FCSTD DOCUMENT  (FreeCAD 0.20R29603 (Git))
Label: assembly
Comment: LumenPnP
License: GPL-3.0 license
LicenseURL: https://github.com/opulo-inc/lumenpnp/blob/main/LICENSE
objects: Part::FeaturePython×437, App::DocumentObjectGroup×34
note: 437 computed .brp shape members not serialized (recipe doc carries the construction recipe); baked Part::Feature solids carry a one-line shape summary decoded from their .brp

FEATURE [Part::FeaturePython] b_OTS_0009_20x20_v_slot_600mm1_001_003  label="vslot-extrusion-20mmx20mmx600mm005"  # a2plus imported part (geometry in sourceFile) (typed FeaturePython)
  Placement = pos=(-0.0573608,219.183,133.936) rot=(0.57735,-0.57735,-0.57735;2.0944rad)
  Visibility1 = true
  a2p_Version = V0.1
  fixedPosition = false
  objectType = a2pPart
  sourceFile = ./MISC/vslot-extrusion-20mmx20mmx600mm.step
  sourcePart = vslot-extrusion-20mmx20mmx600mm
  subassemblyImport = false
  timeLastImport = 1.66119e+09
  updateColors = true
FEATURE [Part::FeaturePython] b_FDM_0008_y_gantry_support_001_  label="y-gantry-support"  # a2plus imported part (geometry in sourceFile) (typed FeaturePython)
  Placement = pos=(32.0603,209.134,74.2154) rot=(0.57735,-0.57735,-0.57735;2.0944rad)
  Visibility1 = true
  a2p_Version = V0.1
  fixedPosition = false
  objectType = a2pPart
  sourceFile = ./FDM/y-gantry-support.FCStd
  sourcePart = Body
  subassemblyImport = false
  timeLastImport = 1.6657e+09
  updateColors = true
FEATURE [Part::FeaturePython] b_FDM_0008_y_gantry_support_001_001  label="y-gantry-support001"  # a2plus imported part (geometry in sourceFile) (typed FeaturePython)
  Placement = pos=(568.145,209.119,74.2225) rot=(0.57735,0.57735,0.57735;2.0944rad)
  Visibility1 = true
  a2p_Version = V0.1
  fixedPosition = false
  objectType = a2pPart
  sourceFile = ./FDM/y-gantry-support.FCStd
  sourcePart = Body
  subassemblyImport = false
  timeLastImport = 1.6657e+09
  updateColors = true
FEATURE [Part::FeaturePython] b_FDM_0009_roller_spacer_001_  label="roller-spacer"  # a2plus imported part (geometry in sourceFile) (typed FeaturePython)
  Placement = pos=(22.0728,209.128,80.348) rot=(0.707107,-0.707107,0;3.14159rad)
  Visibility1 = true
  a2p_Version = V0.1
  fixedPosition = false
  objectType = a2pPart
  sourceFile = ./FDM/roller-spacer.FCStd
  sourcePart = Body
  subassemblyImport = false
  timeLastImport = 1.65531e+09
  updateColors = true
FEATURE [Part::FeaturePython] b_v_slot_roller1_001_  label="vslot-roller"  # a2plus imported part (geometry in sourceFile) (typed FeaturePython)
  Placement = pos=(10.7746,213.864,116.699) rot=(0,0,-1;1.5708rad)
  Visibility1 = true
  a2p_Version = V0.1
  fixedPosition = false
  objectType = a2pPart
  sourceFile = ./MISC/vslot-roller.step
  sourcePart = vslot-roller
  subassemblyImport = false
  timeLastImport = 1.66119e+09
  updateColors = true
FEATURE [Part::FeaturePython] b_v_slot_roller1_001_001  label="vslot-roller001"  # a2plus imported part (geometry in sourceFile) (typed FeaturePython)
  Placement = pos=(10.7212,173.877,116.658) rot=(0,0,-1;1.5708rad)
  Visibility1 = true
  a2p_Version = V0.1
  fixedPosition = false
  objectType = a2pPart
  sourceFile = ./MISC/vslot-roller.step
  sourcePart = vslot-roller
  subassemblyImport = false
  timeLastImport = 1.66119e+09
  updateColors = true
FEATURE [Part::FeaturePython] b_FDM_0009_roller_spacer_001_001  label="roller-spacer001"  # a2plus imported part (geometry in sourceFile) (typed FeaturePython)
  Placement = pos=(-1.94462,209.167,80.3524) rot=(0,0,-1;1.5708rad)
  Visibility1 = true
  a2p_Version = V0.1
  fixedPosition = false
  objectType = a2pPart
  sourceFile = ./FDM/roller-spacer.FCStd
  sourcePart = Body
  subassemblyImport = false
  timeLastImport = 1.65531e+09
  updateColors = true
FEATURE [Part::FeaturePython] b_v_slot_roller1_001_002  label="vslot-roller002"  # a2plus imported part (geometry in sourceFile) (typed FeaturePython)
  Placement = pos=(10.791,193.862,77.3523) rot=(0,0,-1;1.5708rad)
  Visibility1 = true
  a2p_Version = V0.1
  fixedPosition = false
  objectType = a2pPart
  sourceFile = ./MISC/vslot-roller.step
  sourcePart = vslot-roller
  subassemblyImport = false
  timeLastImport = 1.66119e+09
  updateColors = true
FEATURE [Part::FeaturePython] Screw003  label="M5x40-Screw"  # Fasteners workbench fastener (typed FeaturePython)
  Placement = pos=(-6.95,189.16,119.74) rot=(0.57735,-0.57735,-0.57735;2.0944rad)
  Visibility1 = true
  diameter = 6
  invert = false
  leftHanded = false
  length = 12
  lengthCustom = 40
  matchOuter = false
  offset = 0
  thread = false
  type = 33
FEATURE [Part::FeaturePython] Screw004  label="M5x40-Screw334"  # Fasteners workbench fastener (typed FeaturePython)
  Placement = pos=(-6.95,229.11,119.74) rot=(0.57735,-0.57735,-0.57735;2.0944rad)
  Visibility1 = true
  diameter = 6
  invert = false
  leftHanded = false
  length = 12
  lengthCustom = 40
  matchOuter = false
  offset = 0
  thread = false
  type = 33
FEATURE [Part::FeaturePython] Screw005  label="M5x40-Screw335"  # Fasteners workbench fastener (typed FeaturePython)
  Placement = pos=(-6.95,209.15,80.34) rot=(0.57735,-0.57735,-0.57735;2.0944rad)
  Visibility1 = true
  diameter = 6
  invert = false
  leftHanded = false
  length = 12
  lengthCustom = 40
  matchOuter = false
  offset = 0
  thread = false
  type = 33
FEATURE [Part::FeaturePython] Nut003  label="M5-Nut"  # Fasteners workbench fastener (typed FeaturePython)
  Placement = pos=(28.1459,229.05,119.689) rot=(0.447214,0.774597,0.447214;1.82348rad)
  Visibility1 = true
  diameter = 7
  invert = false
  leftHanded = false
  matchOuter = false
  offset = 0
  thread = false
  type = 7
FEATURE [Part::FeaturePython] Nut004  label="M5-Nut599"  # Fasteners workbench fastener (typed FeaturePython)
  Placement = pos=(28.1459,189.008,119.713) rot=(0.447214,0.774597,0.447214;1.82348rad)
  Visibility1 = true
  diameter = 7
  invert = false
  leftHanded = false
  matchOuter = false
  offset = 0
  thread = false
  type = 7
FEATURE [Part::FeaturePython] Nut005  label="M5-Nut600"  # Fasteners workbench fastener (typed FeaturePython)
  Placement = pos=(28.1459,209.108,80.3492) rot=(0.447214,0.774597,0.447214;1.82348rad)
  Visibility1 = true
  diameter = 7
  invert = false
  leftHanded = false
  matchOuter = false
  offset = 0
  thread = false
  type = 7
FEATURE [Part::FeaturePython] Screw006  label="M3x16-Screw"  # Fasteners workbench fastener (typed FeaturePython)
  Placement = pos=(25.03,209.15,61.89) rot=(0.707107,-0.707107,0;3.14159rad)
  Visibility1 = true
  diameter = 4
  invert = false
  leftHanded = false
  length = 6
  lengthCustom = 16
  matchOuter = false
  offset = 0
  thread = false
  type = 33
FEATURE [Part::FeaturePython] Screw007  label="M3x16-Screw097"  # Fasteners workbench fastener (typed FeaturePython)
  Placement = pos=(-4.46,209.15,61.89) rot=(0.707107,-0.707107,0;3.14159rad)
  Visibility1 = true
  diameter = 4
  invert = false
  leftHanded = false
  length = 6
  lengthCustom = 16
  matchOuter = false
  offset = 0
  thread = false
  type = 33
FEATURE [Part::FeaturePython] Nut006  label="M3-Nut"  # Fasteners workbench fastener (typed FeaturePython)
  Placement = pos=(-4.50438,209.156,68.38) rot=(0.707107,-0.707107,0;3.14159rad)
  Visibility1 = true
  diameter = 4
  invert = false
  leftHanded = false
  matchOuter = false
  offset = 0
  thread = false
  type = 4
FEATURE [Part::FeaturePython] Nut007  label="M3-Nut589"  # Fasteners workbench fastener (typed FeaturePython)
  Placement = pos=(24.9349,209.069,68.45) rot=(0,1,0;3.14159rad)
  Visibility1 = true
  diameter = 4
  invert = false
  leftHanded = false
  matchOuter = false
  offset = 0
  thread = false
  type = 4
FEATURE [Part::FeaturePython] Screw016  label="M5x40-Screw336"  # Fasteners workbench fastener (typed FeaturePython)
  Placement = pos=(607.25,189.09,119.82) rot=(0.57735,0.57735,0.57735;2.0944rad)
  Visibility1 = true
  diameter = 6
  invert = false
  leftHanded = false
  length = 12
  lengthCustom = 40
  matchOuter = false
  offset = 0
  thread = false
  type = 33
FEATURE [Part::FeaturePython] b_v_slot_roller1_001_006  label="vslot-roller003"  # a2plus imported part (geometry in sourceFile) (typed FeaturePython)
  Placement = pos=(590.83,186.117,135.005) rot=(0.57735,0.57735,0.57735;4.18879rad)
  Visibility1 = true
  a2p_Version = V0.1
  fixedPosition = false
  objectType = a2pPart
  sourceFile = ./MISC/vslot-roller.step
  sourcePart = vslot-roller
  subassemblyImport = false
  timeLastImport = 1.66119e+09
  updateColors = true
FEATURE [Part::FeaturePython] b_v_slot_roller1_001_007  label="vslot-roller004"  # a2plus imported part (geometry in sourceFile) (typed FeaturePython)
  Placement = pos=(590.853,213.81,116.722) rot=(0,0,-1;1.5708rad)
  Visibility1 = true
  a2p_Version = V0.1
  fixedPosition = false
  objectType = a2pPart
  sourceFile = ./MISC/vslot-roller.step
  sourcePart = vslot-roller
  subassemblyImport = false
  timeLastImport = 1.66119e+09
  updateColors = true
FEATURE [Part::FeaturePython] Screw017  label="M5x40-Screw337"  # Fasteners workbench fastener (typed FeaturePython)
  Placement = pos=(607.25,229.1,119.82) rot=(0.57735,0.57735,0.57735;2.0944rad)
  Visibility1 = true
  diameter = 6
  invert = false
  leftHanded = false
  length = 12
  lengthCustom = 40
  matchOuter = false
  offset = 0
  thread = false
  type = 33
FEATURE [Part::FeaturePython] Screw018  label="M5x40-Screw338"  # Fasteners workbench fastener (typed FeaturePython)
  Placement = pos=(607.25,209.12,80.38) rot=(0.57735,0.57735,0.57735;2.0944rad)
  Visibility1 = true
  diameter = 6
  invert = false
  leftHanded = false
  length = 12
  lengthCustom = 40
  matchOuter = false
  offset = 0
  thread = false
  type = 33
FEATURE [Part::FeaturePython] b_v_slot_roller1_001_008  label="vslot-roller005"  # a2plus imported part (geometry in sourceFile) (typed FeaturePython)
  Placement = pos=(590.853,193.81,77.3723) rot=(0,0,-1;1.5708rad)
  Visibility1 = true
  a2p_Version = V0.1
  fixedPosition = false
  objectType = a2pPart
  sourceFile = ./MISC/vslot-roller.step
  sourcePart = vslot-roller
  subassemblyImport = false
  timeLastImport = 1.66119e+09
  updateColors = true
FEATURE [Part::FeaturePython] Nut016  label="M5-Nut601"  # Fasteners workbench fastener (typed FeaturePython)
  Placement = pos=(568.626,209.08,80.4002) rot=(0.447214,0.774597,0.447214;1.82348rad)
  Visibility1 = true
  diameter = 7
  invert = false
  leftHanded = false
  matchOuter = false
  offset = 0
  thread = false
  type = 7
FEATURE [Part::FeaturePython] Nut017  label="M5-Nut602"  # Fasteners workbench fastener (typed FeaturePython)
  Placement = pos=(568.626,189.034,119.779) rot=(0.447214,0.774597,0.447214;1.82348rad)
  Visibility1 = true
  diameter = 7
  invert = false
  leftHanded = false
  matchOuter = false
  offset = 0
  thread = false
  type = 7
FEATURE [Part::FeaturePython] Nut018  label="M5-Nut603"  # Fasteners workbench fastener (typed FeaturePython)
  Placement = pos=(568.626,229.099,119.753) rot=(0.447214,0.774597,0.447214;1.82348rad)
  Visibility1 = true
  diameter = 7
  invert = false
  leftHanded = false
  matchOuter = false
  offset = 0
  thread = false
  type = 7
FEATURE [Part::FeaturePython] Screw019  label="M3x16-Screw095"  # Fasteners workbench fastener (typed FeaturePython)
  Placement = pos=(575.13,209.15,61.89) rot=(0.707107,-0.707107,0;3.14159rad)
  Visibility1 = true
  diameter = 4
  invert = false
  leftHanded = false
  length = 6
  lengthCustom = 16
  matchOuter = false
  offset = 0
  thread = false
  type = 33
FEATURE [Part::FeaturePython] Screw020  label="M3x16-Screw096"  # Fasteners workbench fastener (typed FeaturePython)
  Placement = pos=(604.72,209.12,61.89) rot=(0.707107,-0.707107,0;3.14159rad)
  Visibility1 = true
  diameter = 4
  invert = false
  leftHanded = false
  length = 6
  lengthCustom = 16
  matchOuter = false
  offset = 0
  thread = false
  type = 33
FEATURE [Part::FeaturePython] Nut019  label="M3-Nut588"  # Fasteners workbench fastener (typed FeaturePython)
  Placement = pos=(575.367,209.236,68.44) rot=(0.707107,-0.707107,0;3.14159rad)
  Visibility1 = true
  diameter = 4
  invert = false
  leftHanded = false
  matchOuter = false
  offset = 0
  thread = false
  type = 4
FEATURE [Part::FeaturePython] Nut020  label="M3-Nut587"  # Fasteners workbench fastener (typed FeaturePython)
  Placement = pos=(604.736,209.133,68.46) rot=(0,1,0;3.14159rad)
  Visibility1 = true
  diameter = 4
  invert = false
  leftHanded = false
  matchOuter = false
  offset = 0
  thread = false
  type = 4
FEATURE [Part::FeaturePython] b_FDM_0009_roller_spacer_001_002  label="roller-spacer002"  # a2plus imported part (geometry in sourceFile) (typed FeaturePython)
  Placement = pos=(578.105,209.167,80.3524) rot=(0,0,-1;1.5708rad)
  Visibility1 = true
  a2p_Version = V0.1
  fixedPosition = false
  objectType = a2pPart
  sourceFile = ./FDM/roller-spacer.FCStd
  sourcePart = Body
  subassemblyImport = false
  timeLastImport = 1.65531e+09
  updateColors = true
FEATURE [Part::FeaturePython] b_FDM_0009_roller_spacer_001_003  label="roller-spacer003"  # a2plus imported part (geometry in sourceFile) (typed FeaturePython)
  Placement = pos=(602.155,209.167,80.3524) rot=(0,0,1;1.5708rad)
  Visibility1 = true
  a2p_Version = V0.1
  fixedPosition = false
  objectType = a2pPart
  sourceFile = ./FDM/roller-spacer.FCStd
  sourcePart = Body
  subassemblyImport = false
  timeLastImport = 1.65531e+09
  updateColors = true
FEATURE [Part::FeaturePython] Screw021  label="M5x40-Screw339"  # Fasteners workbench fastener (typed FeaturePython)
  Placement = pos=(634.23,194.1,163.97) rot=(0,0,1;1.5708rad)
  Visibility1 = true
  diameter = 6
  invert = false
  leftHanded = false
  length = 12
  lengthCustom = 40
  matchOuter = false
  offset = 0
  thread = false
  type = 33
FEATURE [Part::FeaturePython] Screw022  label="M5x10-Screw"  # Fasteners workbench fastener (typed FeaturePython)
  Placement = pos=(25.1,209.12,158.94) rot=(0,0,-1;1.5708rad)
  Visibility1 = true
  diameter = 6
  invert = false
  leftHanded = false
  length = 1
  lengthCustom = 10
  matchOuter = false
  offset = 0
  thread = false
  type = 33
FEATURE [Part::FeaturePython] b_M5_tslot_nut1_001_  label="M5-tslot-nut"  # a2plus imported part (geometry in sourceFile) (typed FeaturePython)
  Placement = pos=(25.0282,209.312,148.905) rot=(0,0,1;0rad)
  Visibility1 = true
  a2p_Version = V0.1
  fixedPosition = false
  objectType = a2pPart
  sourceFile = ./FST/M5-tslot-nut.step
  sourcePart = M5-tslot-nut
  subassemblyImport = false
  timeLastImport = 1.66119e+09
  updateColors = true
FEATURE [Part::FeaturePython] b_M5_tslot_nut1_001_001  label="M5-tslot-nut001"  # a2plus imported part (geometry in sourceFile) (typed FeaturePython)
  Placement = pos=(572.328,209.112,148.905) rot=(0,0,1;0rad)
  Visibility1 = true
  a2p_Version = V0.1
  fixedPosition = false
  objectType = a2pPart
  sourceFile = ./FST/M5-tslot-nut.step
  sourcePart = M5-tslot-nut
  subassemblyImport = false
  timeLastImport = 1.66119e+09
  updateColors = true
FEATURE [Part::FeaturePython] Screw023  label="M5x10-Screw321"  # Fasteners workbench fastener (typed FeaturePython)
  Placement = pos=(572.27,209.12,158.94) rot=(0,0,-1;1.5708rad)
  Visibility1 = true
  diameter = 6
  invert = false
  leftHanded = false
  length = 1
  lengthCustom = 10
  matchOuter = false
  offset = 0
  thread = false
  type = 33
FEATURE [Part::FeaturePython] Screw025  label="M5x10-Screw369"  # Fasteners workbench fastener (typed FeaturePython)
  Placement = pos=(-15.24,236.1,92.45) rot=(0.57735,-0.57735,-0.57735;2.0944rad)
  Visibility1 = true
  diameter = 6
  invert = false
  leftHanded = false
  length = 1
  lengthCustom = 10
  matchOuter = false
  offset = 0
  thread = false
  type = 33
FEATURE [Part::FeaturePython] b_FDM_0027_belt_clamp_001_  label="belt-clamp001"  # a2plus imported part (geometry in sourceFile) (typed FeaturePython)
  Placement = pos=(-12.0481,236.126,99.9408) rot=(0.57735,-0.57735,-0.57735;2.0944rad)
  Visibility1 = true
  a2p_Version = V0.1
  fixedPosition = false
  objectType = a2pPart
  sourceFile = ./FDM/belt-clamp.FCStd
  sourcePart = Body
  subassemblyImport = false
  timeLastImport = 1.66215e+09
  updateColors = true
FEATURE [Part::FeaturePython] Screw026  label="M5x10-Screw370"  # Fasteners workbench fastener (typed FeaturePython)
  Placement = pos=(-15.24,236.1,107.47) rot=(0.57735,-0.57735,-0.57735;2.0944rad)
  Visibility1 = true
  diameter = 6
  invert = false
  leftHanded = false
  length = 1
  lengthCustom = 10
  matchOuter = false
  offset = 0
  thread = false
  type = 33
FEATURE [Part::FeaturePython] Screw027  label="M5x10-Screw371"  # Fasteners workbench fastener (typed FeaturePython)
  Placement = pos=(-15.24,182.19,107.47) rot=(0.57735,-0.57735,-0.57735;2.0944rad)
  Visibility1 = true
  diameter = 6
  invert = false
  leftHanded = false
  length = 1
  lengthCustom = 10
  matchOuter = false
  offset = 0
  thread = false
  type = 33
FEATURE [Part::FeaturePython] Screw028  label="M5x10-Screw372"  # Fasteners workbench fastener (typed FeaturePython)
  Placement = pos=(-15.24,182.19,92.5) rot=(0.57735,-0.57735,-0.57735;2.0944rad)
  Visibility1 = true
  diameter = 6
  invert = false
  leftHanded = false
  length = 1
  lengthCustom = 10
  matchOuter = false
  offset = 0
  thread = false
  type = 33
FEATURE [Part::FeaturePython] b_FDM_0027_belt_clamp_001_001  label="belt-clamp002"  # a2plus imported part (geometry in sourceFile) (typed FeaturePython)
  Placement = pos=(-12.0481,182.176,99.9408) rot=(0.57735,-0.57735,-0.57735;2.0944rad)
  Visibility1 = true
  a2p_Version = V0.1
  fixedPosition = false
  objectType = a2pPart
  sourceFile = ./FDM/belt-clamp.FCStd
  sourcePart = Body
  subassemblyImport = false
  timeLastImport = 1.66215e+09
  updateColors = true
FEATURE [Part::FeaturePython] Screw099  label="M3x8-Screw442"  # Fasteners workbench fastener (typed FeaturePython)
  Placement = pos=(-58.97,224.63,158.88) rot=(1,0,0;3.14159rad)
  Visibility1 = true
  diameter = 1
  invert = false
  leftHanded = false
  length = 1
  lengthCustom = 8
  matchOuter = false
  offset = 0
  thread = false
  type = 39
FEATURE [Part::FeaturePython] Screw097  label="M3x8-Screw443"  # Fasteners workbench fastener (typed FeaturePython)
  Placement = pos=(-27.96,224.63,158.88) rot=(1,0,0;3.14159rad)
  Visibility1 = true
  diameter = 1
  invert = false
  leftHanded = false
  length = 1
  lengthCustom = 8
  matchOuter = false
  offset = 0
  thread = false
  type = 39
FEATURE [Part::FeaturePython] Screw100  label="M3x8-Screw444"  # Fasteners workbench fastener (typed FeaturePython)
  Placement = pos=(-58.97,193.61,158.88) rot=(1,0,0;3.14159rad)
  Visibility1 = true
  diameter = 1
  invert = false
  leftHanded = false
  length = 1
  lengthCustom = 8
  matchOuter = false
  offset = 0
  thread = false
  type = 39
FEATURE [Part::FeaturePython] Screw098  label="M3x8-Screw445"  # Fasteners workbench fastener (typed FeaturePython)
  Placement = pos=(-27.96,193.61,158.88) rot=(1,0,0;3.14159rad)
  Visibility1 = true
  diameter = 1
  invert = false
  leftHanded = false
  length = 1
  lengthCustom = 8
  matchOuter = false
  offset = 0
  thread = false
  type = 39
FEATURE [Part::FeaturePython] Screw059  label="M5x25-Screw122"  # Fasteners workbench fastener (typed FeaturePython)
  Placement = pos=(634.17,209.27,154.08) rot=(0,0,1;1.5708rad)
  Visibility1 = true
  diameter = 6
  invert = false
  leftHanded = false
  length = 6
  lengthCustom = 25
  matchOuter = false
  offset = 0
  thread = false
  type = 33
FEATURE [Part::FeaturePython] Screw060  label="M3x16-Screw084"  # Fasteners workbench fastener (typed FeaturePython)
  Placement = pos=(638.25,224.21,144.08) rot=(0.57735,-0.57735,0.57735;4.18879rad)
  Visibility1 = true
  diameter = 4
  invert = false
  leftHanded = false
  length = 6
  lengthCustom = 16
  matchOuter = false
  offset = 0
  thread = false
  type = 33
FEATURE [Part::FeaturePython] Screw058  label="M5x10-Screw373"  # Fasteners workbench fastener (typed FeaturePython)
  Placement = pos=(615.37,236.11,107.53) rot=(0.57735,0.57735,0.57735;2.0944rad)
  Visibility1 = true
  diameter = 6
  invert = false
  leftHanded = false
  length = 1
  lengthCustom = 10
  matchOuter = false
  offset = 0
  thread = false
  type = 33
FEATURE [Part::FeaturePython] Screw057  label="M5x10-Screw374"  # Fasteners workbench fastener (typed FeaturePython)
  Placement = pos=(615.37,236.11,92.54) rot=(0.57735,0.57735,0.57735;2.0944rad)
  Visibility1 = true
  diameter = 6
  invert = false
  leftHanded = false
  length = 1
  lengthCustom = 10
  matchOuter = false
  offset = 0
  thread = false
  type = 33
FEATURE [Part::FeaturePython] Screw056  label="M5x10-Screw367"  # Fasteners workbench fastener (typed FeaturePython)
  Placement = pos=(615.37,182.19,92.54) rot=(0.57735,0.57735,0.57735;2.0944rad)
  Visibility1 = true
  diameter = 6
  invert = false
  leftHanded = false
  length = 1
  lengthCustom = 10
  matchOuter = false
  offset = 0
  thread = false
  type = 33
FEATURE [Part::FeaturePython] b_FDM_0027_belt_clamp_001_005  label="belt-clamp003"  # a2plus imported part (geometry in sourceFile) (typed FeaturePython)
  Placement = pos=(612.402,182.156,99.9408) rot=(0.57735,0.57735,0.57735;2.0944rad)
  Visibility1 = true
  a2p_Version = V0.1
  fixedPosition = false
  objectType = a2pPart
  sourceFile = ./FDM/belt-clamp.FCStd
  sourcePart = Body
  subassemblyImport = false
  timeLastImport = 1.66215e+09
  updateColors = true
FEATURE [Part::FeaturePython] b_FDM_0027_belt_clamp_001_004  label="belt-clamp004"  # a2plus imported part (geometry in sourceFile) (typed FeaturePython)
  Placement = pos=(612.402,236.126,100.011) rot=(0.57735,0.57735,0.57735;2.0944rad)
  Visibility1 = true
  a2p_Version = V0.1
  fixedPosition = false
  objectType = a2pPart
  sourceFile = ./FDM/belt-clamp.FCStd
  sourcePart = Body
  subassemblyImport = false
  timeLastImport = 1.66215e+09
  updateColors = true
FEATURE [Part::FeaturePython] b_Nema_17_42A02C_v21_001_001  label="NEMA17-stepper"  # a2plus imported part (geometry in sourceFile) (typed FeaturePython)
  Placement = pos=(-43.4338,209.138,153.958) rot=(1,0,0;3.14159rad)
  Visibility1 = true
  a2p_Version = V0.1
  fixedPosition = false
  objectType = a2pPart
  sourceFile = ./MISC/NEMA17-stepper.step 
  sourcePart = NEMA17-stepper
  subassemblyImport = false
  timeLastImport = 1.64563e+09
  updateColors = true
FEATURE [Part::FeaturePython] Nut043  label="M5-Nut604"  # Fasteners workbench fastener (typed FeaturePython)
  Placement = pos=(634.166,209.269,134.219) rot=(0.707107,-0.707107,0;3.14159rad)
  Visibility1 = true
  diameter = 3
  invert = false
  leftHanded = false
  matchOuter = false
  offset = 0
  thread = false
  type = 5
FEATURE [Part::FeaturePython] Nut042  label="M5-Nut605"  # Fasteners workbench fastener (typed FeaturePython)
  Placement = pos=(634.224,194.15,128.957) rot=(0.866025,0.5,0;3.14159rad)
  Visibility1 = true
  diameter = 3
  invert = false
  leftHanded = false
  matchOuter = false
  offset = 0
  thread = false
  type = 5
FEATURE [Part::FeaturePython] b_Gates_2GT_20T_Toothed_Pulley1_001_001  label="GT2-pulley"  # a2plus imported part (geometry in sourceFile) (typed FeaturePython)
  Placement = pos=(-43.4196,209.139,155.221) rot=(0.57735,0.57735,-0.57735;4.18879rad)
  Visibility1 = true
  a2p_Version = V0.1
  fixedPosition = false
  objectType = a2pPart
  sourceFile = ./cad/MISC/GT2-pulley.STEP
  sourcePart = GT2-pulley
  subassemblyImport = false
  timeLastImport = 1.64563e+09
  updateColors = true
FEATURE [Part::FeaturePython] b_Gates_2GT_20T_Toothed_Idler1_001_002  label="GT2-idler"  # a2plus imported part (geometry in sourceFile) (typed FeaturePython)
  Placement = pos=(634.179,209.286,138.99) rot=(0.57735,-0.57735,-0.57735;2.0944rad)
  Visibility1 = true
  a2p_Version = V0.1
  fixedPosition = false
  objectType = a2pPart
  sourceFile = ./cad/MISC/GT2-idler.STEP
  sourcePart = GT2-idler
  subassemblyImport = false
  timeLastImport = 1.64563e+09
  updateColors = true
FEATURE [Part::FeaturePython] Screw055  label="M5x10-Screw368"  # Fasteners workbench fastener (typed FeaturePython)
  Placement = pos=(615.37,182.19,107.47) rot=(0.57735,0.57735,0.57735;2.0944rad)
  Visibility1 = true
  diameter = 6
  invert = false
  leftHanded = false
  length = 1
  lengthCustom = 10
  matchOuter = false
  offset = 0
  thread = false
  type = 33
FEATURE [Part::FeaturePython] Nut037  label="M5-Nut688"  # Fasteners workbench fastener (typed FeaturePython)
  Placement = pos=(-8.89406,182.185,92.4364) rot=(0.447214,0.774597,0.447214;1.82348rad)
  Visibility1 = true
  diameter = 7
  invert = false
  leftHanded = false
  matchOuter = false
  offset = 0
  thread = false
  type = 7
FEATURE [Part::FeaturePython] Nut035  label="M5-Nut689"  # Fasteners workbench fastener (typed FeaturePython)
  Placement = pos=(-8.89406,236.086,107.516) rot=(0.447214,0.774597,0.447214;1.82348rad)
  Visibility1 = true
  diameter = 7
  invert = false
  leftHanded = false
  matchOuter = false
  offset = 0
  thread = false
  type = 7
FEATURE [Part::FeaturePython] Nut041  label="M5-Nut690"  # Fasteners workbench fastener (typed FeaturePython)
  Placement = pos=(605.676,236.093,107.547) rot=(0.447214,0.774597,0.447214;1.82348rad)
  Visibility1 = true
  diameter = 7
  invert = false
  leftHanded = false
  matchOuter = false
  offset = 0
  thread = false
  type = 7
FEATURE [Part::FeaturePython] Nut040  label="M5-Nut691"  # Fasteners workbench fastener (typed FeaturePython)
  Placement = pos=(605.676,236.072,92.571) rot=(0.447214,0.774597,0.447214;1.82348rad)
  Visibility1 = true
  diameter = 7
  invert = false
  leftHanded = false
  matchOuter = false
  offset = 0
  thread = false
  type = 7
FEATURE [Part::FeaturePython] Nut036  label="M5-Nut692"  # Fasteners workbench fastener (typed FeaturePython)
  Placement = pos=(-8.89406,182.149,107.434) rot=(0.447214,0.774597,0.447214;1.82348rad)
  Visibility1 = true
  diameter = 7
  invert = false
  leftHanded = false
  matchOuter = false
  offset = 0
  thread = false
  type = 7
FEATURE [Part::FeaturePython] Nut034  label="M5-Nut693"  # Fasteners workbench fastener (typed FeaturePython)
  Placement = pos=(-8.89406,236.073,92.5127) rot=(0.447214,0.774597,0.447214;1.82348rad)
  Visibility1 = true
  diameter = 7
  invert = false
  leftHanded = false
  matchOuter = false
  offset = 0
  thread = false
  type = 7
FEATURE [Part::FeaturePython] Nut039  label="M5-Nut694"  # Fasteners workbench fastener (typed FeaturePython)
  Placement = pos=(605.676,182.149,107.514) rot=(0.447214,0.774597,0.447214;1.82348rad)
  Visibility1 = true
  diameter = 7
  invert = false
  leftHanded = false
  matchOuter = false
  offset = 0
  thread = false
  type = 7
FEATURE [Part::FeaturePython] Nut038  label="M5-Nut695"  # Fasteners workbench fastener (typed FeaturePython)
  Placement = pos=(605.676,182.168,92.527) rot=(0.447214,0.774597,0.447214;1.82348rad)
  Visibility1 = true
  diameter = 7
  invert = false
  leftHanded = false
  matchOuter = false
  offset = 0
  thread = false
  type = 7
FEATURE [Part::FeaturePython] Nut044  label="M3-Nut451"  # Fasteners workbench fastener (typed FeaturePython)
  Placement = pos=(632.154,224.209,144.071) rot=(0.447214,-0.774597,-0.447214;1.82348rad)
  Visibility1 = true
  diameter = 4
  invert = false
  leftHanded = false
  matchOuter = false
  offset = 0
  thread = false
  type = 7
FEATURE [Part::FeaturePython] b_MakerBot_LimitSwitchBoard1_001_002  label="limit-switch001"  # a2plus imported part (geometry in sourceFile) (typed FeaturePython)
  Placement = pos=(492.283,187.439,201.553) rot=(0,0,1;3.14159rad)
  Visibility1 = true
  a2p_Version = V0.1
  fixedPosition = false
  objectType = a2pPart
  sourceFile = ./PCB/limit-switch.STEP
  sourcePart = limit-switch
  subassemblyImport = false
  timeLastImport = 1.66119e+09
  updateColors = true
FEATURE [Part::FeaturePython] b_OTS_0002_00_usb_webcam_001_  label="usb-camera"  # a2plus imported part (geometry in sourceFile) (typed FeaturePython)
  Placement = pos=(444.284,221.423,101.09) rot=(1,0,0;3.14159rad)
  Visibility1 = true
  a2p_Version = V0.1
  fixedPosition = false
  objectType = a2pPart
  sourceFile = ./MISC/usb-camera.FCStd
  sourcePart = Body
  subassemblyImport = false
  timeLastImport = 1.66758e+09
  updateColors = true
FEATURE [Part::FeaturePython] b_FDM_0011_x_gantry_front_001_  label="x-gantry-front"  # a2plus imported part (geometry in sourceFile) (typed FeaturePython)
  Placement = pos=(443.743,197.353,123.214) rot=(1,0,0;1.5708rad)
  Visibility1 = true
  a2p_Version = V0.1
  fixedPosition = false
  objectType = a2pPart
  sourceFile = ./FDM/x-gantry-front.FCStd
  sourcePart = Body
  subassemblyImport = false
  timeLastImport = 1.6657e+09
  updateColors = true
FEATURE [Part::FeaturePython] b_FDM_0014_down_camera_mount_001_  label="top-camera-mount"  # a2plus imported part (geometry in sourceFile) (typed FeaturePython)
  Placement = pos=(444.094,221.392,104.569) rot=(0,0,1;3.14159rad)
  Visibility1 = true
  a2p_Version = V0.1
  fixedPosition = false
  objectType = a2pPart
  sourceFile = ./FDM/top-camera-mount.FCStd
  sourcePart = Body
  subassemblyImport = false
  timeLastImport = 1.66759e+09
  updateColors = true
FEATURE [Part::FeaturePython] b_FDM_0015_down_light_mount_001_  label="top-light-mount"  # a2plus imported part (geometry in sourceFile) (typed FeaturePython)
  Placement = pos=(444.05,221.445,81.0718) rot=(-0.831467,0.554706,-0.031047;0rad)
  Visibility1 = true
  a2p_Version = V0.1
  fixedPosition = false
  objectType = a2pPart
  sourceFile = ./FDM/top-light-mount.FCStd
  sourcePart = Body
  subassemblyImport = false
  timeLastImport = 1.66758e+09
  updateColors = true
FEATURE [Part::FeaturePython] b_v_slot_roller1_001_003  label="vslot-roller006"  # a2plus imported part (geometry in sourceFile) (typed FeaturePython)
  Placement = pos=(415.819,209.923,180.083) rot=(0,-1,0;1.5708rad)
  Visibility1 = true
  a2p_Version = V0.1
  fixedPosition = false
  objectType = a2pPart
  sourceFile = ./MISC/vslot-roller.step
  sourcePart = vslot-roller
  subassemblyImport = false
  timeLastImport = 1.66119e+09
  updateColors = true
FEATURE [Part::FeaturePython] b_v_slot_roller1_001_004  label="vslot-roller007"  # a2plus imported part (geometry in sourceFile) (typed FeaturePython)
  Placement = pos=(477.819,209.923,180.083) rot=(0,-1,0;1.5708rad)
  Visibility1 = true
  a2p_Version = V0.1
  fixedPosition = false
  objectType = a2pPart
  sourceFile = ./MISC/vslot-roller.step
  sourcePart = vslot-roller
  subassemblyImport = false
  timeLastImport = 1.66119e+09
  updateColors = true
FEATURE [Part::FeaturePython] b_FDM_0027_belt_clamp_001_002  label="belt-clamp005"  # a2plus imported part (geometry in sourceFile) (typed FeaturePython)
  Placement = pos=(422.82,231.252,143.964) rot=(-1,0,0;1.5708rad)
  Visibility1 = true
  a2p_Version = V0.1
  fixedPosition = false
  objectType = a2pPart
  sourceFile = ./FDM/belt-clamp.FCStd
  sourcePart = Body
  subassemblyImport = false
  timeLastImport = 1.66215e+09
  updateColors = true
FEATURE [Part::FeaturePython] Nut021  label="M5-Nut646"  # Fasteners workbench fastener (typed FeaturePython)
  Placement = pos=(464.836,225.2,151.517) rot=(-0.186157,0.694747,0.694747;2.77349rad)
  Visibility1 = true
  diameter = 7
  invert = false
  leftHanded = false
  matchOuter = false
  offset = 0
  thread = false
  type = 7
FEATURE [Part::FeaturePython] Nut022  label="M5-Nut647"  # Fasteners workbench fastener (typed FeaturePython)
  Placement = pos=(464.776,225.2,136.591) rot=(-0.186157,0.694747,0.694747;2.77349rad)
  Visibility1 = true
  diameter = 7
  invert = false
  leftHanded = false
  matchOuter = false
  offset = 0
  thread = false
  type = 7
FEATURE [Part::FeaturePython] Screw038  label="M5x10-Screw356"  # Fasteners workbench fastener (typed FeaturePython)
  Placement = pos=(464.84,234.23,136.48) rot=(0.57735,0.57735,0.57735;4.18879rad)
  Visibility1 = true
  diameter = 6
  invert = false
  leftHanded = false
  length = 1
  lengthCustom = 10
  matchOuter = false
  offset = 0
  thread = false
  type = 33
FEATURE [Part::FeaturePython] Screw039  label="M5x10-Screw357"  # Fasteners workbench fastener (typed FeaturePython)
  Placement = pos=(464.74,234.23,151.54) rot=(0.57735,0.57735,0.57735;4.18879rad)
  Visibility1 = true
  diameter = 6
  invert = false
  leftHanded = false
  length = 1
  lengthCustom = 10
  matchOuter = false
  offset = 0
  thread = false
  type = 33
FEATURE [Part::FeaturePython] Nut023  label="M5-Nut648"  # Fasteners workbench fastener (typed FeaturePython)
  Placement = pos=(422.834,225.2,136.517) rot=(-0.186157,0.694747,0.694747;2.77349rad)
  Visibility1 = true
  diameter = 7
  invert = false
  leftHanded = false
  matchOuter = false
  offset = 0
  thread = false
  type = 7
FEATURE [Part::FeaturePython] Nut024  label="M5-Nut649"  # Fasteners workbench fastener (typed FeaturePython)
  Placement = pos=(422.794,225.2,151.519) rot=(-0.186157,0.694747,0.694747;2.77349rad)
  Visibility1 = true
  diameter = 7
  invert = false
  leftHanded = false
  matchOuter = false
  offset = 0
  thread = false
  type = 7
FEATURE [Part::FeaturePython] Screw040  label="M5x10-Screw358"  # Fasteners workbench fastener (typed FeaturePython)
  Placement = pos=(422.86,234.23,151.54) rot=(0.57735,0.57735,0.57735;4.18879rad)
  Visibility1 = true
  diameter = 6
  invert = false
  leftHanded = false
  length = 1
  lengthCustom = 10
  matchOuter = false
  offset = 0
  thread = false
  type = 33
FEATURE [Part::FeaturePython] b_FDM_0027_belt_clamp_001_003  label="belt-clamp006"  # a2plus imported part (geometry in sourceFile) (typed FeaturePython)
  Placement = pos=(464.82,231.252,144.064) rot=(0,0.707107,0.707107;3.14159rad)
  Visibility1 = true
  a2p_Version = V0.1
  fixedPosition = false
  objectType = a2pPart
  sourceFile = ./FDM/belt-clamp.FCStd
  sourcePart = Body
  subassemblyImport = false
  timeLastImport = 1.66215e+09
  updateColors = true
FEATURE [Part::FeaturePython] Screw123  label="M3x8-Screw"  # Fasteners workbench fastener (typed FeaturePython)
  Placement = pos=(494.62,185.82,196.26) rot=(1,0,0;1.5708rad)
  Visibility1 = true
  diameter = 1
  invert = false
  leftHanded = false
  length = 9
  lengthCustom = 8
  matchOuter = false
  offset = 0
  thread = false
  type = 39
FEATURE [Part::FeaturePython] Screw124  label="M3x8-Screw548"  # Fasteners workbench fastener (typed FeaturePython)
  Placement = pos=(475.78,185.82,196.26) rot=(1,0,0;1.5708rad)
  Visibility1 = true
  diameter = 1
  invert = false
  leftHanded = false
  length = 9
  lengthCustom = 8
  matchOuter = false
  offset = 0
  thread = false
  type = 39
FEATURE [Part::FeaturePython] b_Nema_17_42A02C_v21_001_  label="NEMA17-stepper001"  # a2plus imported part (geometry in sourceFile) (typed FeaturePython)
  Placement = pos=(443.776,187.252,212.248) rot=(-0.268444,0.681153,-0.681153;3.66612rad)
  Visibility1 = true
  a2p_Version = V0.1
  fixedPosition = false
  objectType = a2pPart
  sourceFile = ./MISC/NEMA17-stepper.step 
  sourcePart = NEMA17-stepper
  subassemblyImport = false
  timeLastImport = 1.64563e+09
  updateColors = true
FEATURE [Part::FeaturePython] b_Gates_2GT_20T_Toothed_Idler1_001_  label="GT2-idler001"  # a2plus imported part (geometry in sourceFile) (typed FeaturePython)
  Placement = pos=(443.78,185.1,99.0503) rot=(-0.707107,0,0.707107;3.14159rad)
  Visibility1 = true
  a2p_Version = V0.1
  fixedPosition = false
  objectType = a2pPart
  sourceFile = ./cad/MISC/GT2-idler.STEP
  sourcePart = GT2-idler
  subassemblyImport = false
  timeLastImport = 1.64563e+09
  updateColors = true
FEATURE [Part::FeaturePython] Screw045  label="M3x14-Screw"  # Fasteners workbench fastener (typed FeaturePython)
  Placement = pos=(423.76,183.29,183.99) rot=(1,0,0;1.5708rad)
  Visibility1 = true
  diameter = 1
  invert = false
  leftHanded = false
  length = 9
  lengthCustom = 14
  matchOuter = false
  offset = 0
  thread = false
  type = 39
FEATURE [Part::FeaturePython] Screw046  label="M3x14-Screw172"  # Fasteners workbench fastener (typed FeaturePython)
  Placement = pos=(423.76,183.29,143.9) rot=(1,0,0;1.5708rad)
  Visibility1 = true
  diameter = 1
  invert = false
  leftHanded = false
  length = 9
  lengthCustom = 14
  matchOuter = false
  offset = 0
  thread = false
  type = 39
FEATURE [Part::FeaturePython] Screw047  label="M3x14-Screw173"  # Fasteners workbench fastener (typed FeaturePython)
  Placement = pos=(423.76,183.29,103.98) rot=(1,0,0;1.5708rad)
  Visibility1 = true
  diameter = 1
  invert = false
  leftHanded = false
  length = 9
  lengthCustom = 14
  matchOuter = false
  offset = 0
  thread = false
  type = 39
FEATURE [Part::FeaturePython] Screw049  label="M3x14-Screw174"  # Fasteners workbench fastener (typed FeaturePython)
  Placement = pos=(463.82,183.29,143.94) rot=(1,0,0;1.5708rad)
  Visibility1 = true
  diameter = 1
  invert = false
  leftHanded = false
  length = 9
  lengthCustom = 14
  matchOuter = false
  offset = 0
  thread = false
  type = 39
FEATURE [Part::FeaturePython] Screw050  label="M3x14-Screw175"  # Fasteners workbench fastener (typed FeaturePython)
  Placement = pos=(463.82,183.29,183.95) rot=(1,0,0;1.5708rad)
  Visibility1 = true
  diameter = 1
  invert = false
  leftHanded = false
  length = 9
  lengthCustom = 14
  matchOuter = false
  offset = 0
  thread = false
  type = 39
FEATURE [Part::FeaturePython] Screw086  label="M3x8-Screw507"  # Fasteners workbench fastener (typed FeaturePython)
  Placement = pos=(443.74,191.38,190.34) rot=(1,0,0;1.5708rad)
  Visibility1 = true
  diameter = 1
  invert = false
  leftHanded = false
  length = 1
  lengthCustom = 8
  matchOuter = false
  offset = 0
  thread = false
  type = 39
FEATURE [Part::FeaturePython] Screw087  label="M3x8-Screw508"  # Fasteners workbench fastener (typed FeaturePython)
  Placement = pos=(465.75,191.38,212.29) rot=(1,0,0;1.5708rad)
  Visibility1 = true
  diameter = 1
  invert = false
  leftHanded = false
  length = 1
  lengthCustom = 8
  matchOuter = false
  offset = 0
  thread = false
  type = 39
FEATURE [Part::FeaturePython] Screw088  label="M3x8-Screw509"  # Fasteners workbench fastener (typed FeaturePython)
  Placement = pos=(421.83,191.38,212.25) rot=(1,0,0;1.5708rad)
  Visibility1 = true
  diameter = 1
  invert = false
  leftHanded = false
  length = 1
  lengthCustom = 8
  matchOuter = false
  offset = 0
  thread = false
  type = 39
FEATURE [Part::FeaturePython] Nut032  label="M3-Nut520"  # Fasteners workbench fastener (typed FeaturePython)
  Placement = pos=(423.74,196.87,104.003) rot=(0.935113,0.250563,-0.250563;1.63783rad)
  Visibility1 = true
  diameter = 4
  invert = false
  leftHanded = false
  matchOuter = false
  offset = 0
  thread = false
  type = 7
FEATURE [Part::FeaturePython] Nut028  label="M3-Nut521"  # Fasteners workbench fastener (typed FeaturePython)
  Placement = pos=(423.738,196.87,143.899) rot=(0.935113,0.250563,-0.250563;1.63783rad)
  Visibility1 = true
  diameter = 4
  invert = false
  leftHanded = false
  matchOuter = false
  offset = 0
  thread = false
  type = 7
FEATURE [Part::FeaturePython] Nut027  label="M3-Nut522"  # Fasteners workbench fastener (typed FeaturePython)
  Placement = pos=(423.75,196.87,183.96) rot=(0.935113,0.250563,-0.250563;1.63783rad)
  Visibility1 = true
  diameter = 4
  invert = false
  leftHanded = false
  matchOuter = false
  offset = 0
  thread = false
  type = 7
FEATURE [Part::FeaturePython] Nut031  label="M3-Nut523"  # Fasteners workbench fastener (typed FeaturePython)
  Placement = pos=(463.628,196.87,184.111) rot=(0.935113,0.250563,-0.250563;1.63783rad)
  Visibility1 = true
  diameter = 4
  invert = false
  leftHanded = false
  matchOuter = false
  offset = 0
  thread = false
  type = 7
FEATURE [Part::FeaturePython] Nut029  label="M3-Nut524"  # Fasteners workbench fastener (typed FeaturePython)
  Placement = pos=(463.702,196.87,104.059) rot=(0.935113,0.250563,-0.250563;1.63783rad)
  Visibility1 = true
  diameter = 4
  invert = false
  leftHanded = false
  matchOuter = false
  offset = 0
  thread = false
  type = 7
FEATURE [Part::FeaturePython] Nut030  label="M3-Nut525"  # Fasteners workbench fastener (typed FeaturePython)
  Placement = pos=(463.67,196.87,144.204) rot=(0.935113,0.250563,-0.250563;1.63783rad)
  Visibility1 = true
  diameter = 4
  invert = false
  leftHanded = false
  matchOuter = false
  offset = 0
  thread = false
  type = 7
FEATURE [Part::FeaturePython] Screw044  label="M5x25-Screw135"  # Fasteners workbench fastener (typed FeaturePython)
  Placement = pos=(443.743,175.103,98.994) rot=(0,0.707107,-0.707107;3.14159rad)
  Visibility1 = true
  diameter = 6
  invert = false
  leftHanded = false
  length = 6
  lengthCustom = 25
  matchOuter = false
  offset = 10.5
  thread = false
  type = 33
FEATURE [Part::FeaturePython] b_v_slot_roller1_001_005  label="vslot-roller008"  # a2plus imported part (geometry in sourceFile) (typed FeaturePython)
  Placement = pos=(415.379,210.523,140.88) rot=(0,-1,0;1.5708rad)
  Visibility1 = true
  a2p_Version = V0.1
  fixedPosition = false
  objectType = a2pPart
  sourceFile = ./MISC/vslot-roller.step
  sourcePart = vslot-roller
  subassemblyImport = false
  timeLastImport = 1.66119e+09
  updateColors = true
FEATURE [Part::FeaturePython] Screw041  label="M5x10-Screw359"  # Fasteners workbench fastener (typed FeaturePython)
  Placement = pos=(422.89,234.23,136.48) rot=(0.57735,0.57735,0.57735;4.18879rad)
  Visibility1 = true
  diameter = 6
  invert = false
  leftHanded = false
  length = 1
  lengthCustom = 10
  matchOuter = false
  offset = 0
  thread = false
  type = 33
FEATURE [Part::FeaturePython] b_Gates_2GT_20T_Toothed_Pulley1_001_  label="GT2-pulley001"  # a2plus imported part (geometry in sourceFile) (typed FeaturePython)
  Placement = pos=(443.79,192,212.28) rot=(-0.707107,0,0.707107;3.14159rad)
  Visibility1 = true
  a2p_Version = V0.1
  fixedPosition = false
  objectType = a2pPart
  sourceFile = ./cad/MISC/GT2-pulley.STEP
  sourcePart = GT2-pulley
  subassemblyImport = false
  timeLastImport = 1.64563e+09
  updateColors = true
FEATURE [Part::FeaturePython] b_FDM_0040_z_gantry_backplate_left_001_  label="z-gantry-backplate-left"  # a2plus imported part (geometry in sourceFile) (typed FeaturePython)
  Placement = pos=(405.5,177.8,112.56) rot=(1,0,0;1.5708rad)
  a2p_Version = V0.1
  fixedPosition = false
  objectType = a2pPart
  sourceFile = .\FDM\z-gantry-backplate-left.FCStd
  subassemblyImport = false
  timeLastImport = 1.65531e+09
  updateColors = true
FEATURE [Part::FeaturePython] Screw144  label="M3x8-Screw531"  # Fasteners workbench fastener (typed FeaturePython)
  Placement = pos=(416.22,171.94,150.64) rot=(1,0,0;1.5708rad)
  Visibility1 = true
  diameter = 1
  invert = false
  leftHanded = false
  length = 1
  lengthCustom = 8
  matchOuter = false
  offset = 0
  thread = false
  type = 39
FEATURE [Part::FeaturePython] Screw146  label="M3x8-Screw532"  # Fasteners workbench fastener (typed FeaturePython)
  Placement = pos=(431.25,171.94,150.53) rot=(1,0,0;1.5708rad)
  Visibility1 = true
  diameter = 1
  invert = false
  leftHanded = false
  length = 1
  lengthCustom = 8
  matchOuter = false
  offset = 0
  thread = false
  type = 39
FEATURE [Part::FeaturePython] b_OTS_0001_00_CP40_nozzle_holder_001_  label="CP40-holder"  # a2plus imported part (geometry in sourceFile) (typed FeaturePython)
  Placement = pos=(420.048,155.79,87.7845) rot=(0.57735,-0.57735,-0.57735;2.0944rad)
  Visibility1 = true
  a2p_Version = V0.1
  fixedPosition = false
  objectType = a2pPart
  sourceFile = ./MISC/cp40-holder.FCStd
  sourcePart = Body
  subassemblyImport = false
  timeLastImport = 1.65531e+09
  updateColors = true
FEATURE [Part::FeaturePython] b_MS4M_M51_001_  label="pneumatic-adapter-MS4M-M5"  # a2plus imported part (geometry in sourceFile) (typed FeaturePython)
  Placement = pos=(420.152,155.83,162.512) rot=(0.57735,-0.57735,-0.57735;2.0944rad)
  Visibility1 = true
  a2p_Version = V0.1
  fixedPosition = false
  objectType = a2pPart
  sourceFile = ./MISC/pneumatic-adapter-MS4M-M5.STEP
  sourcePart = MS4M-M5
  subassemblyImport = false
  timeLastImport = 1.65531e+09
  updateColors = true
FEATURE [Part::FeaturePython] Screw148  label="M3x8-Screw523"  # Fasteners workbench fastener (typed FeaturePython)
  Placement = pos=(456.42,171.94,150.5) rot=(1,0,0;1.5708rad)
  Visibility1 = true
  diameter = 1
  invert = false
  leftHanded = false
  length = 1
  lengthCustom = 8
  matchOuter = false
  offset = 0
  thread = false
  type = 39
FEATURE [Part::FeaturePython] Screw149  label="M3x8-Screw524"  # Fasteners workbench fastener (typed FeaturePython)
  Placement = pos=(471.41,171.94,150.5) rot=(1,0,0;1.5708rad)
  Visibility1 = true
  diameter = 1
  invert = false
  leftHanded = false
  length = 1
  lengthCustom = 8
  matchOuter = false
  offset = 0
  thread = false
  type = 39
FEATURE [Part::FeaturePython] b_FDM_0041_z_gantry_backplate_right_001_  label="z-gantry-backplate-right"  # a2plus imported part (geometry in sourceFile) (typed FeaturePython)
  Placement = pos=(482.233,178.019,112.536) rot=(1,0,0;1.5708rad)
  a2p_Version = V0.1
  fixedPosition = false
  objectType = a2pPart
  sourceFile = ./FDM/z-gantry-backplate-right.FCStd
  sourcePart = Body
  subassemblyImport = false
  timeLastImport = 1.6657e+09
  updateColors = true
FEATURE [Part::FeaturePython] Screw048  label="M3x14-Screw176"  # Fasteners workbench fastener (typed FeaturePython)
  Placement = pos=(463.82,183.29,103.98) rot=(1,0,0;1.5708rad)
  Visibility1 = true
  diameter = 1
  invert = false
  leftHanded = false
  length = 9
  lengthCustom = 14
  matchOuter = false
  offset = 0
  thread = false
  type = 39
FEATURE [Part::FeaturePython] Screw085  label="M3x8-Screw518"  # Fasteners workbench fastener (typed FeaturePython)
  Placement = pos=(443.74,191.38,234.2) rot=(1,0,0;1.5708rad)
  Visibility1 = true
  diameter = 1
  invert = false
  leftHanded = false
  length = 1
  lengthCustom = 8
  matchOuter = false
  offset = 0
  thread = false
  type = 39
FEATURE [Part::FeaturePython] b_FDM_0009_roller_spacer_001_004  label="roller-spacer004"  # a2plus imported part (geometry in sourceFile) (typed FeaturePython)
  Placement = pos=(412.82,197.452,164.814) rot=(0,1,0;3.14159rad)
  a2p_Version = V0.1
  fixedPosition = false
  objectType = a2pPart
  sourceFile = ./FDM/roller-spacer.FCStd
  subassemblyImport = false
  timeLastImport = 1.65531e+09
  updateColors = true
FEATURE [Part::FeaturePython] b_FDM_0009_roller_spacer_001_005  label="roller-spacer005"  # a2plus imported part (geometry in sourceFile) (typed FeaturePython)
  Placement = pos=(474.82,197.452,164.814) rot=(0,1,0;3.14159rad)
  a2p_Version = V0.1
  fixedPosition = false
  objectType = a2pPart
  sourceFile = ./FDM/roller-spacer.FCStd
  subassemblyImport = false
  timeLastImport = 1.65531e+09
  updateColors = true
FEATURE [Part::FeaturePython] b_FDM_0043_001_  label="x-gantry-roller-carriage"  # a2plus imported part (geometry in sourceFile) (typed FeaturePython)
  Placement = pos=(443.63,202.352,125.61) rot=(1,0,0;1.5708rad)
  a2p_Version = V0.1
  fixedPosition = false
  objectType = a2pPart
  sourceFile = ./FDM/x-gantry-roller-carriage.FCStd
  subassemblyImport = false
  timeLastImport = 1.65531e+09
  updateColors = true
FEATURE [Part::FeaturePython] Screw165  label="M3x30-Screw159"  # Fasteners workbench fastener (typed FeaturePython)
  Placement = pos=(402.38,192.352,121.01) rot=(-0.707107,0.707107,0;3.14159rad)
  baseObject = -> b_FDM_0043_001_ [Edge671]
  diameter = 4
  invert = false
  leftHanded = false
  length = 9
  lengthCustom = 30
  matchOuter = false
  offset = 0
  thread = false
  type = 33
FEATURE [Part::FeaturePython] b_FDM_0043_001_001  label="x-gantry-roller-carriage001"  # a2plus imported part (geometry in sourceFile) (typed FeaturePython)
  Placement = pos=(443.63,216.445,125.95) rot=(0,0.707492,0.706721;3.14159rad)
  a2p_Version = V0.1
  fixedPosition = false
  objectType = a2pPart
  sourceFile = ./FDM/x-gantry-roller-carriage.FCStd
  subassemblyImport = false
  timeLastImport = 1.65531e+09
  updateColors = true
FEATURE [Part::FeaturePython] Screw166  label="M3x30-Screw167"  # Fasteners workbench fastener (typed FeaturePython)
  Placement = pos=(402.38,226.29,121.01) rot=(-0.707107,0.707107,0;3.14159rad)
  baseObject = -> b_FDM_0043_001_001 [Edge60]
  diameter = 4
  invert = false
  leftHanded = false
  length = 9
  lengthCustom = 30
  matchOuter = false
  offset = 0
  thread = false
  type = 33
FEATURE [Part::FeaturePython] Screw167  label="M3x30-Screw168"  # Fasteners workbench fastener (typed FeaturePython)
  Placement = pos=(484.88,226.287,121.01) rot=(-0.707107,0.707107,0;3.14159rad)
  baseObject = -> b_FDM_0043_001_001 [Edge69]
  diameter = 4
  invert = false
  leftHanded = false
  length = 9
  lengthCustom = 30
  matchOuter = false
  offset = 0
  thread = false
  type = 33
FEATURE [Part::FeaturePython] Screw  label="M5x40-Screw354"  # Fasteners workbench fastener (typed FeaturePython)
  Placement = pos=(474.82,192.252,164.814) rot=(1,0,0;1.5708rad)
  diameter = 6
  invert = true
  leftHanded = false
  length = 9
  lengthCustom = 40
  matchOuter = false
  offset = 0
  thread = false
  type = 33
FEATURE [Part::FeaturePython] Screw168  label="M5x40-Screw351"  # Fasteners workbench fastener (typed FeaturePython)
  Placement = pos=(412.82,192.252,164.814) rot=(1,0,0;1.5708rad)
  diameter = 6
  invert = true
  leftHanded = false
  length = 9
  lengthCustom = 40
  matchOuter = false
  offset = 0
  thread = false
  type = 33
FEATURE [Part::FeaturePython] Screw169  label="M5x40-Screw356"  # Fasteners workbench fastener (typed FeaturePython)
  Placement = pos=(412.38,192.35,125.61) rot=(1,0,0;1.5708rad)
  diameter = 6
  invert = true
  leftHanded = false
  length = 9
  lengthCustom = 40
  matchOuter = false
  offset = 0
  thread = false
  type = 33
FEATURE [Part::FeaturePython] Screw170  label="M5x40-Screw355"  # Fasteners workbench fastener (typed FeaturePython)
  Placement = pos=(474.88,192.331,125.61) rot=(1,0,0;1.5708rad)
  diameter = 6
  invert = true
  leftHanded = false
  length = 9
  lengthCustom = 40
  matchOuter = false
  offset = 0
  thread = false
  type = 33
FEATURE [Part::FeaturePython] Nut068  label="M3-Nut590"  # Fasteners workbench fastener (typed FeaturePython)
  Placement = pos=(402.38,226.287,146.5) rot=(-0.707107,0.707107,0;3.14159rad)
  diameter = 4
  invert = false
  leftHanded = false
  matchOuter = false
  offset = 0
  thread = false
  type = 4
FEATURE [Part::FeaturePython] Nut069  label="M3-Nut591"  # Fasteners workbench fastener (typed FeaturePython)
  Placement = pos=(485.08,226.287,146.5) rot=(-0.707107,0.707107,0;3.14159rad)
  diameter = 4
  invert = false
  leftHanded = false
  matchOuter = false
  offset = 0
  thread = false
  type = 4
FEATURE [Part::FeaturePython] Nut070  label="M3-Nut592"  # Fasteners workbench fastener (typed FeaturePython)
  Placement = pos=(484.881,192.653,146.5) rot=(-0.707107,0.707107,0;3.14159rad)
  diameter = 4
  invert = false
  leftHanded = false
  matchOuter = false
  offset = 0
  thread = false
  type = 4
FEATURE [Part::FeaturePython] Nut071  label="M3-Nut593"  # Fasteners workbench fastener (typed FeaturePython)
  Placement = pos=(402.381,192.653,146.5) rot=(-0.707107,0.707107,0;3.14159rad)
  diameter = 4
  invert = false
  leftHanded = false
  matchOuter = false
  offset = 0
  thread = false
  type = 4
FEATURE [Part::FeaturePython] Screw171  label="M3x14-Screw200"  # Fasteners workbench fastener (typed FeaturePython)
  Placement = pos=(466.574,236.252,118.069) rot=(0,0.707107,0.707107;3.14159rad)
  baseObject = -> b_FDM_0014_down_camera_mount_001_ [Edge38]
  diameter = 1
  invert = false
  leftHanded = false
  length = 9
  lengthCustom = 14
  matchOuter = false
  offset = 0
  thread = false
  type = 39
FEATURE [Part::FeaturePython] Nut077  label="M3-Nut530"  # Fasteners workbench fastener (typed FeaturePython)
  Placement = pos=(421.319,226.18,118.324) rot=(0,0.707107,0.707107;3.14159rad)
  diameter = 4
  invert = false
  leftHanded = false
  matchOuter = false
  offset = 0
  thread = false
  type = 7
FEATURE [Part::FeaturePython] Nut079  label="M3-Nut531"  # Fasteners workbench fastener (typed FeaturePython)
  Placement = pos=(466.319,226.18,118.32) rot=(0.186157,0.694747,0.694747;3.50969rad)
  diameter = 4
  invert = false
  leftHanded = false
  matchOuter = false
  offset = 0
  thread = false
  type = 7
FEATURE [Part::FeaturePython] b_OTS_0011_v_slot_roller1_001_  label="vslot-roller009"  # a2plus imported part (geometry in sourceFile) (typed FeaturePython)
  Placement = pos=(477.879,210.523,140.88) rot=(0,-1,0;1.5708rad)
  a2p_Version = V0.1
  fixedPosition = false
  objectType = a2pPart
  sourceFile = ./MISC/vslot-roller.step
  sourcePart = vslot-roller
  subassemblyImport = false
  timeLastImport = 1.66119e+09
  updateColors = true
FEATURE [Part::FeaturePython] b_M5_tslot_nut1_001_008  label="M5-tslot-nut002"  # a2plus imported part (geometry in sourceFile) (typed FeaturePython)
  Placement = pos=(9.94821,-70.1584,105.165) rot=(0,0,1;1.5708rad)
  Visibility1 = true
  a2p_Version = V0.1
  fixedPosition = false
  objectType = a2pPart
  sourceFile = ./FST/M5-tslot-nut.step
  sourcePart = M5-tslot-nut
  subassemblyImport = false
  timeLastImport = 1.66119e+09
  updateColors = true
FEATURE [Part::FeaturePython] Nut048  label="M3-Nut464"  # Fasteners workbench fastener (typed FeaturePython)
  Placement = pos=(24.9656,-93.169,99.99) rot=(0.57735,-0.57735,0.57735;2.0944rad)
  Visibility1 = true
  diameter = 4
  invert = false
  leftHanded = false
  matchOuter = false
  offset = 0
  thread = false
  type = 7
FEATURE [Part::FeaturePython] Nut045  label="M5-Nut625"  # Fasteners workbench fastener (typed FeaturePython)
  Placement = pos=(-5.03877,-97.4915,83.9035) rot=(0.866025,0.5,0;3.14159rad)
  Visibility1 = true
  diameter = 3
  invert = false
  leftHanded = false
  matchOuter = false
  offset = 0
  thread = false
  type = 5
FEATURE [Part::FeaturePython] b_Gates_2GT_20T_Toothed_Idler1_001_001  label="GT2-idler002"  # a2plus imported part (geometry in sourceFile) (typed FeaturePython)
  Placement = pos=(10.0586,-97.7236,95.0003) rot=(0.57735,-0.57735,-0.57735;2.0944rad)
  Visibility1 = true
  a2p_Version = V0.1
  fixedPosition = false
  objectType = a2pPart
  sourceFile = ./cad/MISC/GT2-idler.STEP
  sourcePart = GT2-idler
  subassemblyImport = false
  timeLastImport = 1.64563e+09
  updateColors = true
FEATURE [Part::FeaturePython] Nut033  label="M5-Nut626"  # Fasteners workbench fastener (typed FeaturePython)
  Placement = pos=(9.97594,-97.5692,89.9635) rot=(0.707107,0.707107,0;3.14159rad)
  Visibility1 = true
  diameter = 3
  invert = false
  leftHanded = false
  matchOuter = false
  offset = 0
  thread = false
  type = 5
FEATURE [Part::FeaturePython] Screw052  label="M3x16-Screw085"  # Fasteners workbench fastener (typed FeaturePython)
  Placement = pos=(24.99,-102.16,100) rot=(0.57735,-0.57735,0.57735;2.0944rad)
  Visibility1 = true
  diameter = 4
  invert = false
  leftHanded = false
  length = 6
  lengthCustom = 16
  matchOuter = false
  offset = 0
  thread = false
  type = 33
FEATURE [Part::FeaturePython] Screw053  label="M5x10-Screw334"  # Fasteners workbench fastener (typed FeaturePython)
  Placement = pos=(9.89,-70.16,114.96) rot=(0,0,-1;1.5708rad)
  Visibility1 = true
  diameter = 6
  invert = false
  leftHanded = false
  length = 1
  lengthCustom = 10
  matchOuter = false
  offset = 0
  thread = false
  type = 33
FEATURE [Part::FeaturePython] Screw054  label="M5x25-Screw127"  # Fasteners workbench fastener (typed FeaturePython)
  Placement = pos=(9.99,-97.57,109.98) rot=(0,0,-1;1.5708rad)
  Visibility1 = true
  diameter = 6
  invert = false
  leftHanded = false
  length = 6
  lengthCustom = 25
  matchOuter = false
  offset = 0
  thread = false
  type = 33
FEATURE [Part::FeaturePython] Screw035  label="M5x10-Screw335"  # Fasteners workbench fastener (typed FeaturePython)
  Placement = pos=(-4.92,-45.15,30.1) rot=(0.57735,-0.57735,-0.57735;2.0944rad)
  Visibility1 = true
  diameter = 6
  invert = false
  leftHanded = false
  length = 1
  lengthCustom = 10
  matchOuter = false
  offset = 0
  thread = false
  type = 33
FEATURE [Part::FeaturePython] Screw036  label="M5x10-Screw336"  # Fasteners workbench fastener (typed FeaturePython)
  Placement = pos=(-4.92,-70.14,30.1) rot=(0.57735,-0.57735,-0.57735;2.0944rad)
  Visibility1 = true
  diameter = 6
  invert = false
  leftHanded = false
  length = 1
  lengthCustom = 10
  matchOuter = false
  offset = 0
  thread = false
  type = 33
FEATURE [Part::FeaturePython] Screw037  label="M5x10-Screw337"  # Fasteners workbench fastener (typed FeaturePython)
  Placement = pos=(9.96,-25.33,9.99) rot=(1,0,0;1.5708rad)
  Visibility1 = true
  diameter = 6
  invert = false
  leftHanded = false
  length = 1
  lengthCustom = 10
  matchOuter = false
  offset = 0
  thread = false
  type = 33
FEATURE [Part::FeaturePython] Screw051  label="M5x40-Screw344"  # Fasteners workbench fastener (typed FeaturePython)
  Placement = pos=(-4.98,-97.58,119.74) rot=(0,0,-1;1.5708rad)
  Visibility1 = true
  diameter = 6
  invert = false
  leftHanded = false
  length = 12
  lengthCustom = 40
  matchOuter = false
  offset = 0
  thread = false
  type = 33
FEATURE [Part::FeaturePython] b_M5_tslot_nut1_001_009  label="M5-tslot-nut003"  # a2plus imported part (geometry in sourceFile) (typed FeaturePython)
  Placement = pos=(4.76821,-70.1584,30.1746) rot=(0.57735,0.57735,-0.57735;4.18879rad)
  Visibility1 = true
  a2p_Version = V0.1
  fixedPosition = false
  objectType = a2pPart
  sourceFile = ./FST/M5-tslot-nut.step
  sourcePart = M5-tslot-nut
  subassemblyImport = false
  timeLastImport = 1.66119e+09
  updateColors = true
FEATURE [Part::FeaturePython] b_M5_tslot_nut1_001_010  label="M5-tslot-nut004"  # a2plus imported part (geometry in sourceFile) (typed FeaturePython)
  Placement = pos=(4.76821,-45.2084,30.1746) rot=(0.57735,0.57735,-0.57735;4.18879rad)
  Visibility1 = true
  a2p_Version = V0.1
  fixedPosition = false
  objectType = a2pPart
  sourceFile = ./FST/M5-tslot-nut.step
  sourcePart = M5-tslot-nut
  subassemblyImport = false
  timeLastImport = 1.66119e+09
  updateColors = true
FEATURE [Part::FeaturePython] b_M5_tslot_nut1_001_011  label="M5-tslot-nut005"  # a2plus imported part (geometry in sourceFile) (typed FeaturePython)
  Placement = pos=(9.85821,-15.0384,9.95457) rot=(0,0.707107,-0.707107;3.14159rad)
  Visibility1 = true
  a2p_Version = V0.1
  fixedPosition = false
  objectType = a2pPart
  sourceFile = ./FST/M5-tslot-nut.step
  sourcePart = M5-tslot-nut
  subassemblyImport = false
  timeLastImport = 1.66119e+09
  updateColors = true
FEATURE [Part::FeaturePython] b_FDM_0001_front_left_leg_001_  label="front-left-leg"  # a2plus imported part (geometry in sourceFile) (typed FeaturePython)
  Placement = pos=(19.9755,-0.0519684,19.9889) rot=(0.57735,-0.57735,-0.57735;2.0944rad)
  Visibility1 = true
  a2p_Version = 0.4.60i
  fixedPosition = false
  objectType = a2pPart
  sourceFile = ./FDM/front-left-leg.FCStd
  sourcePart = Body
  subassemblyImport = false
  timeLastImport = 1.6766e+09
  updateColors = true
FEATURE [Part::FeaturePython] Screw061  label="M5x40-Screw345"  # Fasteners workbench fastener (typed FeaturePython)
  Placement = pos=(605.12,-97.58,119.74) rot=(0,0,-1;1.5708rad)
  Visibility1 = true
  diameter = 6
  invert = false
  leftHanded = false
  length = 12
  lengthCustom = 40
  matchOuter = false
  offset = 0
  thread = false
  type = 33
FEATURE [Part::FeaturePython] b_Gates_2GT_20T_Toothed_Idler1_001_003  label="GT2-idler003"  # a2plus imported part (geometry in sourceFile) (typed FeaturePython)
  Placement = pos=(590.059,-97.7236,95.0003) rot=(0.57735,-0.57735,-0.57735;2.0944rad)
  Visibility1 = true
  a2p_Version = V0.1
  fixedPosition = false
  objectType = a2pPart
  sourceFile = ./cad/MISC/GT2-idler.STEP
  sourcePart = GT2-idler
  subassemblyImport = false
  timeLastImport = 1.64563e+09
  updateColors = true
FEATURE [Part::FeaturePython] Nut046  label="M5-Nut627"  # Fasteners workbench fastener (typed FeaturePython)
  Placement = pos=(605.043,-97.4581,83.9035) rot=(0.866025,0.5,0;3.14159rad)
  Visibility1 = true
  diameter = 3
  invert = false
  leftHanded = false
  matchOuter = false
  offset = 0
  thread = false
  type = 5
FEATURE [Part::FeaturePython] Screw062  label="M5x25-Screw128"  # Fasteners workbench fastener (typed FeaturePython)
  Placement = pos=(590.06,-97.57,109.98) rot=(0,0,-1;1.5708rad)
  Visibility1 = true
  diameter = 6
  invert = false
  leftHanded = false
  length = 6
  lengthCustom = 25
  matchOuter = false
  offset = 0
  thread = false
  type = 33
FEATURE [Part::FeaturePython] Nut047  label="M5-Nut628"  # Fasteners workbench fastener (typed FeaturePython)
  Placement = pos=(590.046,-97.5092,89.9635) rot=(0.707107,0.707107,0;3.14159rad)
  Visibility1 = true
  diameter = 3
  invert = false
  leftHanded = false
  matchOuter = false
  offset = 0
  thread = false
  type = 5
FEATURE [Part::FeaturePython] Screw063  label="M3x16-Screw086"  # Fasteners workbench fastener (typed FeaturePython)
  Placement = pos=(574.97,-101,100) rot=(0.57735,-0.57735,0.57735;2.0944rad)
  Visibility1 = true
  diameter = 4
  invert = false
  leftHanded = false
  length = 6
  lengthCustom = 16
  matchOuter = false
  offset = 0
  thread = false
  type = 33
FEATURE [Part::FeaturePython] Nut049  label="M3-Nut465"  # Fasteners workbench fastener (typed FeaturePython)
  Placement = pos=(575.026,-93.169,99.99) rot=(0.57735,-0.57735,0.57735;2.0944rad)
  Visibility1 = true
  diameter = 4
  invert = false
  leftHanded = false
  matchOuter = false
  offset = 0
  thread = false
  type = 7
FEATURE [Part::FeaturePython] Screw064  label="M5x10-Screw338"  # Fasteners workbench fastener (typed FeaturePython)
  Placement = pos=(590.19,-70.16,114.96) rot=(0,0,-1;1.5708rad)
  Visibility1 = true
  diameter = 6
  invert = false
  leftHanded = false
  length = 1
  lengthCustom = 10
  matchOuter = false
  offset = 0
  thread = false
  type = 33
FEATURE [Part::FeaturePython] Screw070  label="M5x10-Screw339"  # Fasteners workbench fastener (typed FeaturePython)
  Placement = pos=(605,-70,29.99) rot=(0.57735,-0.57735,0.57735;4.18879rad)
  Visibility1 = true
  diameter = 6
  invert = false
  leftHanded = false
  length = 1
  lengthCustom = 10
  matchOuter = false
  offset = 0
  thread = false
  type = 33
FEATURE [Part::FeaturePython] Screw071  label="M5x10-Screw340"  # Fasteners workbench fastener (typed FeaturePython)
  Placement = pos=(605,-44.99,29.99) rot=(0.57735,-0.57735,0.57735;4.18879rad)
  Visibility1 = true
  diameter = 6
  invert = false
  leftHanded = false
  length = 1
  lengthCustom = 10
  matchOuter = false
  offset = 0
  thread = false
  type = 33
FEATURE [Part::FeaturePython] Screw072  label="M5x10-Screw341"  # Fasteners workbench fastener (typed FeaturePython)
  Placement = pos=(589.91,-24.98,10.2) rot=(0,0.707107,-0.707107;3.14159rad)
  Visibility1 = true
  diameter = 6
  invert = false
  leftHanded = false
  length = 1
  lengthCustom = 10
  matchOuter = false
  offset = 0
  thread = false
  type = 33
FEATURE [Part::FeaturePython] b_M5_tslot_nut1_001_012  label="M5-tslot-nut006"  # a2plus imported part (geometry in sourceFile) (typed FeaturePython)
  Placement = pos=(590.068,-15.0384,10.1446) rot=(0,0.707107,-0.707107;3.14159rad)
  Visibility1 = true
  a2p_Version = V0.1
  fixedPosition = false
  objectType = a2pPart
  sourceFile = ./FST/M5-tslot-nut.step
  sourcePart = M5-tslot-nut
  subassemblyImport = false
  timeLastImport = 1.66119e+09
  updateColors = true
FEATURE [Part::FeaturePython] b_M5_tslot_nut1_001_013  label="M5-tslot-nut007"  # a2plus imported part (geometry in sourceFile) (typed FeaturePython)
  Placement = pos=(595.208,-70.0184,30.1846) rot=(0.57735,-0.57735,0.57735;4.18879rad)
  Visibility1 = true
  a2p_Version = V0.1
  fixedPosition = false
  objectType = a2pPart
  sourceFile = ./FST/M5-tslot-nut.step
  sourcePart = M5-tslot-nut
  subassemblyImport = false
  timeLastImport = 1.66119e+09
  updateColors = true
FEATURE [Part::FeaturePython] b_M5_tslot_nut1_001_014  label="M5-tslot-nut008"  # a2plus imported part (geometry in sourceFile) (typed FeaturePython)
  Placement = pos=(595.208,-44.9784,30.1846) rot=(0.57735,-0.57735,0.57735;4.18879rad)
  Visibility1 = true
  a2p_Version = V0.1
  fixedPosition = false
  objectType = a2pPart
  sourceFile = ./FST/M5-tslot-nut.step
  sourcePart = M5-tslot-nut
  subassemblyImport = false
  timeLastImport = 1.66119e+09
  updateColors = true
FEATURE [Part::FeaturePython] b_M5_tslot_nut1_001_015  label="M5-tslot-nut009"  # a2plus imported part (geometry in sourceFile) (typed FeaturePython)
  Placement = pos=(589.988,-70.0484,105.085) rot=(0,0,-1;1.5708rad)
  Visibility1 = true
  a2p_Version = V0.1
  fixedPosition = false
  objectType = a2pPart
  sourceFile = ./FST/M5-tslot-nut.step
  sourcePart = M5-tslot-nut
  subassemblyImport = false
  timeLastImport = 1.66119e+09
  updateColors = true
FEATURE [Part::FeaturePython] Screw089  label="M3x8-Screw462"  # Fasteners workbench fastener (typed FeaturePython)
  Placement = pos=(-5.54,531.08,85.24) rot=(0,0,-1;1.5708rad)
  Visibility1 = true
  diameter = 1
  invert = false
  leftHanded = false
  length = 1
  lengthCustom = 8
  matchOuter = false
  offset = 0
  thread = false
  type = 39
FEATURE [Part::FeaturePython] Screw090  label="M3x8-Screw463"  # Fasteners workbench fastener (typed FeaturePython)
  Placement = pos=(-5.54,562.08,85.24) rot=(0,0,1;0rad)
  Visibility1 = true
  diameter = 1
  invert = false
  leftHanded = false
  length = 1
  lengthCustom = 8
  matchOuter = false
  offset = 0
  thread = false
  type = 39
FEATURE [Part::FeaturePython] Screw091  label="M3x8-Screw464"  # Fasteners workbench fastener (typed FeaturePython)
  Placement = pos=(25.34,562.08,85.14) rot=(0,0,1;3.14159rad)
  Visibility1 = true
  diameter = 1
  invert = false
  leftHanded = false
  length = 1
  lengthCustom = 8
  matchOuter = false
  offset = 0
  thread = false
  type = 39
FEATURE [Part::FeaturePython] Screw092  label="M3x8-Screw465"  # Fasteners workbench fastener (typed FeaturePython)
  Placement = pos=(25.34,531.13,85.19) rot=(0,0,-1;1.5708rad)
  Visibility1 = true
  diameter = 1
  invert = false
  leftHanded = false
  length = 1
  lengthCustom = 8
  matchOuter = false
  offset = 0
  thread = false
  type = 39
FEATURE [Part::FeaturePython] b_Nema_17_42A02C_v21_001_002  label="NEMA17-stepper003"  # a2plus imported part (geometry in sourceFile) (typed FeaturePython)
  Placement = pos=(9.84,546.54,90.25) rot=(0,0,1;0rad)
  Visibility1 = true
  a2p_Version = V0.1
  fixedPosition = false
  objectType = a2pPart
  sourceFile = ./MISC/NEMA17-stepper.step 
  sourcePart = NEMA17-stepper
  subassemblyImport = false
  timeLastImport = 1.64563e+09
  updateColors = true
FEATURE [Part::FeaturePython] b_Gates_2GT_20T_Toothed_Pulley1_001_002  label="GT2-pulley002"  # a2plus imported part (geometry in sourceFile) (typed FeaturePython)
  Placement = pos=(9.82,546.52,88.82) rot=(0.57735,0.57735,0.57735;2.0944rad)
  Visibility1 = true
  a2p_Version = V0.1
  fixedPosition = false
  objectType = a2pPart
  sourceFile = ./cad/MISC/GT2-pulley.STEP
  sourcePart = GT2-pulley
  subassemblyImport = false
  timeLastImport = 1.64563e+09
  updateColors = true
FEATURE [Part::FeaturePython] Screw029  label="M5x10-Screw342"  # Fasteners workbench fastener (typed FeaturePython)
  Placement = pos=(9.89,510.06,115.05) rot=(0,0,-1;1.5708rad)
  Visibility1 = true
  diameter = 6
  invert = false
  leftHanded = false
  length = 1
  lengthCustom = 10
  matchOuter = false
  offset = 0
  thread = false
  type = 33
FEATURE [Part::FeaturePython] Screw030  label="M5x10-Screw343"  # Fasteners workbench fastener (typed FeaturePython)
  Placement = pos=(-6.57,510.06,30.11) rot=(0.57735,-0.57735,-0.57735;2.0944rad)
  Visibility1 = true
  diameter = 6
  invert = false
  leftHanded = false
  length = 1
  lengthCustom = 10
  matchOuter = false
  offset = 0
  thread = false
  type = 33
FEATURE [Part::FeaturePython] Screw031  label="M5x10-Screw344"  # Fasteners workbench fastener (typed FeaturePython)
  Placement = pos=(26.33,510.06,30.11) rot=(0.57735,-0.57735,0.57735;4.18879rad)
  Visibility1 = true
  diameter = 6
  invert = false
  leftHanded = false
  length = 1
  lengthCustom = 10
  matchOuter = false
  offset = 0
  thread = false
  type = 33
FEATURE [Part::FeaturePython] b_M5_tslot_nut1_001_002  label="M5-tslot-nut010"  # a2plus imported part (geometry in sourceFile) (typed FeaturePython)
  Placement = pos=(9.95821,510.062,105.175) rot=(0,0,-1;1.5708rad)
  Visibility1 = true
  a2p_Version = V0.1
  fixedPosition = false
  objectType = a2pPart
  sourceFile = ./FST/M5-tslot-nut.step
  sourcePart = M5-tslot-nut
  subassemblyImport = false
  timeLastImport = 1.66119e+09
  updateColors = true
FEATURE [Part::FeaturePython] b_M5_tslot_nut1_001_003  label="M5-tslot-nut011"  # a2plus imported part (geometry in sourceFile) (typed FeaturePython)
  Placement = pos=(4.86821,510.062,30.0846) rot=(0.57735,-0.57735,-0.57735;2.0944rad)
  Visibility1 = true
  a2p_Version = V0.1
  fixedPosition = false
  objectType = a2pPart
  sourceFile = ./FST/M5-tslot-nut.step
  sourcePart = M5-tslot-nut
  subassemblyImport = false
  timeLastImport = 1.66119e+09
  updateColors = true
FEATURE [Part::FeaturePython] b_M5_tslot_nut1_001_004  label="M5-tslot-nut012"  # a2plus imported part (geometry in sourceFile) (typed FeaturePython)
  Placement = pos=(14.8982,510.062,30.0846) rot=(0.57735,-0.57735,0.57735;4.18879rad)
  Visibility1 = true
  a2p_Version = V0.1
  fixedPosition = false
  objectType = a2pPart
  sourceFile = ./FST/M5-tslot-nut.step
  sourcePart = M5-tslot-nut
  subassemblyImport = false
  timeLastImport = 1.66119e+09
  updateColors = true
FEATURE [Part::FeaturePython] b_Gates_2GT_20T_Toothed_Pulley1_001_003  label="GT2-pulley003"  # a2plus imported part (geometry in sourceFile) (typed FeaturePython)
  Placement = pos=(590.02,546.519,111.281) rot=(0.57735,0.57735,-0.57735;4.18879rad)
  Visibility1 = true
  a2p_Version = V0.1
  fixedPosition = false
  objectType = a2pPart
  sourceFile = ./cad/MISC/GT2-pulley.STEP
  sourcePart = GT2-pulley
  subassemblyImport = false
  timeLastImport = 1.64563e+09
  updateColors = true
FEATURE [Part::FeaturePython] Screw096  label="M3x8-Screw466"  # Fasteners workbench fastener (typed FeaturePython)
  Placement = pos=(574.58,531.04,85.25) rot=(0,0,-1;1.5708rad)
  Visibility1 = true
  diameter = 1
  invert = false
  leftHanded = false
  length = 1
  lengthCustom = 8
  matchOuter = false
  offset = 0
  thread = false
  type = 39
FEATURE [Part::FeaturePython] Screw093  label="M3x8-Screw467"  # Fasteners workbench fastener (typed FeaturePython)
  Placement = pos=(574.58,562.04,85.25) rot=(0,0,-1;1.5708rad)
  Visibility1 = true
  diameter = 1
  invert = false
  leftHanded = false
  length = 1
  lengthCustom = 8
  matchOuter = false
  offset = 0
  thread = false
  type = 39
FEATURE [Part::FeaturePython] Screw094  label="M3x8-Screw468"  # Fasteners workbench fastener (typed FeaturePython)
  Placement = pos=(605.58,562.04,85.25) rot=(0,0,-1;1.5708rad)
  Visibility1 = true
  diameter = 1
  invert = false
  leftHanded = false
  length = 1
  lengthCustom = 8
  matchOuter = false
  offset = 0
  thread = false
  type = 39
FEATURE [Part::FeaturePython] Screw095  label="M3x8-Screw469"  # Fasteners workbench fastener (typed FeaturePython)
  Placement = pos=(605.58,531.04,85.25) rot=(0,0,-1;1.5708rad)
  Visibility1 = true
  diameter = 1
  invert = false
  leftHanded = false
  length = 1
  lengthCustom = 8
  matchOuter = false
  offset = 0
  thread = false
  type = 39
FEATURE [Part::FeaturePython] b_Nema_17_42A02C_v21_001_003  label="NEMA17-stepper004"  # a2plus imported part (geometry in sourceFile) (typed FeaturePython)
  Placement = pos=(590.08,546.54,90.25) rot=(0,0,1;0rad)
  Visibility1 = true
  a2p_Version = V0.1
  fixedPosition = false
  objectType = a2pPart
  sourceFile = ./MISC/NEMA17-stepper.step 
  sourcePart = NEMA17-stepper
  subassemblyImport = false
  timeLastImport = 1.64563e+09
  updateColors = true
FEATURE [Part::FeaturePython] Screw032  label="M5x10-Screw345"  # Fasteners workbench fastener (typed FeaturePython)
  Placement = pos=(606.44,510.06,30.11) rot=(0.57735,-0.57735,0.57735;4.18879rad)
  Visibility1 = true
  diameter = 6
  invert = false
  leftHanded = false
  length = 1
  lengthCustom = 10
  matchOuter = false
  offset = 0
  thread = false
  type = 33
FEATURE [Part::FeaturePython] Screw033  label="M5x10-Screw346"  # Fasteners workbench fastener (typed FeaturePython)
  Placement = pos=(573.54,510.06,30.11) rot=(0.57735,-0.57735,-0.57735;2.0944rad)
  Visibility1 = true
  diameter = 6
  invert = false
  leftHanded = false
  length = 1
  lengthCustom = 10
  matchOuter = false
  offset = 0
  thread = false
  type = 33
FEATURE [Part::FeaturePython] Screw034  label="M5x10-Screw347"  # Fasteners workbench fastener (typed FeaturePython)
  Placement = pos=(589.94,510.06,115.05) rot=(0,0,-1;1.5708rad)
  Visibility1 = true
  diameter = 6
  invert = false
  leftHanded = false
  length = 1
  lengthCustom = 10
  matchOuter = false
  offset = 0
  thread = false
  type = 33
FEATURE [Part::FeaturePython] b_M5_tslot_nut1_001_007  label="M5-tslot-nut013"  # a2plus imported part (geometry in sourceFile) (typed FeaturePython)
  Placement = pos=(595.338,510.062,30.0846) rot=(0.57735,-0.57735,0.57735;4.18879rad)
  Visibility1 = true
  a2p_Version = V0.1
  fixedPosition = false
  objectType = a2pPart
  sourceFile = ./FST/M5-tslot-nut.step
  sourcePart = M5-tslot-nut
  subassemblyImport = false
  timeLastImport = 1.66119e+09
  updateColors = true
FEATURE [Part::FeaturePython] b_M5_tslot_nut1_001_006  label="M5-tslot-nut014"  # a2plus imported part (geometry in sourceFile) (typed FeaturePython)
  Placement = pos=(585.028,510.062,30.0846) rot=(0.57735,-0.57735,-0.57735;2.0944rad)
  Visibility1 = true
  a2p_Version = V0.1
  fixedPosition = false
  objectType = a2pPart
  sourceFile = ./FST/M5-tslot-nut.step
  sourcePart = M5-tslot-nut
  subassemblyImport = false
  timeLastImport = 1.66119e+09
  updateColors = true
FEATURE [Part::FeaturePython] b_M5_tslot_nut1_001_005  label="M5-tslot-nut015"  # a2plus imported part (geometry in sourceFile) (typed FeaturePython)
  Placement = pos=(590.098,510.062,105.175) rot=(0,0,-1;1.5708rad)
  Visibility1 = true
  a2p_Version = V0.1
  fixedPosition = false
  objectType = a2pPart
  sourceFile = ./FST/M5-tslot-nut.step
  sourcePart = M5-tslot-nut
  subassemblyImport = false
  timeLastImport = 1.66119e+09
  updateColors = true
FEATURE [Part::FeaturePython] b_M5_tslot_nut1_001_028  label="M5-tslot-nut016"  # a2plus imported part (geometry in sourceFile) (typed FeaturePython)
  Placement = pos=(10.0282,139.79,24.9946) rot=(0.707107,0.707107,0;3.14159rad)
  Visibility1 = true
  a2p_Version = V0.1
  fixedPosition = false
  objectType = a2pPart
  sourceFile = ./FST/M5-tslot-nut.step
  sourcePart = M5-tslot-nut
  subassemblyImport = false
  timeLastImport = 1.66119e+09
  updateColors = true
FEATURE [Part::FeaturePython] b_M5_tslot_nut1_001_029  label="M5-tslot-nut017"  # a2plus imported part (geometry in sourceFile) (typed FeaturePython)
  Placement = pos=(10.0282,82.6716,24.9946) rot=(0.707107,0.707107,0;3.14159rad)
  Visibility1 = true
  a2p_Version = V0.1
  fixedPosition = false
  objectType = a2pPart
  sourceFile = ./FST/M5-tslot-nut.step
  sourcePart = M5-tslot-nut
  subassemblyImport = false
  timeLastImport = 1.66119e+09
  updateColors = true
FEATURE [Part::FeaturePython] Screw103  label="M5x10-Screw348"  # Fasteners workbench fastener (typed FeaturePython)
  Placement = pos=(9.98,137.73,14.98) rot=(0.707107,-0.707107,0;3.14159rad)
  Visibility1 = true
  diameter = 6
  invert = false
  leftHanded = false
  length = 1
  lengthCustom = 10
  matchOuter = false
  offset = 0
  thread = false
  type = 33
FEATURE [Part::FeaturePython] Screw104  label="M5x10-Screw349"  # Fasteners workbench fastener (typed FeaturePython)
  Placement = pos=(9.98,82.71,14.98) rot=(0.707107,-0.707107,0;3.14159rad)
  Visibility1 = true
  diameter = 6
  invert = false
  leftHanded = false
  length = 1
  lengthCustom = 10
  matchOuter = false
  offset = 0
  thread = false
  type = 33
FEATURE [Part::FeaturePython] b_M5_tslot_nut1_001_024  label="M5-tslot-nut018"  # a2plus imported part (geometry in sourceFile) (typed FeaturePython)
  Placement = pos=(589.918,420.022,24.9746) rot=(0.707107,-0.707107,0;3.14159rad)
  Visibility1 = true
  a2p_Version = V0.1
  fixedPosition = false
  objectType = a2pPart
  sourceFile = ./FST/M5-tslot-nut.step
  sourcePart = M5-tslot-nut
  subassemblyImport = false
  timeLastImport = 1.66119e+09
  updateColors = true
FEATURE [Part::FeaturePython] b_M5_tslot_nut1_001_025  label="M5-tslot-nut019"  # a2plus imported part (geometry in sourceFile) (typed FeaturePython)
  Placement = pos=(589.918,435.152,9.95457) rot=(0,0.707107,-0.707107;3.14159rad)
  Visibility1 = true
  a2p_Version = V0.1
  fixedPosition = false
  objectType = a2pPart
  sourceFile = ./FST/M5-tslot-nut.step
  sourcePart = M5-tslot-nut
  subassemblyImport = false
  timeLastImport = 1.66119e+09
  updateColors = true
FEATURE [Part::FeaturePython] b_M5_tslot_nut1_001_026  label="M5-tslot-nut020"  # a2plus imported part (geometry in sourceFile) (typed FeaturePython)
  Placement = pos=(589.918,445.002,9.95457) rot=(0,0.707107,0.707107;3.14159rad)
  Visibility1 = true
  a2p_Version = V0.1
  fixedPosition = false
  objectType = a2pPart
  sourceFile = ./FST/M5-tslot-nut.step
  sourcePart = M5-tslot-nut
  subassemblyImport = false
  timeLastImport = 1.66119e+09
  updateColors = true
FEATURE [Part::FeaturePython] b_M5_tslot_nut1_001_027  label="M5-tslot-nut021"  # a2plus imported part (geometry in sourceFile) (typed FeaturePython)
  Placement = pos=(589.918,460.122,25.0246) rot=(0.707107,0.707107,0;3.14159rad)
  Visibility1 = true
  a2p_Version = V0.1
  fixedPosition = false
  objectType = a2pPart
  sourceFile = ./FST/M5-tslot-nut.step
  sourcePart = M5-tslot-nut
  subassemblyImport = false
  timeLastImport = 1.66119e+09
  updateColors = true
FEATURE [Part::FeaturePython] Screw081  label="M5x8-Screw220"  # Fasteners workbench fastener (typed FeaturePython)
  Placement = pos=(589.97,453.15,9.91) rot=(0,0.707107,0.707107;3.14159rad)
  Visibility1 = true
  diameter = 3
  invert = false
  leftHanded = false
  length = 0
  lengthCustom = 8
  matchOuter = false
  offset = 0
  thread = false
  type = 39
FEATURE [Part::FeaturePython] Screw082  label="M5x8-Screw221"  # Fasteners workbench fastener (typed FeaturePython)
  Placement = pos=(589.97,426.99,9.91) rot=(0,0.707107,-0.707107;3.14159rad)
  Visibility1 = true
  diameter = 3
  invert = false
  leftHanded = false
  length = 0
  lengthCustom = 8
  matchOuter = false
  offset = 0
  thread = false
  type = 39
FEATURE [Part::FeaturePython] Screw083  label="M5x8-Screw222"  # Fasteners workbench fastener (typed FeaturePython)
  Placement = pos=(589.88,419.96,16.93) rot=(0,1,0;3.14159rad)
  Visibility1 = true
  diameter = 3
  invert = false
  leftHanded = false
  length = 0
  lengthCustom = 8
  matchOuter = false
  offset = 0
  thread = false
  type = 39
FEATURE [Part::FeaturePython] Screw084  label="M5x8-Screw223"  # Fasteners workbench fastener (typed FeaturePython)
  Placement = pos=(589.88,460.14,16.93) rot=(0,1,0;3.14159rad)
  Visibility1 = true
  diameter = 3
  invert = false
  leftHanded = false
  length = 0
  lengthCustom = 8
  matchOuter = false
  offset = 0
  thread = false
  type = 39
FEATURE [Part::FeaturePython] Screw077  label="M5x8-Screw224"  # Fasteners workbench fastener (typed FeaturePython)
  Placement = pos=(10.02,453.15,9.97) rot=(0,0.707107,0.707107;3.14159rad)
  Visibility1 = true
  diameter = 3
  invert = false
  leftHanded = false
  length = 0
  lengthCustom = 8
  matchOuter = false
  offset = 0
  thread = false
  type = 39
FEATURE [Part::FeaturePython] Screw078  label="M5x8-Screw225"  # Fasteners workbench fastener (typed FeaturePython)
  Placement = pos=(10.02,460.2,16.85) rot=(0,1,0;3.14159rad)
  Visibility1 = true
  diameter = 3
  invert = false
  leftHanded = false
  length = 0
  lengthCustom = 8
  matchOuter = false
  offset = 0
  thread = false
  type = 39
FEATURE [Part::FeaturePython] Screw079  label="M5x8-Screw226"  # Fasteners workbench fastener (typed FeaturePython)
  Placement = pos=(10.02,420.16,16.85) rot=(0,1,0;3.14159rad)
  Visibility1 = true
  diameter = 3
  invert = false
  leftHanded = false
  length = 0
  lengthCustom = 8
  matchOuter = false
  offset = 0
  thread = false
  type = 39
FEATURE [Part::FeaturePython] Screw080  label="M5x8-Screw227"  # Fasteners workbench fastener (typed FeaturePython)
  Placement = pos=(10.02,427.06,9.98) rot=(0,0.707107,-0.707107;3.14159rad)
  Visibility1 = true
  diameter = 3
  invert = false
  leftHanded = false
  length = 0
  lengthCustom = 8
  matchOuter = false
  offset = 0
  thread = false
  type = 39
FEATURE [Part::FeaturePython] b_M5_tslot_nut1_001_020  label="M5-tslot-nut022"  # a2plus imported part (geometry in sourceFile) (typed FeaturePython)
  Placement = pos=(9.70821,435.112,9.95457) rot=(1,0,0;1.5708rad)
  Visibility1 = true
  a2p_Version = V0.1
  fixedPosition = false
  objectType = a2pPart
  sourceFile = ./FST/M5-tslot-nut.step
  sourcePart = M5-tslot-nut
  subassemblyImport = false
  timeLastImport = 1.66119e+09
  updateColors = true
FEATURE [Part::FeaturePython] b_M5_tslot_nut1_001_021  label="M5-tslot-nut023"  # a2plus imported part (geometry in sourceFile) (typed FeaturePython)
  Placement = pos=(9.70821,445.032,9.95457) rot=(-1,0,0;1.5708rad)
  Visibility1 = true
  a2p_Version = V0.1
  fixedPosition = false
  objectType = a2pPart
  sourceFile = ./FST/M5-tslot-nut.step
  sourcePart = M5-tslot-nut
  subassemblyImport = false
  timeLastImport = 1.66119e+09
  updateColors = true
FEATURE [Part::FeaturePython] b_M5_tslot_nut1_001_022  label="M5-tslot-nut024"  # a2plus imported part (geometry in sourceFile) (typed FeaturePython)
  Placement = pos=(9.70821,460.202,25.1246) rot=(0.707107,-0.707107,0;3.14159rad)
  Visibility1 = true
  a2p_Version = V0.1
  fixedPosition = false
  objectType = a2pPart
  sourceFile = ./FST/M5-tslot-nut.step
  sourcePart = M5-tslot-nut
  subassemblyImport = false
  timeLastImport = 1.66119e+09
  updateColors = true
FEATURE [Part::FeaturePython] b_M5_tslot_nut1_001_023  label="M5-tslot-nut025"  # a2plus imported part (geometry in sourceFile) (typed FeaturePython)
  Placement = pos=(9.70821,420.102,25.1246) rot=(0.707107,-0.707107,0;3.14159rad)
  Visibility1 = true
  a2p_Version = V0.1
  fixedPosition = false
  objectType = a2pPart
  sourceFile = ./FST/M5-tslot-nut.step
  sourcePart = M5-tslot-nut
  subassemblyImport = false
  timeLastImport = 1.66119e+09
  updateColors = true
FEATURE [Part::FeaturePython] b_2020CornerBracket1_001_002  label="corner-bracket"  # a2plus imported part (geometry in sourceFile) (typed FeaturePython)
  Placement = pos=(580.008,450.215,19.9154) rot=(0,1,0;3.14159rad)
  Visibility1 = true
  a2p_Version = V0.1
  fixedPosition = false
  objectType = a2pPart
  sourceFile = ./MISC/corner-bracket.step
  sourcePart = corner-bracket
  subassemblyImport = false
  timeLastImport = 1.66119e+09
  updateColors = true
FEATURE [Part::FeaturePython] b_2020CornerBracket1_001_003  label="corner-bracket001"  # a2plus imported part (geometry in sourceFile) (typed FeaturePython)
  Placement = pos=(599.918,430.005,19.9154) rot=(1,0,0;3.14159rad)
  Visibility1 = true
  a2p_Version = V0.1
  fixedPosition = false
  objectType = a2pPart
  sourceFile = ./MISC/corner-bracket.step
  sourcePart = corner-bracket
  subassemblyImport = false
  timeLastImport = 1.66119e+09
  updateColors = true
FEATURE [Part::FeaturePython] b_2020CornerBracket1_001_004  label="corner-bracket002"  # a2plus imported part (geometry in sourceFile) (typed FeaturePython)
  Placement = pos=(20.0179,430.005,19.9154) rot=(1,0,0;3.14159rad)
  Visibility1 = true
  a2p_Version = V0.1
  fixedPosition = false
  objectType = a2pPart
  sourceFile = ./MISC/corner-bracket.step
  sourcePart = corner-bracket
  subassemblyImport = false
  timeLastImport = 1.66119e+09
  updateColors = true
FEATURE [Part::FeaturePython] b_2020CornerBracket1_001_005  label="corner-bracket003"  # a2plus imported part (geometry in sourceFile) (typed FeaturePython)
  Placement = pos=(0.00786224,450.215,19.9154) rot=(0,1,0;3.14159rad)
  Visibility1 = true
  a2p_Version = V0.1
  fixedPosition = false
  objectType = a2pPart
  sourceFile = ./MISC/corner-bracket.step
  sourcePart = corner-bracket
  subassemblyImport = false
  timeLastImport = 1.66119e+09
  updateColors = true
FEATURE [Part::FeaturePython] b_OTS_0009_20x20_v_slot_600mm1_001_006  label="vslot-extrusion-20mmx20mmx600mm006"  # a2plus imported part (geometry in sourceFile) (typed FeaturePython)
  Placement = pos=(1.05e-13,450.07,0) rot=(0.57735,-0.57735,-0.57735;2.0944rad)
  Visibility1 = true
  a2p_Version = V0.1
  fixedPosition = true
  objectType = a2pPart
  sourceFile = ./MISC/vslot-extrusion-20mmx20mmx600mm.step
  sourcePart = vslot-extrusion-20mmx20mmx600mm
  subassemblyImport = false
  timeLastImport = 1.66119e+09
  updateColors = true
FEATURE [Part::FeaturePython] b_2020CornerBracket1_001_001  label="corner-bracket004"  # a2plus imported part (geometry in sourceFile) (typed FeaturePython)
  Placement = pos=(580.008,0.0247107,19.9154) rot=(0,1,0;3.14159rad)
  Visibility1 = true
  a2p_Version = V0.1
  fixedPosition = false
  objectType = a2pPart
  sourceFile = ./MISC/corner-bracket.step
  sourcePart = corner-bracket
  subassemblyImport = false
  timeLastImport = 1.66119e+09
  updateColors = true
FEATURE [Part::FeaturePython] Screw073  label="M5x8-Screw185"  # Fasteners workbench fastener (typed FeaturePython)
  Placement = pos=(10.02,3.07,9.97) rot=(0,0.707107,0.707107;3.14159rad)
  Visibility1 = true
  diameter = 3
  invert = false
  leftHanded = false
  length = 0
  lengthCustom = 8
  matchOuter = false
  offset = 0
  thread = false
  type = 39
FEATURE [Part::FeaturePython] Screw074  label="M5x8-Screw"  # Fasteners workbench fastener (typed FeaturePython)
  Placement = pos=(10.02,10.13,17.05) rot=(0,1,0;3.14159rad)
  Visibility1 = true
  diameter = 3
  invert = false
  leftHanded = false
  length = 0
  lengthCustom = 8
  matchOuter = false
  offset = 0
  thread = false
  type = 39
FEATURE [Part::FeaturePython] b_2020CornerBracket1_001_  label="corner-bracket005"  # a2plus imported part (geometry in sourceFile) (typed FeaturePython)
  Placement = pos=(-0.0521378,0.0247107,20.0654) rot=(0,1,0;3.14159rad)
  Visibility1 = true
  a2p_Version = V0.1
  fixedPosition = false
  objectType = a2pPart
  sourceFile = ./MISC/corner-bracket.step
  sourcePart = corner-bracket
  subassemblyImport = false
  timeLastImport = 1.66119e+09
  updateColors = true
FEATURE [Part::FeaturePython] b_M5_tslot_nut1_001_016  label="M5-tslot-nut026"  # a2plus imported part (geometry in sourceFile) (typed FeaturePython)
  Placement = pos=(9.85821,-4.9684,9.95457) rot=(-1,0,0;1.5708rad)
  Visibility1 = true
  a2p_Version = V0.1
  fixedPosition = false
  objectType = a2pPart
  sourceFile = ./FST/M5-tslot-nut.step
  sourcePart = M5-tslot-nut
  subassemblyImport = false
  timeLastImport = 1.66119e+09
  updateColors = true
FEATURE [Part::FeaturePython] b_M5_tslot_nut1_001_017  label="M5-tslot-nut027"  # a2plus imported part (geometry in sourceFile) (typed FeaturePython)
  Placement = pos=(10.0282,10.1416,24.9946) rot=(0.707107,0.707107,0;3.14159rad)
  Visibility1 = true
  a2p_Version = V0.1
  fixedPosition = false
  objectType = a2pPart
  sourceFile = ./FST/M5-tslot-nut.step
  sourcePart = M5-tslot-nut
  subassemblyImport = false
  timeLastImport = 1.66119e+09
  updateColors = true
FEATURE [Part::FeaturePython] Screw075  label="M5x8-Screw186"  # Fasteners workbench fastener (typed FeaturePython)
  Placement = pos=(589.77,3.07,9.97) rot=(0,0.707107,0.707107;3.14159rad)
  Visibility1 = true
  diameter = 3
  invert = false
  leftHanded = false
  length = 0
  lengthCustom = 8
  matchOuter = false
  offset = 0
  thread = false
  type = 39
FEATURE [Part::FeaturePython] Screw076  label="M5x8-Screw187"  # Fasteners workbench fastener (typed FeaturePython)
  Placement = pos=(589.89,9.87,16.9) rot=(0,1,0;3.14159rad)
  Visibility1 = true
  diameter = 3
  invert = false
  leftHanded = false
  length = 0
  lengthCustom = 8
  matchOuter = false
  offset = 0
  thread = false
  type = 39
FEATURE [Part::FeaturePython] b_M5_tslot_nut1_001_018  label="M5-tslot-nut028"  # a2plus imported part (geometry in sourceFile) (typed FeaturePython)
  Placement = pos=(589.718,-4.9684,9.95457) rot=(-1,0,0;1.5708rad)
  Visibility1 = true
  a2p_Version = V0.1
  fixedPosition = false
  objectType = a2pPart
  sourceFile = ./FST/M5-tslot-nut.step
  sourcePart = M5-tslot-nut
  subassemblyImport = false
  timeLastImport = 1.66119e+09
  updateColors = true
FEATURE [Part::FeaturePython] b_M5_tslot_nut1_001_019  label="M5-tslot-nut029"  # a2plus imported part (geometry in sourceFile) (typed FeaturePython)
  Placement = pos=(589.718,10.0016,24.5446) rot=(0.707107,0.707107,0;3.14159rad)
  Visibility1 = true
  a2p_Version = V0.1
  fixedPosition = false
  objectType = a2pPart
  sourceFile = ./FST/M5-tslot-nut.step
  sourcePart = M5-tslot-nut
  subassemblyImport = false
  timeLastImport = 1.66119e+09
  updateColors = true
FEATURE [Part::FeaturePython] b_OTS_0009_20x20_v_slot_600mm1_001_002  label="vslot-extrusion-20mmx20mmx600mm"  # a2plus imported part (geometry in sourceFile) (typed FeaturePython)
  Placement = pos=(-0.00959473,-79.9716,90.0176) rot=(1,0,0;1.5708rad)
  Visibility1 = true
  a2p_Version = V0.1
  fixedPosition = false
  objectType = a2pPart
  sourceFile = ./MISC/vslot-extrusion-20mmx20mmx600mm.step
  sourcePart = vslot-extrusion-20mmx20mmx600mm
  subassemblyImport = false
  timeLastImport = 1.66119e+09
  updateColors = true
FEATURE [Part::FeaturePython] b_OTS_0009_20x20_v_slot_600mm1_001_004  label="vslot-extrusion-20mmx20mmx600mm001"  # a2plus imported part (geometry in sourceFile) (typed FeaturePython)
  Placement = pos=(580.068,-79.9849,20.0043) rot=(1,0,0;1.5708rad)
  Visibility1 = true
  a2p_Version = V0.1
  fixedPosition = false
  objectType = a2pPart
  sourceFile = ./MISC/vslot-extrusion-20mmx20mmx600mm.step
  sourcePart = vslot-extrusion-20mmx20mmx600mm
  subassemblyImport = false
  timeLastImport = 1.66119e+09
  updateColors = true
FEATURE [Part::FeaturePython] b_OTS_0009_20x20_v_slot_600mm1_001_005  label="vslot-extrusion-20mmx20mmx600mm002"  # a2plus imported part (geometry in sourceFile) (typed FeaturePython)
  Placement = pos=(580.088,-79.9481,90.0477) rot=(1,0,0;1.5708rad)
  Visibility1 = true
  a2p_Version = V0.1
  fixedPosition = false
  objectType = a2pPart
  sourceFile = ./MISC/vslot-extrusion-20mmx20mmx600mm.step
  sourcePart = vslot-extrusion-20mmx20mmx600mm
  subassemblyImport = false
  timeLastImport = 1.66119e+09
  updateColors = true
FEATURE [Part::FeaturePython] b_OTS_0009_20x20_v_slot_600mm1_001_001  label="vslot-extrusion-20mmx20mmx600mm003"  # a2plus imported part (geometry in sourceFile) (typed FeaturePython)
  Placement = pos=(-0.0637482,-80.0926,20.0674) rot=(1,0,0;1.5708rad)
  Visibility1 = true
  a2p_Version = V0.1
  fixedPosition = false
  objectType = a2pPart
  sourceFile = ./MISC/vslot-extrusion-20mmx20mmx600mm.step
  sourcePart = vslot-extrusion-20mmx20mmx600mm
  subassemblyImport = false
  timeLastImport = 1.66119e+09
  updateColors = true
FEATURE [Part::FeaturePython] b_OTS_0009_20x20_v_slot_600mm1_001_  label="vslot-extrusion-20mmx20mmx600mm004"  # a2plus imported part (geometry in sourceFile) (typed FeaturePython)
  Placement = pos=(0,0,0) rot=(0.57735,-0.57735,-0.57735;2.0944rad)
  Visibility1 = true
  a2p_Version = V0.1
  fixedPosition = true
  objectType = a2pPart
  sourceFile = ./MISC/vslot-extrusion-20mmx20mmx600mm.step
  sourcePart = vslot-extrusion-20mmx20mmx600mm
  subassemblyImport = false
  timeLastImport = 1.66119e+09
  updateColors = true
FEATURE [Part::FeaturePython] b_FDM_0022_umbilical_guide_001_  label="umbilical-cable-strain-relief"  # a2plus imported part (geometry in sourceFile) (typed FeaturePython)
  Placement = pos=(10.0067,111.205,19.9983) rot=(0.57735,-0.57735,0.57735;4.18879rad)
  Visibility1 = true
  a2p_Version = V0.1
  fixedPosition = false
  objectType = a2pPart
  sourceFile = ./FDM/umbilical-cable-strain-relief.FCStd
  sourcePart = Body
  subassemblyImport = false
  timeLastImport = 1.65531e+09
  updateColors = true
FEATURE [Part::FeaturePython] Screw174  label="M3x16-Screw098"  # Fasteners workbench fastener (typed FeaturePython)
  Placement = pos=(300.41,105.09,43.1) rot=(0,0,-1;1.5708rad)
  Visibility1 = true
  diameter = 4
  invert = false
  leftHanded = false
  length = 10
  lengthCustom = 16
  matchOuter = false
  offset = 0
  thread = false
  type = 33
FEATURE [Part::FeaturePython] Screw175  label="M3x16-Screw099"  # Fasteners workbench fastener (typed FeaturePython)
  Placement = pos=(300.41,165.1,43.1) rot=(0,0,-1;1.5708rad)
  Visibility1 = true
  diameter = 4
  invert = false
  leftHanded = false
  length = 10
  lengthCustom = 16
  matchOuter = false
  offset = 0
  thread = false
  type = 33
FEATURE [Part::FeaturePython] Screw176  label="M3x16-Screw100"  # Fasteners workbench fastener (typed FeaturePython)
  Placement = pos=(330.33,135.09,43.1) rot=(0,0,-1;1.5708rad)
  Visibility1 = true
  diameter = 4
  invert = false
  leftHanded = false
  length = 10
  lengthCustom = 16
  matchOuter = false
  offset = 0
  thread = false
  type = 33
FEATURE [Part::FeaturePython] Screw177  label="M3x16-Screw101"  # Fasteners workbench fastener (typed FeaturePython)
  Placement = pos=(270.39,135.05,43.1) rot=(0,0,-1;1.5708rad)
  Visibility1 = true
  diameter = 4
  invert = false
  leftHanded = false
  length = 10
  lengthCustom = 16
  matchOuter = false
  offset = 0
  thread = false
  type = 33
FEATURE [Part::FeaturePython] Nut052  label="M3-Nut543"  # Fasteners workbench fastener (typed FeaturePython)
  Placement = pos=(300.387,105.111,29.47) rot=(0.707107,-0.707107,0;3.14159rad)
  Visibility1 = true
  diameter = 4
  invert = false
  leftHanded = false
  matchOuter = false
  offset = 0
  thread = false
  type = 7
FEATURE [Part::FeaturePython] Nut053  label="M3-Nut544"  # Fasteners workbench fastener (typed FeaturePython)
  Placement = pos=(270.417,135.081,29.77) rot=(1,0,0;3.14159rad)
  Visibility1 = true
  diameter = 4
  invert = false
  leftHanded = false
  matchOuter = false
  offset = 0
  thread = false
  type = 7
FEATURE [Part::FeaturePython] Nut054  label="M3-Nut545"  # Fasteners workbench fastener (typed FeaturePython)
  Placement = pos=(330.287,135.081,29.7) rot=(1,0,0;3.14159rad)
  Visibility1 = true
  diameter = 4
  invert = false
  leftHanded = false
  matchOuter = false
  offset = 0
  thread = false
  type = 7
FEATURE [Part::FeaturePython] Nut055  label="M3-Nut546"  # Fasteners workbench fastener (typed FeaturePython)
  Placement = pos=(300.387,165.101,29.55) rot=(0.707107,-0.707107,0;3.14159rad)
  Visibility1 = true
  diameter = 4
  invert = false
  leftHanded = false
  matchOuter = false
  offset = 0
  thread = false
  type = 7
FEATURE [Part::FeaturePython] Screw139  label="M3x10-Screw"  # Fasteners workbench fastener (typed FeaturePython)
  Placement = pos=(465.5,180,42.98) rot=(0,0,1;0rad)
  Visibility1 = true
  diameter = 1
  invert = false
  leftHanded = false
  length = 2
  lengthCustom = 10
  matchOuter = false
  offset = 0
  thread = false
  type = 39
FEATURE [Part::FeaturePython] Screw142  label="M3x10-Screw114"  # Fasteners workbench fastener (typed FeaturePython)
  Placement = pos=(495.4,180,42.98) rot=(0,0,1;0rad)
  Visibility1 = true
  diameter = 1
  invert = false
  leftHanded = false
  length = 2
  lengthCustom = 10
  matchOuter = false
  offset = 0
  thread = false
  type = 39
FEATURE [Part::FeaturePython] Nut057  label="M3-Nut582"  # Fasteners workbench fastener (typed FeaturePython)
  Placement = pos=(495.5,180,35.75) rot=(1,0,0;3.14159rad)
  Visibility1 = true
  diameter = 4
  invert = false
  leftHanded = false
  matchOuter = false
  offset = 0
  thread = false
  type = 4
FEATURE [Part::FeaturePython] Nut058  label="M3-Nut583"  # Fasteners workbench fastener (typed FeaturePython)
  Placement = pos=(465.6,180,35.75) rot=(1,0,0;3.14159rad)
  Visibility1 = true
  diameter = 4
  invert = false
  leftHanded = false
  matchOuter = false
  offset = 0
  thread = false
  type = 4
FEATURE [Part::FeaturePython] Screw178  label="M5x8-Screw228"  # Fasteners workbench fastener (typed FeaturePython)
  Placement = pos=(10.02,85.38,43.32) rot=(0,0,1;3.14159rad)
  Visibility1 = true
  diameter = 3
  invert = false
  leftHanded = false
  length = 0
  lengthCustom = 8
  matchOuter = false
  offset = 0
  thread = false
  type = 39
FEATURE [Part::FeaturePython] Screw179  label="M5x8-Screw229"  # Fasteners workbench fastener (typed FeaturePython)
  Placement = pos=(10.14,184.98,43.19) rot=(0,0,1;3.14159rad)
  Visibility1 = true
  diameter = 3
  invert = false
  leftHanded = false
  length = 0
  lengthCustom = 8
  matchOuter = false
  offset = 0
  thread = false
  type = 39
FEATURE [Part::FeaturePython] Screw180  label="M5x8-Screw230"  # Fasteners workbench fastener (typed FeaturePython)
  Placement = pos=(590.11,184.98,43.19) rot=(0,0,1;3.14159rad)
  Visibility1 = true
  diameter = 3
  invert = false
  leftHanded = false
  length = 0
  lengthCustom = 8
  matchOuter = false
  offset = 0
  thread = false
  type = 39
FEATURE [Part::FeaturePython] Screw134  label="M5x8-Screw231"  # Fasteners workbench fastener (typed FeaturePython)
  Placement = pos=(590.11,85.4,43.19) rot=(0,0,1;3.14159rad)
  Visibility1 = true
  diameter = 3
  invert = false
  leftHanded = false
  length = 0
  lengthCustom = 8
  matchOuter = false
  offset = 0
  thread = false
  type = 39
FEATURE [Part::FeaturePython] b_FDM_0024_nozzle_holder_001_  label="nozzle-rack"  # a2plus imported part (geometry in sourceFile) (typed FeaturePython)
  Placement = pos=(115.152,173.003,42.9477) rot=(1,0,0;1.5708rad)
  a2p_Version = V0.1
  fixedPosition = false
  objectType = a2pPart
  sourceFile = ./FDM/nozzle-rack.FCStd
  sourcePart = Body
  subassemblyImport = false
  timeLastImport = 1.66276e+09
  updateColors = true
FEATURE [Part::FeaturePython] Nut064  label="M3-Nut549"  # Fasteners workbench fastener (typed FeaturePython)
  Placement = pos=(120.424,104.999,47.93) rot=(1,0,0;3.14159rad)
  Visibility1 = true
  diameter = 4
  invert = false
  leftHanded = false
  matchOuter = false
  offset = 0
  thread = false
  type = 7
FEATURE [Part::FeaturePython] Nut066  label="M3-Nut550"  # Fasteners workbench fastener (typed FeaturePython)
  Placement = pos=(120.424,165.039,47.93) rot=(1,0,0;3.14159rad)
  Visibility1 = true
  diameter = 4
  invert = false
  leftHanded = false
  matchOuter = false
  offset = 0
  thread = false
  type = 7
FEATURE [Part::FeaturePython] Screw156  label="M3x10-Screw125"  # Fasteners workbench fastener (typed FeaturePython)
  Placement = pos=(120.424,105.008,39.94) rot=(0,1,0;3.14159rad)
  Visibility1 = true
  diameter = 1
  invert = false
  leftHanded = false
  length = 2
  lengthCustom = 10
  matchOuter = false
  offset = 0
  thread = false
  type = 39
FEATURE [Part::FeaturePython] Screw158  label="M3x10-Screw126"  # Fasteners workbench fastener (typed FeaturePython)
  Placement = pos=(120.424,165.048,39.94) rot=(0,1,0;3.14159rad)
  Visibility1 = true
  diameter = 1
  invert = false
  leftHanded = false
  length = 2
  lengthCustom = 10
  matchOuter = false
  offset = 0
  thread = false
  type = 39
FEATURE [Part::FeaturePython] Screw159  label="M2.5x8-Screw197"  # Fasteners workbench fastener (typed FeaturePython)
  Placement = pos=(314.37,149.1,-11.44) rot=(0.707107,0.707107,0;3.14159rad)
  Visibility1 = true
  diameter = 3
  invert = false
  leftHanded = false
  length = 3
  lengthCustom = 8
  matchOuter = false
  offset = 0
  thread = false
  type = 33
FEATURE [Part::FeaturePython] Screw160  label="M2.5x8-Screw198"  # Fasteners workbench fastener (typed FeaturePython)
  Placement = pos=(286.39,149.1,-11.44) rot=(0.707107,0.707107,0;3.14159rad)
  Visibility1 = true
  diameter = 3
  invert = false
  leftHanded = false
  length = 3
  lengthCustom = 8
  matchOuter = false
  offset = 0
  thread = false
  type = 33
FEATURE [Part::FeaturePython] Screw161  label="M2.5x8-Screw199"  # Fasteners workbench fastener (typed FeaturePython)
  Placement = pos=(286.39,121.09,-11.44) rot=(0.707107,0.707107,0;3.14159rad)
  Visibility1 = true
  diameter = 3
  invert = false
  leftHanded = false
  length = 3
  lengthCustom = 8
  matchOuter = false
  offset = 0
  thread = false
  type = 33
FEATURE [Part::FeaturePython] Screw162  label="M2.5x8-Screw200"  # Fasteners workbench fastener (typed FeaturePython)
  Placement = pos=(314.37,121.09,-11.44) rot=(0.707107,0.707107,0;3.14159rad)
  Visibility1 = true
  diameter = 3
  invert = false
  leftHanded = false
  length = 3
  lengthCustom = 8
  matchOuter = false
  offset = 0
  thread = false
  type = 33
FEATURE [Part::FeaturePython] b_CSM_0001_staging_plate_001_  label="staging-plate"  # a2plus imported part (geometry in sourceFile) (typed FeaturePython)
  Placement = pos=(0.410743,195.001,42.9729) rot=(1,0,0;3.14159rad)
  Visibility1 = true
  a2p_Version = V0.1
  fixedPosition = false
  objectType = a2pPart
  sourceFile = ./cad/PCB/staging-plate.FCStd
  sourcePart = Body
  subassemblyImport = false
  timeLastImport = 1.65531e+09
  updateColors = true
FEATURE [Part::FeaturePython] b_M5_tslot_nut1_001_030  label="M5-tslot-nut030"  # a2plus imported part (geometry in sourceFile) (typed FeaturePython)
  Placement = pos=(589.718,85.2716,34.9746) rot=(0,0,1;1.5708rad)
  Visibility1 = true
  a2p_Version = V0.1
  fixedPosition = false
  objectType = a2pPart
  sourceFile = ./FST/M5-tslot-nut.step
  sourcePart = M5-tslot-nut
  subassemblyImport = false
  timeLastImport = 1.66119e+09
  updateColors = true
FEATURE [Part::FeaturePython] b_M5_tslot_nut1_001_031  label="M5-tslot-nut031"  # a2plus imported part (geometry in sourceFile) (typed FeaturePython)
  Placement = pos=(589.718,184.922,34.9746) rot=(0,0,1;1.5708rad)
  Visibility1 = true
  a2p_Version = V0.1
  fixedPosition = false
  objectType = a2pPart
  sourceFile = ./FST/M5-tslot-nut.step
  sourcePart = M5-tslot-nut
  subassemblyImport = false
  timeLastImport = 1.66119e+09
  updateColors = true
FEATURE [Part::FeaturePython] b_M5_tslot_nut1_001_032  label="M5-tslot-nut032"  # a2plus imported part (geometry in sourceFile) (typed FeaturePython)
  Placement = pos=(9.85821,184.922,34.9746) rot=(0,0,1;1.5708rad)
  Visibility1 = true
  a2p_Version = V0.1
  fixedPosition = false
  objectType = a2pPart
  sourceFile = ./FST/M5-tslot-nut.step
  sourcePart = M5-tslot-nut
  subassemblyImport = false
  timeLastImport = 1.66119e+09
  updateColors = true
FEATURE [Part::FeaturePython] b_M5_tslot_nut1_001_033  label="M5-tslot-nut033"  # a2plus imported part (geometry in sourceFile) (typed FeaturePython)
  Placement = pos=(9.85821,85.3216,34.9746) rot=(0,0,1;1.5708rad)
  Visibility1 = true
  a2p_Version = V0.1
  fixedPosition = false
  objectType = a2pPart
  sourceFile = ./FST/M5-tslot-nut.step
  sourcePart = M5-tslot-nut
  subassemblyImport = false
  timeLastImport = 1.66119e+09
  updateColors = true
FEATURE [Part::FeaturePython] b_OTS_0003_00_vacuum_pump_001_001  label="vacuum-pump"  # a2plus imported part (geometry in sourceFile) (typed FeaturePython)
  Placement = pos=(481.281,164.986,10.2256) rot=(-0.707107,0,0.707107;3.14159rad)
  Visibility1 = true
  a2p_Version = V0.1
  fixedPosition = false
  objectType = a2pPart
  sourceFile = ./MISC/vacuum-pump.FCStd
  sourcePart = Body
  subassemblyImport = false
  timeLastImport = 1.65531e+09
  updateColors = true
FEATURE [Part::FeaturePython] b_FDM_0025_pump_mount_001_001  label="pump-mount"  # a2plus imported part (geometry in sourceFile) (typed FeaturePython)
  Placement = pos=(452.615,194.574,-15.2591) rot=(0,0,-1;1.5708rad)
  Visibility1 = true
  a2p_Version = 0.4.60i
  fixedPosition = false
  objectType = a2pPart
  sourceFile = ./FDM/pump-mount.FCStd
  sourcePart = Body
  subassemblyImport = false
  timeLastImport = 1.67632e+09
  updateColors = true
FEATURE [Part::FeaturePython] Nut  label="M5-Nut687"  # Fasteners workbench fastener (typed FeaturePython)
  Placement = pos=(443.743,194.103,98.994) rot=(-1,0,0;1.5708rad)
  baseObject = -> Screw044 [Edge16]
  diameter = 3
  invert = true
  leftHanded = false
  matchOuter = false
  offset = -6
  thread = false
  type = 5
FEATURE [Part::FeaturePython] Screw185  label="M2.5x20-Screw"  # Fasteners workbench fastener (typed FeaturePython)
  Placement = pos=(427.094,238.392,103.069) rot=(0,1,0;0rad)
  baseObject = -> b_FDM_0014_down_camera_mount_001_ [Edge333]
  diameter = 3
  invert = false
  leftHanded = false
  length = 8
  lengthCustom = 20
  matchOuter = true
  offset = 2
  thread = false
  type = 34
FEATURE [Part::FeaturePython] Screw186  label="M2.5x20-Screw082"  # Fasteners workbench fastener (typed FeaturePython)
  Placement = pos=(461.074,238.502,102.769) rot=(0,0,-1;1.5708rad)
  baseObject = -> b_FDM_0014_down_camera_mount_001_ [Edge337]
  diameter = 3
  invert = false
  leftHanded = false
  length = 8
  lengthCustom = 20
  matchOuter = true
  offset = 2
  thread = false
  type = 34
FEATURE [Part::FeaturePython] Screw187  label="M2.5x20-Screw083"  # Fasteners workbench fastener (typed FeaturePython)
  Placement = pos=(427.094,204.392,103.069) rot=(0,1,0;0rad)
  baseObject = -> b_FDM_0014_down_camera_mount_001_ [Edge107]
  diameter = 3
  invert = false
  leftHanded = false
  length = 8
  lengthCustom = 20
  matchOuter = true
  offset = 2
  thread = false
  type = 34
FEATURE [Part::FeaturePython] Screw188  label="M2.5x20-Screw081"  # Fasteners workbench fastener (typed FeaturePython)
  Placement = pos=(461.094,204.392,102.569) rot=(0,1,0;0rad)
  diameter = 3
  invert = false
  leftHanded = false
  length = 8
  lengthCustom = 20
  matchOuter = true
  offset = 2
  thread = false
  type = 34
FEATURE [Part::FeaturePython] Screw189  label="M3x14-Screw201"  # Fasteners workbench fastener (typed FeaturePython)
  Placement = pos=(461.094,204.392,104.569) rot=(0,1,0;0rad)
  baseObject = -> b_FDM_0014_down_camera_mount_001_ [Edge355]
  diameter = 1
  invert = false
  leftHanded = false
  length = 4
  lengthCustom = 14
  matchOuter = true
  offset = 0
  thread = false
  type = 40
FEATURE [App::DocumentObjectGroup] Group013  label="GT2BeltClamp"
  Group = -> [b_FDM_0027_belt_clamp_001_003,b_FDM_0027_belt_clamp_001_002,Screw040,Screw041,Screw038,Screw039]
FEATURE [App::DocumentObjectGroup] Group014  label="Z-Motor"
  Group = -> [b_Nema_17_42A02C_v21_001_,b_Gates_2GT_20T_Toothed_Pulley1_001_,Screw085,Screw086,Screw087,Screw088]
FEATURE [Part::FeaturePython] Screw155  label="M3x10-Screw118"  # Fasteners workbench fastener (typed FeaturePython)
  Placement = pos=(135.31,89.88,42.98) rot=(0,0,1;0rad)
  Visibility1 = true
  diameter = 1
  invert = false
  leftHanded = false
  length = 9
  lengthCustom = 10
  matchOuter = false
  offset = 0
  thread = false
  type = 39
FEATURE [Part::FeaturePython] Screw154  label="M3x10-Screw117"  # Fasteners workbench fastener (typed FeaturePython)
  Placement = pos=(135.31,179.8,42.98) rot=(0,0,1;0rad)
  Visibility1 = true
  diameter = 1
  invert = false
  leftHanded = false
  length = 9
  lengthCustom = 10
  matchOuter = false
  offset = 0
  thread = false
  type = 39
FEATURE [Part::FeaturePython] Screw153  label="M3x10-Screw116"  # Fasteners workbench fastener (typed FeaturePython)
  Placement = pos=(45.39,179.8,42.98) rot=(0,0,1;0rad)
  Visibility1 = true
  diameter = 1
  invert = false
  leftHanded = false
  length = 9
  lengthCustom = 10
  matchOuter = false
  offset = 0
  thread = false
  type = 39
FEATURE [Part::FeaturePython] Screw152  label="M3x10-Screw115"  # Fasteners workbench fastener (typed FeaturePython)
  Placement = pos=(45.39,89.88,42.98) rot=(0,0,1;0rad)
  Visibility1 = true
  diameter = 1
  invert = false
  leftHanded = false
  length = 9
  lengthCustom = 10
  matchOuter = false
  offset = 0
  thread = false
  type = 39
FEATURE [Part::FeaturePython] Screw191  label="M3x30-Screw169"  # Fasteners workbench fastener (typed FeaturePython)
  Placement = pos=(45.39,90.02,-8.5) rot=(0.707107,-0.707107,0;3.14159rad)
  diameter = 4
  invert = false
  leftHanded = false
  length = 9
  lengthCustom = 30
  matchOuter = false
  offset = 0
  thread = false
  type = 34
FEATURE [Part::FeaturePython] Screw192  label="M3x10-Screw119"  # Fasteners workbench fastener (typed FeaturePython)
  Placement = pos=(45.39,148.6,9.5) rot=(0.707107,-0.707107,0;3.14159rad)
  diameter = 1
  invert = false
  leftHanded = false
  length = 2
  lengthCustom = 10
  matchOuter = false
  offset = 0
  thread = false
  type = 40
  expr: .Placement.Base.y = 148.6
FEATURE [Part::FeaturePython] Screw193  label="M3x30-Screw170"  # Fasteners workbench fastener (typed FeaturePython)
  Placement = pos=(135.29,179.67,-8.5) rot=(0.707107,-0.707107,0;3.14159rad)
  diameter = 4
  invert = false
  leftHanded = false
  length = 9
  lengthCustom = 30
  matchOuter = false
  offset = 0
  thread = false
  type = 34
FEATURE [Part::FeaturePython] Screw194  label="M3x10-Screw120"  # Fasteners workbench fastener (typed FeaturePython)
  Placement = pos=(135.29,89.82,9.5) rot=(0.707107,-0.707107,0;3.14159rad)
  diameter = 1
  invert = false
  leftHanded = false
  length = 2
  lengthCustom = 10
  matchOuter = false
  offset = 0
  thread = false
  type = 40
FEATURE [Part::FeaturePython] PcbSpacer  label="M3x5.5x25-Spacer"  # Fasteners workbench fastener (typed FeaturePython)
  Placement = pos=(45.39,179.97,40) rot=(0.707107,-0.707107,0;3.14159rad)
  diameter = 2
  invert = false
  leftHanded = false
  length = 19
  lengthCustom = 5
  matchOuter = false
  offset = 0
  thread = false
  type = 0
  width = 1
FEATURE [Part::FeaturePython] PcbSpacer001  label="M3x5.5x25-Spacer004"  # Fasteners workbench fastener (typed FeaturePython)
  Placement = pos=(135.34,179.97,40) rot=(0.707107,-0.707107,0;3.14159rad)
  diameter = 2
  invert = false
  leftHanded = false
  length = 19
  lengthCustom = 5
  matchOuter = false
  offset = 0
  thread = false
  type = 0
  width = 1
FEATURE [Part::FeaturePython] PcbSpacer002  label="M3x5.5x25-Spacer005"  # Fasteners workbench fastener (typed FeaturePython)
  Placement = pos=(45.39,90.02,40) rot=(0.707107,-0.707107,0;3.14159rad)
  diameter = 2
  invert = false
  leftHanded = false
  length = 19
  lengthCustom = 5
  matchOuter = false
  offset = 0
  thread = false
  type = 0
  width = 1
FEATURE [Part::FeaturePython] PcbSpacer003  label="M3x5.5x25-Spacer006"  # Fasteners workbench fastener (typed FeaturePython)
  Placement = pos=(135.34,89.82,40) rot=(0.707107,-0.707107,0;3.14159rad)
  diameter = 2
  invert = false
  leftHanded = false
  length = 19
  lengthCustom = 5
  matchOuter = false
  offset = 0
  thread = false
  type = 0
  width = 1
FEATURE [Part::FeaturePython] b_FDM_0055_datum_board_mount_001_  label="datum-board-mount"  # a2plus imported part (geometry in sourceFile) (typed FeaturePython)
  Placement = pos=(270.391,165.029,42.9044) rot=(0,0,1;0rad)
  a2p_Version = V0.1
  fixedPosition = false
  objectType = a2pPart
  sourceFile = ./FDM/datum-board-mount.FCStd
  sourcePart = Body
  subassemblyImport = false
  timeLastImport = 1.65531e+09
  updateColors = true
FEATURE [Part::FeaturePython] Screw195  label="M3x16-Screw102"  # Fasteners workbench fastener (typed FeaturePython)
  Placement = pos=(330.39,164.99,52.9) rot=(0,0,1;1.5708rad)
  Visibility1 = true
  diameter = 4
  invert = false
  leftHanded = false
  length = 6
  lengthCustom = 16
  matchOuter = false
  offset = 0
  thread = false
  type = 33
FEATURE [Part::FeaturePython] Nut088  label="M3-Nut551"  # Fasteners workbench fastener (typed FeaturePython)
  Placement = pos=(330.41,165.001,37.57) rot=(0,0,-1;1.5708rad)
  diameter = 4
  invert = false
  leftHanded = false
  matchOuter = false
  offset = -2
  thread = false
  type = 7
FEATURE [Part::FeaturePython] Screw196  label="M3x16-Screw103"  # Fasteners workbench fastener (typed FeaturePython)
  Placement = pos=(270.39,164.99,52.9) rot=(0,0,1;1.5708rad)
  Visibility1 = true
  diameter = 4
  invert = false
  leftHanded = false
  length = 6
  lengthCustom = 16
  matchOuter = false
  offset = 0
  thread = false
  type = 33
FEATURE [Part::FeaturePython] Screw197  label="M3x16-Screw104"  # Fasteners workbench fastener (typed FeaturePython)
  Placement = pos=(315.39,179.99,52.9) rot=(0,0,1;1.5708rad)
  Visibility1 = true
  diameter = 4
  invert = false
  leftHanded = false
  length = 6
  lengthCustom = 16
  matchOuter = false
  offset = 0
  thread = false
  type = 33
FEATURE [Part::FeaturePython] Screw198  label="M3x16-Screw105"  # Fasteners workbench fastener (typed FeaturePython)
  Placement = pos=(285.39,179.99,52.9) rot=(0,0,1;1.5708rad)
  Visibility1 = true
  diameter = 4
  invert = false
  leftHanded = false
  length = 6
  lengthCustom = 16
  matchOuter = false
  offset = 0
  thread = false
  type = 33
FEATURE [Part::FeaturePython] Nut089  label="M3-Nut552"  # Fasteners workbench fastener (typed FeaturePython)
  Placement = pos=(270.41,165.001,37.57) rot=(0,0,-1;1.5708rad)
  diameter = 4
  invert = false
  leftHanded = false
  matchOuter = false
  offset = -2
  thread = false
  type = 7
FEATURE [Part::FeaturePython] Nut090  label="M3-Nut553"  # Fasteners workbench fastener (typed FeaturePython)
  Placement = pos=(315.41,180.001,37.57) rot=(0,0,-1;1.5708rad)
  diameter = 4
  invert = false
  leftHanded = false
  matchOuter = false
  offset = -2
  thread = false
  type = 7
FEATURE [Part::FeaturePython] Nut091  label="M3-Nut554"  # Fasteners workbench fastener (typed FeaturePython)
  Placement = pos=(285.41,180.001,37.57) rot=(0,0,-1;1.5708rad)
  diameter = 4
  invert = false
  leftHanded = false
  matchOuter = false
  offset = -2
  thread = false
  type = 7
FEATURE [Part::FeaturePython] Screw199  label="M3x8-Screw525"  # Fasteners workbench fastener (typed FeaturePython)
  Placement = pos=(456.42,171.94,140.5) rot=(1,0,0;1.5708rad)
  Visibility1 = true
  diameter = 1
  invert = false
  leftHanded = false
  length = 1
  lengthCustom = 8
  matchOuter = false
  offset = 0
  thread = false
  type = 39
FEATURE [Part::FeaturePython] Screw200  label="M3x8-Screw526"  # Fasteners workbench fastener (typed FeaturePython)
  Placement = pos=(471.41,171.94,140.5) rot=(1,0,0;1.5708rad)
  Visibility1 = true
  diameter = 1
  invert = false
  leftHanded = false
  length = 1
  lengthCustom = 8
  matchOuter = false
  offset = 0
  thread = false
  type = 39
FEATURE [Part::FeaturePython] Screw201  label="M3x8-Screw533"  # Fasteners workbench fastener (typed FeaturePython)
  Placement = pos=(431.25,171.94,140.83) rot=(1,0,0;1.5708rad)
  Visibility1 = true
  diameter = 1
  invert = false
  leftHanded = false
  length = 1
  lengthCustom = 8
  matchOuter = false
  offset = 0
  thread = false
  type = 39
FEATURE [Part::FeaturePython] Screw202  label="M3x8-Screw534"  # Fasteners workbench fastener (typed FeaturePython)
  Placement = pos=(416.15,171.94,140.83) rot=(1,0,0;1.5708rad)
  Visibility1 = true
  diameter = 1
  invert = false
  leftHanded = false
  length = 1
  lengthCustom = 8
  matchOuter = false
  offset = 0
  thread = false
  type = 39
FEATURE [Part::FeaturePython] Screw203  label="M3x8-Screw543"  # Fasteners workbench fastener (typed FeaturePython)
  Placement = pos=(347.7,173.64,29.84) rot=(-1,0,0;1.5708rad)
  Visibility1 = true
  diameter = 1
  invert = false
  leftHanded = false
  length = 1
  lengthCustom = 8
  matchOuter = false
  offset = 0
  thread = false
  type = 39
FEATURE [Part::FeaturePython] Screw204  label="M3x8-Screw544"  # Fasteners workbench fastener (typed FeaturePython)
  Placement = pos=(362.4,173.84,19.44) rot=(-1,0,0;1.5708rad)
  Visibility1 = true
  diameter = 1
  invert = false
  leftHanded = false
  length = 1
  lengthCustom = 8
  matchOuter = false
  offset = 0
  thread = false
  type = 39
FEATURE [Part::FeaturePython] Screw205  label="M3x8-Screw545"  # Fasteners workbench fastener (typed FeaturePython)
  Placement = pos=(375.7,179.54,43.04) rot=(0,0,1;3.14159rad)
  Visibility1 = true
  diameter = 1
  invert = false
  leftHanded = false
  length = 1
  lengthCustom = 8
  matchOuter = false
  offset = 0
  thread = false
  type = 39
FEATURE [Part::FeaturePython] Nut092  label="M3-Nut567"  # Fasteners workbench fastener (typed FeaturePython)
  Placement = pos=(375.61,179.601,35.97) rot=(0,0,-1;1.5708rad)
  diameter = 4
  invert = false
  leftHanded = false
  matchOuter = false
  offset = -2
  thread = false
  type = 7
FEATURE [Part::FeaturePython] Screw207  label="M3x10-Screw121"  # Fasteners workbench fastener (typed FeaturePython)
  Placement = pos=(180.31,105.09,43.1) rot=(0,0,-1;1.5708rad)
  Visibility1 = true
  diameter = 1
  invert = false
  leftHanded = false
  length = 2
  lengthCustom = 10
  matchOuter = false
  offset = 0
  thread = false
  type = 39
FEATURE [Part::FeaturePython] Screw208  label="M3x8-Screw546"  # Fasteners workbench fastener (typed FeaturePython)
  Placement = pos=(345.6,179.54,43.04) rot=(0,0,1;3.14159rad)
  Visibility1 = true
  diameter = 1
  invert = false
  leftHanded = false
  length = 1
  lengthCustom = 8
  matchOuter = false
  offset = 0
  thread = false
  type = 39
FEATURE [Part::FeaturePython] Nut094  label="M3-Nut566"  # Fasteners workbench fastener (typed FeaturePython)
  Placement = pos=(345.51,179.401,35.97) rot=(0,0,-1;1.5708rad)
  diameter = 4
  invert = false
  leftHanded = false
  matchOuter = false
  offset = -2
  thread = false
  type = 7
FEATURE [Part::FeaturePython] Nut096  label="M3-Nut580"  # Fasteners workbench fastener (typed FeaturePython)
  Placement = pos=(180.32,105.08,39.07) rot=(1,0,0;3.14159rad)
  Visibility1 = true
  diameter = 4
  invert = false
  leftHanded = false
  matchOuter = false
  offset = 0
  thread = false
  type = 7
FEATURE [Part::FeaturePython] Nut097  label="M5-Nut651"  # Fasteners workbench fastener (typed FeaturePython)
  Placement = pos=(412.48,227.808,125.583) rot=(0.186157,0.694747,0.694747;3.50969rad)
  Visibility1 = true
  diameter = 7
  invert = false
  leftHanded = false
  matchOuter = false
  offset = 0
  thread = false
  type = 7
FEATURE [Part::FeaturePython] Nut098  label="M5-Nut652"  # Fasteners workbench fastener (typed FeaturePython)
  Placement = pos=(474.758,227.808,125.653) rot=(0.186157,0.694747,0.694747;3.50969rad)
  Visibility1 = true
  diameter = 7
  invert = false
  leftHanded = false
  matchOuter = false
  offset = 0
  thread = false
  type = 7
FEATURE [Part::FeaturePython] Nut099  label="M5-Nut653"  # Fasteners workbench fastener (typed FeaturePython)
  Placement = pos=(474.821,227.808,164.761) rot=(0.186157,0.694747,0.694747;3.50969rad)
  Visibility1 = true
  diameter = 7
  invert = false
  leftHanded = false
  matchOuter = false
  offset = 0
  thread = false
  type = 7
FEATURE [Part::FeaturePython] Nut100  label="M5-Nut654"  # Fasteners workbench fastener (typed FeaturePython)
  Placement = pos=(412.815,227.808,164.764) rot=(0.186157,0.694747,0.694747;3.50969rad)
  Visibility1 = true
  diameter = 7
  invert = false
  leftHanded = false
  matchOuter = false
  offset = 0
  thread = false
  type = 7
FEATURE [Part::FeaturePython] b_FDM_0023_peek_cable_guide_001_  label="peek-cable-clamp"  # a2plus imported part (geometry in sourceFile) (typed FeaturePython)
  Placement = pos=(555.348,89.9438,36.6196) rot=(0.57735,-0.57735,0.57735;4.18879rad)
  a2p_Version = V0.1
  fixedPosition = false
  objectType = a2pPart
  sourceFile = ./FDM/peek-cable-clamp.FCStd
  subassemblyImport = false
  timeLastImport = 1.66147e+09
  updateColors = true
FEATURE [Part::FeaturePython] b_FDM_0023_peek_cable_guide_001_001  label="peek-cable-clamp001"  # a2plus imported part (geometry in sourceFile) (typed FeaturePython)
  Placement = pos=(435.248,89.9438,36.6196) rot=(0.57735,-0.57735,0.57735;4.18879rad)
  a2p_Version = V0.1
  fixedPosition = false
  objectType = a2pPart
  sourceFile = ./FDM/peek-cable-clamp.FCStd
  subassemblyImport = false
  timeLastImport = 1.66147e+09
  updateColors = true
FEATURE [Part::FeaturePython] b_FDM_0023_peek_cable_guide_001_002  label="peek-cable-clamp002"  # a2plus imported part (geometry in sourceFile) (typed FeaturePython)
  Placement = pos=(255.048,89.9438,36.6196) rot=(0.57735,-0.57735,0.57735;4.18879rad)
  a2p_Version = V0.1
  fixedPosition = false
  objectType = a2pPart
  sourceFile = ./FDM/peek-cable-clamp.FCStd
  subassemblyImport = false
  timeLastImport = 1.66147e+09
  updateColors = true
FEATURE [Part::FeaturePython] b_FDM_0023_peek_cable_guide_001_003  label="peek-cable-clamp003"  # a2plus imported part (geometry in sourceFile) (typed FeaturePython)
  Placement = pos=(405.948,179.944,36.6196) rot=(0.57735,0.57735,-0.57735;4.18879rad)
  a2p_Version = V0.1
  fixedPosition = false
  objectType = a2pPart
  sourceFile = ./FDM/peek-cable-clamp.FCStd
  subassemblyImport = false
  timeLastImport = 1.66147e+09
  updateColors = true
FEATURE [Part::FeaturePython] b_FDM_0023_peek_cable_guide_001_004  label="peek-cable-clamp004"  # a2plus imported part (geometry in sourceFile) (typed FeaturePython)
  Placement = pos=(195.448,179.944,36.6196) rot=(0.57735,0.57735,-0.57735;4.18879rad)
  a2p_Version = V0.1
  fixedPosition = false
  objectType = a2pPart
  sourceFile = ./FDM/peek-cable-clamp.FCStd
  subassemblyImport = false
  timeLastImport = 1.66147e+09
  updateColors = true
FEATURE [Part::FeaturePython] b_FDM_0023_peek_cable_guide_001_005  label="peek-cable-clamp005"  # a2plus imported part (geometry in sourceFile) (typed FeaturePython)
  Placement = pos=(435.348,149.944,36.6196) rot=(0.57735,0.57735,-0.57735;4.18879rad)
  a2p_Version = V0.1
  fixedPosition = false
  objectType = a2pPart
  sourceFile = ./FDM/peek-cable-clamp.FCStd
  subassemblyImport = false
  timeLastImport = 1.66147e+09
  updateColors = true
FEATURE [Part::FeaturePython] Nut101  label="M3-Nut556"  # Fasteners workbench fastener (typed FeaturePython)
  Placement = pos=(195.487,179.701,32.8) rot=(0.707107,-0.707107,0;3.14159rad)
  Visibility1 = true
  diameter = 4
  invert = false
  leftHanded = false
  matchOuter = false
  offset = 0
  thread = false
  type = 7
FEATURE [Part::FeaturePython] Screw210  label="M3x14-Screw187"  # Fasteners workbench fastener (typed FeaturePython)
  Placement = pos=(195.39,179.99,42.8) rot=(0,0,1;1.5708rad)
  Visibility1 = true
  diameter = 1
  invert = false
  leftHanded = false
  length = 4
  lengthCustom = 14
  matchOuter = false
  offset = 0
  thread = false
  type = 39
FEATURE [Part::FeaturePython] Screw211  label="M3x14-Screw188"  # Fasteners workbench fastener (typed FeaturePython)
  Placement = pos=(406.19,179.99,42.8) rot=(0,0,1;1.5708rad)
  Visibility1 = true
  diameter = 1
  invert = false
  leftHanded = false
  length = 4
  lengthCustom = 14
  matchOuter = false
  offset = 0
  thread = false
  type = 39
FEATURE [Part::FeaturePython] Screw212  label="M3x14-Screw189"  # Fasteners workbench fastener (typed FeaturePython)
  Placement = pos=(255.39,89.69,42.8) rot=(0,0,1;1.5708rad)
  Visibility1 = true
  diameter = 1
  invert = false
  leftHanded = false
  length = 4
  lengthCustom = 14
  matchOuter = false
  offset = 0
  thread = false
  type = 39
FEATURE [Part::FeaturePython] Screw213  label="M3x14-Screw190"  # Fasteners workbench fastener (typed FeaturePython)
  Placement = pos=(435.39,149.79,42.8) rot=(0,0,1;1.5708rad)
  Visibility1 = true
  diameter = 1
  invert = false
  leftHanded = false
  length = 4
  lengthCustom = 14
  matchOuter = false
  offset = 0
  thread = false
  type = 39
FEATURE [Part::FeaturePython] Screw214  label="M3x14-Screw191"  # Fasteners workbench fastener (typed FeaturePython)
  Placement = pos=(555.39,89.89,42.8) rot=(0,0,1;1.5708rad)
  Visibility1 = true
  diameter = 1
  invert = false
  leftHanded = false
  length = 4
  lengthCustom = 14
  matchOuter = false
  offset = 0
  thread = false
  type = 39
FEATURE [Part::FeaturePython] Screw215  label="M3x14-Screw192"  # Fasteners workbench fastener (typed FeaturePython)
  Placement = pos=(435.19,89.89,42.8) rot=(0,0,1;1.5708rad)
  Visibility1 = true
  diameter = 1
  invert = false
  leftHanded = false
  length = 4
  lengthCustom = 14
  matchOuter = false
  offset = 0
  thread = false
  type = 39
FEATURE [Part::FeaturePython] Nut102  label="M3-Nut557"  # Fasteners workbench fastener (typed FeaturePython)
  Placement = pos=(406.087,179.701,32.8) rot=(0.707107,-0.707107,0;3.14159rad)
  Visibility1 = true
  diameter = 4
  invert = false
  leftHanded = false
  matchOuter = false
  offset = 0
  thread = false
  type = 7
FEATURE [Part::FeaturePython] Nut103  label="M3-Nut561"  # Fasteners workbench fastener (typed FeaturePython)
  Placement = pos=(255.347,89.7,32.8) rot=(0.707107,-0.707107,0;3.14159rad)
  Visibility1 = true
  diameter = 4
  invert = false
  leftHanded = false
  matchOuter = false
  offset = 0
  thread = false
  type = 7
FEATURE [Part::FeaturePython] Nut104  label="M3-Nut558"  # Fasteners workbench fastener (typed FeaturePython)
  Placement = pos=(435.487,149.901,32.8) rot=(0.707107,-0.707107,0;3.14159rad)
  Visibility1 = true
  diameter = 4
  invert = false
  leftHanded = false
  matchOuter = false
  offset = 0
  thread = false
  type = 7
FEATURE [Part::FeaturePython] Nut105  label="M3-Nut560"  # Fasteners workbench fastener (typed FeaturePython)
  Placement = pos=(435.187,89.9012,32.8) rot=(0.707107,-0.707107,0;3.14159rad)
  Visibility1 = true
  diameter = 4
  invert = false
  leftHanded = false
  matchOuter = false
  offset = 0
  thread = false
  type = 7
FEATURE [Part::FeaturePython] Nut106  label="M3-Nut559"  # Fasteners workbench fastener (typed FeaturePython)
  Placement = pos=(555.387,89.9012,31.45) rot=(0.707107,-0.707107,0;3.14159rad)
  Visibility1 = true
  diameter = 4
  invert = false
  leftHanded = false
  matchOuter = false
  offset = 0
  thread = false
  type = 7
FEATURE [Part::FeaturePython] b_PCB_0002_00_Datum_OpenPNPcalibration1_001_  label="datum-board"  # a2plus imported part (geometry in sourceFile) (typed FeaturePython)
  Placement = pos=(260.466,155.381,51.3924) rot=(0,0,1;0rad)
  a2p_Version = V0.1
  fixedPosition = false
  objectType = a2pPart
  sourceFile = ./PCB/datum-board.step
  subassemblyImport = false
  timeLastImport = 1.65531e+09
  updateColors = true
FEATURE [Part::FeaturePython] b_FDM_0016_cable_clip_001_  label="extrusion-cable-clip"  # a2plus imported part (geometry in sourceFile) (typed FeaturePython)
  Placement = pos=(589.786,334.255,19.7601) rot=(1,0,0;1.5708rad)
  a2p_Version = V0.1
  fixedPosition = false
  objectType = a2pPart
  sourceFile = .\FDM\extrusion-cable-clip.FCStd
  subassemblyImport = false
  timeLastImport = 1.66716e+09
  updateColors = true
FEATURE [Part::FeaturePython] b_FDM_0016_cable_clip_001_001  label="extrusion-cable-clip001"  # a2plus imported part (geometry in sourceFile) (typed FeaturePython)
  Placement = pos=(589.708,291.599,21.0844) rot=(1,0,0;1.5708rad)
  a2p_Version = V0.1
  fixedPosition = false
  objectType = a2pPart
  sourceFile = .\FDM\extrusion-cable-clip.FCStd
  subassemblyImport = false
  timeLastImport = 1.66716e+09
  updateColors = true
FEATURE [Part::FeaturePython] b_FDM_0016_cable_clip_001_002  label="extrusion-cable-clip002"  # a2plus imported part (geometry in sourceFile) (typed FeaturePython)
  Placement = pos=(589.708,253.003,20.7641) rot=(1,0,0;1.5708rad)
  a2p_Version = V0.1
  fixedPosition = false
  objectType = a2pPart
  sourceFile = .\FDM\extrusion-cable-clip.FCStd
  subassemblyImport = false
  timeLastImport = 1.66716e+09
  updateColors = true
FEATURE [Part::FeaturePython] b_FDM_0016_cable_clip_001_003  label="extrusion-cable-clip003"  # a2plus imported part (geometry in sourceFile) (typed FeaturePython)
  Placement = pos=(589.708,174.891,20.1235) rot=(1,0,0;1.5708rad)
  a2p_Version = V0.1
  fixedPosition = false
  objectType = a2pPart
  sourceFile = .\FDM\extrusion-cable-clip.FCStd
  subassemblyImport = false
  timeLastImport = 1.66716e+09
  updateColors = true
FEATURE [Part::FeaturePython] b_PCB_0003_00_RingLight1_001_  label="bottom-ring-light"  # a2plus imported part (geometry in sourceFile) (typed FeaturePython)
  Placement = pos=(300.339,135.516,32.5) rot=(0,0,1;0.802851rad)
  a2p_Version = V0.1
  fixedPosition = false
  objectType = a2pPart
  sourceFile = ./PCB/bottom-ring-light.FCStd
  subassemblyImport = false
  timeLastImport = 1.66119e+09
  updateColors = true
FEATURE [Part::FeaturePython] b_PCB_0003_00_RingLight1_001_001  label="top-ring-light"  # a2plus imported part (geometry in sourceFile) (typed FeaturePython)
  Placement = pos=(444.287,221.73,86.9615) rot=(0,1,0;3.14159rad)
  a2p_Version = V0.1
  fixedPosition = false
  objectType = a2pPart
  sourceFile = ./PCB/top-ring-light.FCStd
  subassemblyImport = false
  timeLastImport = 1.66119e+09
  updateColors = true
FEATURE [App::DocumentObjectGroup] Group012  label="CameraAndLight"
  Group = -> [b_FDM_0014_down_camera_mount_001_,b_FDM_0015_down_light_mount_001_,Screw171,Screw185,Screw186,Screw187,Screw188,Screw189,b_OTS_0002_00_usb_webcam_001_,b_PCB_0003_00_RingLight1_001_001]
FEATURE [Part::FeaturePython] Screw216  label="M2.5x8-Screw194"  # Fasteners workbench fastener (typed FeaturePython)
  Placement = pos=(408.6,144.4,120.66) rot=(0.707107,-0.707107,0;3.14159rad)
  diameter = 3
  invert = false
  leftHanded = false
  length = 3
  lengthCustom = 8
  matchOuter = false
  offset = 0
  thread = false
  type = 34
FEATURE [Part::FeaturePython] Screw217  label="M2.5x8-Screw195"  # Fasteners workbench fastener (typed FeaturePython)
  Placement = pos=(431.5,144.4,120.66) rot=(0.707107,-0.707107,0;3.14159rad)
  diameter = 3
  invert = false
  leftHanded = false
  length = 3
  lengthCustom = 8
  matchOuter = false
  offset = 0
  thread = false
  type = 34
FEATURE [Part::FeaturePython] Screw218  label="M2.5x8-Screw"  # Fasteners workbench fastener (typed FeaturePython)
  Placement = pos=(408.5,167.3,120.66) rot=(0.707107,-0.707107,0;3.14159rad)
  diameter = 3
  invert = false
  leftHanded = false
  length = 3
  lengthCustom = 8
  matchOuter = false
  offset = 0
  thread = false
  type = 34
FEATURE [Part::FeaturePython] Screw219  label="M2.5x8-Screw196"  # Fasteners workbench fastener (typed FeaturePython)
  Placement = pos=(431.5,167.3,120.66) rot=(0.707107,-0.707107,0;3.14159rad)
  diameter = 3
  invert = false
  leftHanded = false
  length = 3
  lengthCustom = 8
  matchOuter = false
  offset = 0
  thread = false
  type = 34
FEATURE [Part::FeaturePython] b_FST_0017_M3_cap_nut1_001_  label="M3-cap-nut"  # a2plus imported part (geometry in sourceFile) (typed FeaturePython)
  Placement = pos=(575.135,-89.5237,100.422) rot=(1,0,0;1.5708rad)
  a2p_Version = V0.1
  fixedPosition = false
  objectType = a2pPart
  sourceFile = ./FST/M3-cap-nut.STEP
  subassemblyImport = false
  timeLastImport = 1.65531e+09
  updateColors = true
FEATURE [Part::FeaturePython] b_FST_0017_M3_cap_nut1_001_001  label="M3-cap-nut001"  # a2plus imported part (geometry in sourceFile) (typed FeaturePython)
  Placement = pos=(626.288,224.192,144.277) rot=(0.57735,0.57735,0.57735;2.0944rad)
  a2p_Version = V0.1
  fixedPosition = false
  objectType = a2pPart
  sourceFile = ./FST/M3-cap-nut.STEP
  subassemblyImport = false
  timeLastImport = 1.65531e+09
  updateColors = true
FEATURE [Part::FeaturePython] b_FST_0017_M3_cap_nut1_001_002  label="M3-cap-nut002"  # a2plus imported part (geometry in sourceFile) (typed FeaturePython)
  Placement = pos=(25.0268,-89.3507,100.008) rot=(1,0,0;1.5708rad)
  a2p_Version = V0.1
  fixedPosition = false
  objectType = a2pPart
  sourceFile = ./FST/M3-cap-nut.STEP
  subassemblyImport = false
  timeLastImport = 1.65531e+09
  updateColors = true
FEATURE [Part::FeaturePython] b_OTS_0014_linear_rail_100mm_LML9B1_001_  label="LML9B-linear-rail-100mm001"  # a2plus imported part (geometry in sourceFile) (typed FeaturePython)
  Placement = pos=(463.908,183.899,191.455) rot=(0.707107,0,-0.707107;3.14159rad)
  a2p_Version = V0.1
  fixedPosition = false
  objectType = a2pPart
  sourceFile = ./MISC/LML9B-linear-rail-100mm.step
  subassemblyImport = false
  timeLastImport = 1.65531e+09
  updateColors = true
FEATURE [Part::FeaturePython] b_OTS_0014_linear_rail_100mm_LML9B1_001_001  label="LML9B-linear-rail-100mm"  # a2plus imported part (geometry in sourceFile) (typed FeaturePython)
  Placement = pos=(423.808,184.099,191.555) rot=(0.707107,0,-0.707107;3.14159rad)
  a2p_Version = V0.1
  fixedPosition = false
  objectType = a2pPart
  sourceFile = ./MISC/LML9B-linear-rail-100mm.step
  subassemblyImport = false
  timeLastImport = 1.65531e+09
  updateColors = true
FEATURE [Part::FeaturePython] b_NEMA11_hollow_shaft_stepper1_001_  label="NEMA11-hollow-shaft-stepper"  # a2plus imported part (geometry in sourceFile) (typed FeaturePython)
  Placement = pos=(420.01,155.83,142.55) rot=(0.707107,-0.707107,0;3.14159rad)
  a2p_Version = V0.1
  fixedPosition = false
  objectType = a2pPart
  sourceFile = ./MISC/NEMA11-hollow-shaft-stepper.step
  subassemblyImport = false
  timeLastImport = 1.66119e+09
  updateColors = true
FEATURE [Part::FeaturePython] b_x_gantry_back_001_  label="x-gantry-back"  # a2plus imported part (geometry in sourceFile) (typed FeaturePython)
  Placement = pos=(443.82,231.25,123.31) rot=(1,0,0;1.5708rad)
  a2p_Version = V0.1
  fixedPosition = false
  objectType = a2pPart
  sourceFile = ./FDM/x-gantry-back.FCStd
  subassemblyImport = false
  timeLastImport = 1.66119e+09
  updateColors = true
FEATURE [Part::FeaturePython] b_x_idler_mount_001_  label="x-idler-mount_001"  # a2plus imported part (geometry in sourceFile) (typed FeaturePython)
  Placement = pos=(622.24,209.11,124.04) rot=(0.57735,-0.57735,-0.57735;2.0944rad)
  a2p_Version = V0.1
  fixedPosition = false
  objectType = a2pPart
  sourceFile = ./FDM/x-idler-mount.FCStd
  subassemblyImport = false
  timeLastImport = 1.66119e+09
  updateColors = true
FEATURE [Part::FeaturePython] b_x_motor_mount_001_  label="x-motor-mount"  # a2plus imported part (geometry in sourceFile) (typed FeaturePython)
  Placement = pos=(-21.95,209.15,133.99) rot=(0.57735,0.57735,0.57735;2.0944rad)
  a2p_Version = V0.1
  fixedPosition = false
  objectType = a2pPart
  sourceFile = ./FDM/x-motor-mount.FCStd
  subassemblyImport = false
  timeLastImport = 1.66119e+09
  updateColors = true
FEATURE [Part::FeaturePython] b_M5_tslot_nut1_001_034  label="M5-tslot-nut034"  # a2plus imported part (geometry in sourceFile) (typed FeaturePython)
  Placement = pos=(594.328,209.112,148.905) rot=(0,0,1;0rad)
  Visibility1 = true
  a2p_Version = V0.1
  fixedPosition = false
  objectType = a2pPart
  sourceFile = ./FST/M5-tslot-nut.step
  sourcePart = M5-tslot-nut
  subassemblyImport = false
  timeLastImport = 1.66119e+09
  updateColors = true
FEATURE [Part::FeaturePython] Screw220  label="M5x10-Screw350"  # Fasteners workbench fastener (typed FeaturePython)
  Placement = pos=(594.27,209.12,158.94) rot=(0,0,-1;1.5708rad)
  Visibility1 = true
  diameter = 6
  invert = false
  leftHanded = false
  length = 1
  lengthCustom = 10
  matchOuter = false
  offset = 0
  thread = false
  type = 33
FEATURE [Part::FeaturePython] b_M5_tslot_nut1_001_035  label="M5-tslot-nut035"  # a2plus imported part (geometry in sourceFile) (typed FeaturePython)
  Placement = pos=(6.12821,209.212,148.905) rot=(0,0,1;0rad)
  Visibility1 = true
  a2p_Version = V0.1
  fixedPosition = false
  objectType = a2pPart
  sourceFile = ./FST/M5-tslot-nut.step
  sourcePart = M5-tslot-nut
  subassemblyImport = false
  timeLastImport = 1.66119e+09
  updateColors = true
FEATURE [Part::FeaturePython] Screw221  label="M5x10-Screw351"  # Fasteners workbench fastener (typed FeaturePython)
  Placement = pos=(6,209.22,158.94) rot=(0,0,-1;1.5708rad)
  Visibility1 = true
  diameter = 6
  invert = false
  leftHanded = false
  length = 1
  lengthCustom = 10
  matchOuter = false
  offset = 0
  thread = false
  type = 33
FEATURE [Part::FeaturePython] Nut107  label="M5-Nut656"  # Fasteners workbench fastener (typed FeaturePython)
  Placement = pos=(477.946,213.8,195.3) rot=(0.654654,0.377965,0.654654;2.41886rad)
  Visibility1 = true
  diameter = 7
  invert = false
  leftHanded = false
  matchOuter = false
  offset = 0
  thread = false
  type = 7
FEATURE [Part::FeaturePython] Nut108  label="M5-Nut655"  # Fasteners workbench fastener (typed FeaturePython)
  Placement = pos=(477.946,213.8,210.3) rot=(0.654654,0.377965,0.654654;2.41886rad)
  Visibility1 = true
  diameter = 7
  invert = false
  leftHanded = false
  matchOuter = false
  offset = 0
  thread = false
  type = 7
FEATURE [Part::FeaturePython] Screw222  label="M5x16-Screw006"  # Fasteners workbench fastener (typed FeaturePython)
  Placement = pos=(490.95,213.8,210.3) rot=(0.654654,0.377964,0.654654;2.41886rad)
  Visibility1 = true
  diameter = 6
  invert = false
  leftHanded = false
  length = 12
  lengthCustom = 16
  matchOuter = false
  offset = 0
  thread = false
  type = 33
FEATURE [Part::FeaturePython] Screw223  label="M5x16-Screw005"  # Fasteners workbench fastener (typed FeaturePython)
  Placement = pos=(490.95,213.8,195.3) rot=(0.654654,0.377964,0.654654;2.41886rad)
  Visibility1 = true
  diameter = 6
  invert = false
  leftHanded = false
  length = 12
  lengthCustom = 16
  matchOuter = false
  offset = 0
  thread = false
  type = 33
FEATURE [Part::FeaturePython] Nut015  label="M5-Nut675"  # Fasteners workbench fastener (typed FeaturePython)
  Placement = pos=(603.67,209.1,98.11) rot=(0.57735,0.57735,0.57735;2.0944rad)
  Visibility1 = true
  diameter = 7
  invert = false
  leftHanded = false
  matchOuter = false
  offset = 0
  thread = false
  type = 7
FEATURE [Part::FeaturePython] Screw013  label="M5x25-Screw142"  # Fasteners workbench fastener (typed FeaturePython)
  Placement = pos=(625.18,209.1,98.11) rot=(0.57735,0.57735,0.57735;2.0944rad)
  Visibility1 = true
  diameter = 6
  invert = false
  leftHanded = false
  length = 12
  lengthCustom = 25
  matchOuter = false
  offset = 0
  thread = false
  type = 33
FEATURE [Part::FeaturePython] Nut014  label="M5-Nut674"  # Fasteners workbench fastener (typed FeaturePython)
  Placement = pos=(603.67,209.66,121.52) rot=(0.447214,0.774597,0.447214;1.82348rad)
  Visibility1 = true
  diameter = 7
  invert = false
  leftHanded = false
  matchOuter = false
  offset = 0
  thread = false
  type = 7
FEATURE [Part::FeaturePython] Screw012  label="M5x25-Screw143"  # Fasteners workbench fastener (typed FeaturePython)
  Placement = pos=(625.24,209.5,122.25) rot=(0.57735,0.57735,0.57735;2.0944rad)
  Visibility1 = true
  diameter = 6
  invert = false
  leftHanded = false
  length = 12
  lengthCustom = 25
  matchOuter = false
  offset = 0
  thread = false
  type = 33
FEATURE [Part::FeaturePython] Nut109  label="M5-Nut671"  # Fasteners workbench fastener (typed FeaturePython)
  Placement = pos=(-6.94552,209.153,97.985) rot=(0.57735,-0.57735,0.57735;4.18879rad)
  diameter = 7
  invert = true
  leftHanded = false
  matchOuter = true
  offset = -5
  thread = false
  type = 7
FEATURE [Part::FeaturePython] Nut110  label="M5-Nut686"  # Fasteners workbench fastener (typed FeaturePython)
  Placement = pos=(-6.94552,209.153,121.985) rot=(-0.447214,0.774597,-0.447214;1.82348rad)
  diameter = 7
  invert = true
  leftHanded = false
  matchOuter = true
  offset = -5
  thread = false
  type = 7
FEATURE [Part::FeaturePython] Screw226  label="M5x25-Screw138"  # Fasteners workbench fastener (typed FeaturePython)
  Placement = pos=(-24.9455,209.153,121.985) rot=(0.57735,-0.57735,-0.57735;2.0944rad)
  diameter = 6
  invert = true
  leftHanded = false
  length = 12
  lengthCustom = 25
  matchOuter = true
  offset = 0
  thread = false
  type = 34
FEATURE [Part::FeaturePython] Screw227  label="M5x25-Screw139"  # Fasteners workbench fastener (typed FeaturePython)
  Placement = pos=(-24.9455,209.153,97.985) rot=(0.57735,-0.57735,-0.57735;2.0944rad)
  diameter = 6
  invert = true
  leftHanded = false
  length = 12
  lengthCustom = 25
  matchOuter = true
  offset = 0
  thread = false
  type = 34
FEATURE [App::DocumentObjectGroup] X_Motor  label="X-Motor"
  Group = -> [b_Gates_2GT_20T_Toothed_Pulley1_001_001,b_Nema_17_42A02C_v21_001_001,Screw098,Screw099,Screw097,Screw100]
FEATURE [App::DocumentObjectGroup] Front_Feeder_Rail  label="Front-Feeder-Rail"
  Group = -> [b_M5_tslot_nut1_001_018,b_OTS_0009_20x20_v_slot_600mm1_001_,Screw075,b_M5_tslot_nut1_001_016,Screw074,Screw073,b_2020CornerBracket1_001_001,b_2020CornerBracket1_001_,Screw076,b_M5_tslot_nut1_001_017,b_M5_tslot_nut1_001_019,b_M5_tslot_nut1_001_012,b_M5_tslot_nut1_001_011,Screw037,Screw072]
FEATURE [App::DocumentObjectGroup] Rear_Feeder_Rail  label="Rear-Feeder-Rail"
  Group = -> [Screw080,Screw084,b_M5_tslot_nut1_001_025,Screw078,b_2020CornerBracket1_001_005,b_2020CornerBracket1_001_003,b_2020CornerBracket1_001_002,b_M5_tslot_nut1_001_022,b_M5_tslot_nut1_001_020,Screw079,Screw083,Screw082,b_M5_tslot_nut1_001_023,b_M5_tslot_nut1_001_026,b_M5_tslot_nut1_001_024,b_2020CornerBracket1_001_004,Screw077,Screw081,b_M5_tslot_nut1_001_027,b_M5_tslot_nut1_001_021,+1 more]
FEATURE [App::DocumentObjectGroup] Group  label="Feeder-Rails"
  Group = -> [Rear_Feeder_Rail,Front_Feeder_Rail]
FEATURE [App::DocumentObjectGroup] Extrusion  label="Y-Left-Extrusion"
  Group = -> [b_FDM_0022_umbilical_guide_001_,b_OTS_0009_20x20_v_slot_600mm1_001_002,Screw104,Screw103,b_M5_tslot_nut1_001_028,b_M5_tslot_nut1_001_029,b_OTS_0009_20x20_v_slot_600mm1_001_001]
FEATURE [App::DocumentObjectGroup] Extrusion001  label="Y-Right-Extrusion"
  Group = -> [b_FDM_0016_cable_clip_001_002,b_FDM_0016_cable_clip_001_003,b_FDM_0016_cable_clip_001_001,b_FDM_0016_cable_clip_001_,b_OTS_0009_20x20_v_slot_600mm1_001_004,b_OTS_0009_20x20_v_slot_600mm1_001_005]
FEATURE [Part::FeaturePython] b_belt_tension_arm_001_  label="x-belt-tension-arm"  # a2plus imported part (geometry in sourceFile) (typed FeaturePython)
  Placement = pos=(627.16,189.23,134.07) rot=(0.57735,0.57735,0.57735;2.0944rad)
  a2p_Version = V0.1
  fixedPosition = false
  objectType = a2pPart
  sourceFile = ./FDM/belt-tension-arm.FCStd
  subassemblyImport = false
  timeLastImport = 1.66119e+09
  updateColors = true
FEATURE [Part::FeaturePython] b_belt_tension_arm_001_001  label="y2-belt-tension-arm"  # a2plus imported part (geometry in sourceFile) (typed FeaturePython)
  Placement = pos=(610.04,-90.5,110.07) rot=(0,0.707107,-0.707107;3.14159rad)
  a2p_Version = V0.1
  fixedPosition = false
  objectType = a2pPart
  sourceFile = ./FDM/belt-tension-arm.FCStd
  subassemblyImport = false
  timeLastImport = 1.66119e+09
  updateColors = true
FEATURE [Part::FeaturePython] b_belt_tension_arm_001_002  label="y1-belt-tension-arm"  # a2plus imported part (geometry in sourceFile) (typed FeaturePython)
  Placement = pos=(-10.04,-90.59,89.98) rot=(1,0,0;1.5708rad)
  a2p_Version = V0.1
  fixedPosition = false
  objectType = a2pPart
  sourceFile = ./FDM/belt-tension-arm.FCStd
  subassemblyImport = false
  timeLastImport = 1.66119e+09
  updateColors = true
FEATURE [Part::FeaturePython] Screw228  label="M5x10-Screw364"  # Fasteners workbench fastener (typed FeaturePython)
  Placement = pos=(-6.72,-85.5,195.3) rot=(0.654654,0.377964,0.654654;2.41886rad)
  Visibility1 = true
  diameter = 6
  invert = false
  leftHanded = false
  length = 12
  lengthCustom = 10
  matchOuter = false
  offset = 0
  thread = false
  type = 33
FEATURE [Part::FeaturePython] Nut111  label="M5-Nut660"  # Fasteners workbench fastener (typed FeaturePython)
  Placement = pos=(-17.52,-86.865,210.3) rot=(0.654654,0.377964,0.654654;2.41886rad)
  Visibility1 = true
  diameter = 7
  invert = false
  leftHanded = false
  matchOuter = false
  offset = 0
  thread = false
  type = 7
FEATURE [Part::FeaturePython] Screw229  label="M5x10-Screw365"  # Fasteners workbench fastener (typed FeaturePython)
  Placement = pos=(-6.72,-86.865,210.3) rot=(0.654654,0.377964,0.654654;2.41886rad)
  Visibility1 = true
  diameter = 6
  invert = false
  leftHanded = false
  length = 12
  lengthCustom = 10
  matchOuter = false
  offset = 0
  thread = false
  type = 33
FEATURE [Part::FeaturePython] Nut112  label="M5-Nut661"  # Fasteners workbench fastener (typed FeaturePython)
  Placement = pos=(-17.52,-85.5,195.3) rot=(0.654654,0.377964,0.654654;2.41886rad)
  Visibility1 = true
  diameter = 7
  invert = false
  leftHanded = false
  matchOuter = false
  offset = 0
  thread = false
  type = 7
FEATURE [App::DocumentObjectGroup] Drag_Chain_Bolts  label="Drag_Chain_to_Drag_Chain_Mount_Attachment_Hardware"
  Group = -> [Screw228,Nut111,Screw229,Nut112]
FEATURE [Part::FeaturePython] b_NEMA11_hollow_shaft_stepper1_001_001  label="NEMA11-hollow-shaft-stepper001"  # a2plus imported part (geometry in sourceFile) (typed FeaturePython)
  Placement = pos=(467.62,155.88,142.54) rot=(0.707107,-0.707107,0;3.14159rad)
  a2p_Version = V0.1
  fixedPosition = false
  objectType = a2pPart
  sourceFile = ./MISC/NEMA11-hollow-shaft-stepper.step
  subassemblyImport = false
  timeLastImport = 1.66119e+09
  updateColors = true
FEATURE [Part::FeaturePython] b_OTS_0001_00_CP40_nozzle_holder_001_001  label="CP40-holder001"  # a2plus imported part (geometry in sourceFile) (typed FeaturePython)
  Placement = pos=(467.658,155.84,87.7745) rot=(0.57735,-0.57735,-0.57735;2.0944rad)
  Visibility1 = true
  a2p_Version = V0.1
  fixedPosition = false
  objectType = a2pPart
  sourceFile = ./MISC/cp40-holder.FCStd
  sourcePart = Body
  subassemblyImport = false
  timeLastImport = 1.65531e+09
  updateColors = true
FEATURE [Part::FeaturePython] b_MS4M_M51_001_001  label="pneumatic-adapter-MS4M-M006"  # a2plus imported part (geometry in sourceFile) (typed FeaturePython)
  Placement = pos=(467.662,155.88,162.502) rot=(0.57735,-0.57735,-0.57735;2.0944rad)
  Visibility1 = true
  a2p_Version = V0.1
  fixedPosition = false
  objectType = a2pPart
  sourceFile = ./MISC/pneumatic-adapter-MS4M-M5.STEP
  sourcePart = MS4M-M5
  subassemblyImport = false
  timeLastImport = 1.65531e+09
  updateColors = true
FEATURE [Part::FeaturePython] b_OTS_0009_pneumatic_splitter_URY6M_4M1_001_001  label="pneumatic-y-adapter001"  # a2plus imported part (geometry in sourceFile) (typed FeaturePython)
  Placement = pos=(202.73,126.644,24.3499) rot=(0.57735,-0.57735,0.57735;2.0944rad)
  a2p_Version = V0.1
  fixedPosition = false
  objectType = a2pPart
  sourceFile = ./MISC/pneumatic-y-adapter.STEP
  subassemblyImport = false
  timeLastImport = 1.65531e+09
  updateColors = true
FEATURE [Part::FeaturePython] Nut113  label="M3-Nut581"  # Fasteners workbench fastener (typed FeaturePython)
  Placement = pos=(180.32,135.08,38.57) rot=(1,0,0;3.14159rad)
  Visibility1 = true
  diameter = 4
  invert = false
  leftHanded = false
  matchOuter = false
  offset = 0
  thread = false
  type = 7
FEATURE [Part::FeaturePython] Screw232  label="M3x30-Screw171"  # Fasteners workbench fastener (typed FeaturePython)
  Placement = pos=(180.56,133.09,24.35) rot=(0.57735,0.57735,0.57735;4.18879rad)
  Visibility1 = true
  diameter = 4
  invert = false
  leftHanded = false
  length = 9
  lengthCustom = 30
  matchOuter = false
  offset = 0
  thread = false
  type = 33
FEATURE [Part::FeaturePython] b_OTS_0003_00_vacuum_pump_001_002  label="vacuum-pump001"  # a2plus imported part (geometry in sourceFile) (typed FeaturePython)
  Placement = pos=(481.281,104.986,10.2256) rot=(-0.707107,0,0.707107;3.14159rad)
  Visibility1 = true
  a2p_Version = V0.1
  fixedPosition = false
  objectType = a2pPart
  sourceFile = ./MISC/vacuum-pump.FCStd
  sourcePart = Body
  subassemblyImport = false
  timeLastImport = 1.65531e+09
  updateColors = true
FEATURE [Part::FeaturePython] b_FDM_0025_pump_mount_001_002  label="pump-mount001"  # a2plus imported part (geometry in sourceFile) (typed FeaturePython)
  Placement = pos=(452.615,134.574,-15.2591) rot=(0,0,-1;1.5708rad)
  Visibility1 = true
  a2p_Version = 0.4.60i
  fixedPosition = false
  objectType = a2pPart
  sourceFile = ./FDM/pump-mount.FCStd
  sourcePart = Body
  subassemblyImport = false
  timeLastImport = 1.67632e+09
  updateColors = true
FEATURE [Part::FeaturePython] Screw233  label="M3x10-Screw122"  # Fasteners workbench fastener (typed FeaturePython)
  Placement = pos=(495.4,120,42.98) rot=(0,0,1;0rad)
  Visibility1 = true
  diameter = 1
  invert = false
  leftHanded = false
  length = 2
  lengthCustom = 10
  matchOuter = false
  offset = 0
  thread = false
  type = 39
FEATURE [Part::FeaturePython] Nut114  label="M3-Nut584"  # Fasteners workbench fastener (typed FeaturePython)
  Placement = pos=(495.5,120,35.75) rot=(1,0,0;3.14159rad)
  Visibility1 = true
  diameter = 4
  invert = false
  leftHanded = false
  matchOuter = false
  offset = 0
  thread = false
  type = 4
FEATURE [Part::FeaturePython] Screw234  label="M3x10-Screw123"  # Fasteners workbench fastener (typed FeaturePython)
  Placement = pos=(465.5,120,42.98) rot=(0,0,1;0rad)
  Visibility1 = true
  diameter = 1
  invert = false
  leftHanded = false
  length = 2
  lengthCustom = 10
  matchOuter = false
  offset = 0
  thread = false
  type = 39
FEATURE [Part::FeaturePython] Nut115  label="M3-Nut585"  # Fasteners workbench fastener (typed FeaturePython)
  Placement = pos=(465.6,120,35.75) rot=(1,0,0;3.14159rad)
  Visibility1 = true
  diameter = 4
  invert = false
  leftHanded = false
  matchOuter = false
  offset = 0
  thread = false
  type = 4
FEATURE [App::DocumentObjectGroup] _nd_Toolhead_Stuff  label="Right-Toolhead-Pnumatics-System"
  Group = -> [b_OTS_0009_pneumatic_splitter_URY6M_4M1_001_001,Nut113,Screw232,b_OTS_0003_00_vacuum_pump_001_002,b_FDM_0025_pump_mount_001_002,Screw233,Nut114,Screw234,Nut115]
FEATURE [Part::FeaturePython] b_staging_plate1_001_  label="staging-plate1"  # a2plus imported part (geometry in sourceFile) (typed FeaturePython)
  Placement = pos=(161.45,159.05,42.9729) rot=(1,0,0;3.14159rad)
  a2p_Version = V0.1
  fixedPosition = false
  objectType = a2pPart
  sourceFile = ./pcb/staging-plate/staging-plate.STEP
  subassemblyImport = false
  timeLastImport = 1.65775e+09
  updateColors = true
FEATURE [Part::FeaturePython] Screw235  label="M5x8-Screw232"  # Fasteners workbench fastener (typed FeaturePython)
  Placement = pos=(10.14,304.98,43.19) rot=(0,0,1;3.14159rad)
  Visibility1 = true
  diameter = 3
  invert = false
  leftHanded = false
  length = 0
  lengthCustom = 8
  matchOuter = false
  offset = 0
  thread = false
  type = 39
FEATURE [Part::FeaturePython] Screw236  label="M5x8-Screw233"  # Fasteners workbench fastener (typed FeaturePython)
  Placement = pos=(10.02,205.38,43.32) rot=(0,0,1;3.14159rad)
  Visibility1 = true
  diameter = 3
  invert = false
  leftHanded = false
  length = 0
  lengthCustom = 8
  matchOuter = false
  offset = 0
  thread = false
  type = 39
FEATURE [Part::FeaturePython] Screw237  label="M5x8-Screw234"  # Fasteners workbench fastener (typed FeaturePython)
  Placement = pos=(590.11,205.4,43.19) rot=(0,0,1;3.14159rad)
  Visibility1 = true
  diameter = 3
  invert = false
  leftHanded = false
  length = 0
  lengthCustom = 8
  matchOuter = false
  offset = 0
  thread = false
  type = 39
FEATURE [Part::FeaturePython] Screw238  label="M5x8-Screw235"  # Fasteners workbench fastener (typed FeaturePython)
  Placement = pos=(590.11,304.98,43.19) rot=(0,0,1;3.14159rad)
  Visibility1 = true
  diameter = 3
  invert = false
  leftHanded = false
  length = 0
  lengthCustom = 8
  matchOuter = false
  offset = 0
  thread = false
  type = 39
FEATURE [Part::FeaturePython] b_M5_tslot_nut1_001_036  label="M5-tslot-nut036"  # a2plus imported part (geometry in sourceFile) (typed FeaturePython)
  Placement = pos=(589.718,304.922,34.9746) rot=(0,0,1;1.5708rad)
  Visibility1 = true
  a2p_Version = V0.1
  fixedPosition = false
  objectType = a2pPart
  sourceFile = ./FST/M5-tslot-nut.step
  sourcePart = M5-tslot-nut
  subassemblyImport = false
  timeLastImport = 1.66119e+09
  updateColors = true
FEATURE [Part::FeaturePython] b_M5_tslot_nut1_001_037  label="M5-tslot-nut037"  # a2plus imported part (geometry in sourceFile) (typed FeaturePython)
  Placement = pos=(589.718,205.272,34.9746) rot=(0,0,1;1.5708rad)
  Visibility1 = true
  a2p_Version = V0.1
  fixedPosition = false
  objectType = a2pPart
  sourceFile = ./FST/M5-tslot-nut.step
  sourcePart = M5-tslot-nut
  subassemblyImport = false
  timeLastImport = 1.66119e+09
  updateColors = true
FEATURE [Part::FeaturePython] b_M5_tslot_nut1_001_038  label="M5-tslot-nut038"  # a2plus imported part (geometry in sourceFile) (typed FeaturePython)
  Placement = pos=(9.85821,304.922,34.9746) rot=(0,0,1;1.5708rad)
  Visibility1 = true
  a2p_Version = V0.1
  fixedPosition = false
  objectType = a2pPart
  sourceFile = ./FST/M5-tslot-nut.step
  sourcePart = M5-tslot-nut
  subassemblyImport = false
  timeLastImport = 1.66119e+09
  updateColors = true
FEATURE [Part::FeaturePython] b_M5_tslot_nut1_001_039  label="M5-tslot-nut039"  # a2plus imported part (geometry in sourceFile) (typed FeaturePython)
  Placement = pos=(9.85821,205.322,34.9746) rot=(0,0,1;1.5708rad)
  Visibility1 = true
  a2p_Version = V0.1
  fixedPosition = false
  objectType = a2pPart
  sourceFile = ./FST/M5-tslot-nut.step
  sourcePart = M5-tslot-nut
  subassemblyImport = false
  timeLastImport = 1.66119e+09
  updateColors = true
FEATURE [Part::FeaturePython] b_OTS_0020_index_motherboard1_001_001  label="motherboard"  # a2plus imported part (geometry in sourceFile) (typed FeaturePython)
  Placement = pos=(-28.7282,19.2199,10.999) rot=(1,0,0;3.14159rad)
  a2p_Version = V0.1
  fixedPosition = false
  objectType = a2pPart
  sourceFile = ./PCB/motherboard.FCStd
  subassemblyImport = false
  timeLastImport = 1.66191e+09
  updateColors = true
FEATURE [Part::FeaturePython] b_FDM_0020_up_camera_mount_001_001  label="bottom-camera-mount"  # a2plus imported part (geometry in sourceFile) (typed FeaturePython)
  Placement = pos=(300.37,135.06,-11.25) rot=(0,0,1;0rad)
  Visibility1 = true
  a2p_Version = V0.1
  fixedPosition = false
  objectType = a2pPart
  sourceFile = ./FDM/bottom-camera-mount.FCStd
  sourcePart = Body
  subassemblyImport = false
  timeLastImport = 1.66119e+09
  updateColors = true
FEATURE [Part::FeaturePython] b_OTS_0002_00_usb_webcam_001_002  label="usb-camera-lower"  # a2plus imported part (geometry in sourceFile) (typed FeaturePython)
  Placement = pos=(300.231,135.15,-7.8) rot=(0,0,1;3.14159rad)
  Visibility1 = true
  a2p_Version = V0.1
  fixedPosition = false
  objectType = a2pPart
  sourceFile = ./MISC/usb-camera.FCStd
  sourcePart = Body
  subassemblyImport = false
  timeLastImport = 1.66758e+09
  updateColors = true
FEATURE [Part::FeaturePython] b_FDM_0019_up_light_mount_001_001  label="bottom-light-mount"  # a2plus imported part (geometry in sourceFile) (typed FeaturePython)
  Placement = pos=(300.398,135.029,32.2367) rot=(0,1,0;3.14159rad)
  Visibility1 = true
  a2p_Version = V0.1
  fixedPosition = false
  objectType = a2pPart
  sourceFile = ./FDM/bottom-light-mount.FCStd
  sourcePart = Body
  subassemblyImport = false
  timeLastImport = 1.66119e+09
  updateColors = true
FEATURE [Part::FeaturePython] b_valve_mount_2_up_001_  label="valve-mount"  # a2plus imported part (geometry in sourceFile) (typed FeaturePython)
  Placement = pos=(341.58,183.57,39.67) rot=(0.57735,-0.57735,0.57735;4.18879rad)
  a2p_Version = V0.1
  fixedPosition = false
  objectType = a2pPart
  sourceFile = ./FDM/valve-mount.FCStd
  subassemblyImport = false
  timeLastImport = 1.66276e+09
  updateColors = true
FEATURE [Part::FeaturePython] b_24v_3_Way_Solenoid_Valve_0526T_www_fspump_cn_001_002  label="solenoid-valve"  # a2plus imported part (geometry in sourceFile) (typed FeaturePython)
  Placement = pos=(366.181,168.46,23.5489) rot=(0,0,1;3.14159rad)
  a2p_Version = V0.1
  fixedPosition = false
  objectType = a2pPart
  sourceFile = ./MISC/solenoid-valve.FCStd
  subassemblyImport = false
  timeLastImport = 1.65531e+09
  updateColors = true
FEATURE [Part::FeaturePython] b_24v_3_Way_Solenoid_Valve_0526T_www_fspump_cn_001_003  label="solenoid-valve001"  # a2plus imported part (geometry in sourceFile) (typed FeaturePython)
  Placement = pos=(366.181,168.46,5.54892) rot=(0,0,1;3.14159rad)
  a2p_Version = V0.1
  fixedPosition = false
  objectType = a2pPart
  sourceFile = ./MISC/solenoid-valve.FCStd
  subassemblyImport = false
  timeLastImport = 1.65531e+09
  updateColors = true
FEATURE [Part::FeaturePython] Screw243  label="M3x8-Screw542"  # Fasteners workbench fastener (typed FeaturePython)
  Placement = pos=(360.4,164.64,43.04) rot=(0,0,1;3.14159rad)
  Visibility1 = true
  diameter = 1
  invert = false
  leftHanded = false
  length = 1
  lengthCustom = 8
  matchOuter = false
  offset = 0
  thread = false
  type = 39
FEATURE [Part::FeaturePython] Nut120  label="M3-Nut565"  # Fasteners workbench fastener (typed FeaturePython)
  Placement = pos=(360.41,164.601,35.97) rot=(0,0,-1;1.5708rad)
  diameter = 4
  invert = false
  leftHanded = false
  matchOuter = false
  offset = -2
  thread = false
  type = 7
FEATURE [Part::FeaturePython] Screw244  label="M3x8-Screw547"  # Fasteners workbench fastener (typed FeaturePython)
  Placement = pos=(347.7,173.64,9.84) rot=(-1,0,0;1.5708rad)
  Visibility1 = true
  diameter = 1
  invert = false
  leftHanded = false
  length = 1
  lengthCustom = 8
  matchOuter = false
  offset = 0
  thread = false
  type = 39
FEATURE [Part::FeaturePython] Screw245  label="M3x8-Screw541"  # Fasteners workbench fastener (typed FeaturePython)
  Placement = pos=(362.4,173.84,-0.56) rot=(-1,0,0;1.5708rad)
  Visibility1 = true
  diameter = 1
  invert = false
  leftHanded = false
  length = 1
  lengthCustom = 8
  matchOuter = false
  offset = 0
  thread = false
  type = 39
FEATURE [App::DocumentObjectGroup] Valves
  Group = -> [Screw245,Nut120,b_24v_3_Way_Solenoid_Valve_0526T_www_fspump_cn_001_003,b_24v_3_Way_Solenoid_Valve_0526T_www_fspump_cn_001_002,Screw243,b_valve_mount_2_up_001_,Nut094,Screw203,Screw204,Screw205,Nut092,Screw208,Screw244]
FEATURE [Part::FeaturePython] b_mobo_bottom_cover_001_  label="mobo-bottom-cover"  # a2plus imported part (geometry in sourceFile) (typed FeaturePython)
  Placement = pos=(40.32,185.25,14.11) rot=(1,0,0;3.14159rad)
  a2p_Version = V0.1
  fixedPosition = false
  objectType = a2pPart
  sourceFile = ./FDM/mobo-bottom-cover.FCStd
  subassemblyImport = false
  timeLastImport = 1.6619e+09
  updateColors = true
FEATURE [Part::FeaturePython] b_foot_2_001_001  label="static-camera-foot"  # a2plus imported part (geometry in sourceFile) (typed FeaturePython)
  Placement = pos=(0,31.05,0) rot=(0,0,1;0rad)
  a2p_Version = 0.4.60i
  fixedPosition = false
  objectType = a2pPart
  sourceFile = ./FDM/static-camera-foot.FCStd
  subassemblyImport = false
  timeLastImport = 1.67708e+09
  updateColors = true
FEATURE [Part::FeaturePython] b_bottom_camera_cover_001_  label="bottom-camera-cover"  # a2plus imported part (geometry in sourceFile) (typed FeaturePython)
  Placement = pos=(0,31.05,0) rot=(0,0,1;0rad)
  a2p_Version = V0.1
  fixedPosition = false
  objectType = a2pPart
  sourceFile = ./FDM/bottom-camera-cover.FCStd
  subassemblyImport = false
  timeLastImport = 1.66119e+09
  updateColors = true
FEATURE [Part::FeaturePython] Screw246  label="M2.5x8-Screw188"  # Fasteners workbench fastener (typed FeaturePython)
  Placement = pos=(456.1,144.4,120.45) rot=(0.707107,-0.707107,0;3.14159rad)
  diameter = 3
  invert = false
  leftHanded = false
  length = 3
  lengthCustom = 8
  matchOuter = false
  offset = 0
  thread = false
  type = 34
FEATURE [Part::FeaturePython] Screw247  label="M2.5x8-Screw190"  # Fasteners workbench fastener (typed FeaturePython)
  Placement = pos=(479,144.4,120.45) rot=(0.707107,-0.707107,0;3.14159rad)
  diameter = 3
  invert = false
  leftHanded = false
  length = 3
  lengthCustom = 8
  matchOuter = false
  offset = 0
  thread = false
  type = 34
FEATURE [Part::FeaturePython] Screw248  label="M2.5x8-Screw187"  # Fasteners workbench fastener (typed FeaturePython)
  Placement = pos=(479,167.3,120.45) rot=(0.707107,-0.707107,0;3.14159rad)
  diameter = 3
  invert = false
  leftHanded = false
  length = 3
  lengthCustom = 8
  matchOuter = false
  offset = 0
  thread = false
  type = 34
FEATURE [Part::FeaturePython] Screw249  label="M2.5x8-Screw189"  # Fasteners workbench fastener (typed FeaturePython)
  Placement = pos=(456,167.3,120.45) rot=(0.707107,-0.707107,0;3.14159rad)
  diameter = 3
  invert = false
  leftHanded = false
  length = 3
  lengthCustom = 8
  matchOuter = false
  offset = 0
  thread = false
  type = 34
FEATURE [Part::FeaturePython] b_back_leg_cleaned_001_  label="back-leg"  # a2plus imported part (geometry in sourceFile) (typed FeaturePython)
  Placement = pos=(590,500.06,-49.9) rot=(0.57735,-0.57735,-0.57735;2.0944rad)
  a2p_Version = 0.4.60i
  fixedPosition = false
  objectType = a2pPart
  sourceFile = ./FDM/back-leg.FCStd
  subassemblyImport = false
  timeLastImport = 1.6766e+09
  updateColors = true
FEATURE [App::DocumentObjectGroup] Group007  label="Back-Right-Leg"
  Group = -> [b_Gates_2GT_20T_Toothed_Pulley1_001_003,Screw096,Screw093,Screw094,Screw095,b_Nema_17_42A02C_v21_001_003,Screw032,Screw033,Screw034,b_M5_tslot_nut1_001_007,b_M5_tslot_nut1_001_006,b_M5_tslot_nut1_001_005,b_back_leg_cleaned_001_]
FEATURE [Part::FeaturePython] b_back_leg_cleaned_001_001  label="back-leg001"  # a2plus imported part (geometry in sourceFile) (typed FeaturePython)
  Placement = pos=(9.91,500.07,-49.89) rot=(0.57735,-0.57735,-0.57735;2.0944rad)
  a2p_Version = 0.4.60i
  fixedPosition = false
  objectType = a2pPart
  sourceFile = ./FDM/back-leg.FCStd
  subassemblyImport = false
  timeLastImport = 1.6766e+09
  updateColors = true
FEATURE [App::DocumentObjectGroup] Group006  label="Back-Left-Leg"
  Group = -> [Screw089,Screw090,Screw091,Screw092,b_Nema_17_42A02C_v21_001_002,b_Gates_2GT_20T_Toothed_Pulley1_001_002,Screw029,Screw030,Screw031,b_M5_tslot_nut1_001_002,b_M5_tslot_nut1_001_003,b_M5_tslot_nut1_001_004,b_back_leg_cleaned_001_001]
FEATURE [Part::FeaturePython] b_front_drag_chain_mount_v3_001_  label="front-drag-chain-mount"  # a2plus imported part (geometry in sourceFile) (typed FeaturePython)
  Placement = pos=(-10.02,-60.05,73.2389) rot=(0.57735,-0.57735,-0.57735;2.0944rad)
  a2p_Version = V0.1
  fixedPosition = false
  objectType = a2pPart
  sourceFile = ./FDM/front-drag-chain-mount.FCStd
  subassemblyImport = false
  timeLastImport = 1.66119e+09
  updateColors = true
FEATURE [Part::FeaturePython] Screw250  label="M5x25-Screw"  # Fasteners workbench fastener (typed FeaturePython)
  Placement = pos=(-18.02,-72.55,79.99) rot=(0.57735,-0.57735,-0.57735;2.0944rad)
  diameter = 6
  invert = false
  leftHanded = false
  length = 12
  lengthCustom = 25
  matchOuter = false
  offset = 0
  thread = false
  type = 34
FEATURE [Part::FeaturePython] Screw251  label="M5x16-Screw"  # Fasteners workbench fastener (typed FeaturePython)
  Placement = pos=(-18.02,-72.55,99.99) rot=(0.57735,-0.57735,-0.57735;2.0944rad)
  diameter = 6
  invert = false
  leftHanded = false
  length = 4
  lengthCustom = 16
  matchOuter = false
  offset = 0
  thread = false
  type = 34
FEATURE [Part::FeaturePython] Nut121  label="M5-Nut664"  # Fasteners workbench fastener (typed FeaturePython)
  Placement = pos=(-2.12,-72.55,99.99) rot=(-0.654654,0.377964,0.654654;3.86433rad)
  Visibility1 = true
  diameter = 7
  invert = false
  leftHanded = false
  matchOuter = false
  offset = 0
  thread = false
  type = 7
FEATURE [Part::FeaturePython] Nut122  label="M5-Nut663"  # Fasteners workbench fastener (typed FeaturePython)
  Placement = pos=(4.98,-72.55,79.99) rot=(-0.654654,0.377964,0.654654;3.86433rad)
  Visibility1 = true
  diameter = 7
  invert = false
  leftHanded = false
  matchOuter = false
  offset = 0
  thread = false
  type = 7
FEATURE [App::DocumentObjectGroup] Group004  label="Front-Left-Leg"
  Group = -> [b_M5_tslot_nut1_001_008,Nut048,Nut045,b_Gates_2GT_20T_Toothed_Idler1_001_001,Nut033,Screw052,Screw053,Screw054,Screw035,Screw036,Screw051,b_M5_tslot_nut1_001_009,b_M5_tslot_nut1_001_010,b_FDM_0001_front_left_leg_001_,b_FST_0017_M3_cap_nut1_001_002,b_belt_tension_arm_001_002,Nut122,Nut121]
FEATURE [Part::FeaturePython] b_x_motor_cable_guide_001_  label="x-motor-cable-guide"  # a2plus imported part (geometry in sourceFile) (typed FeaturePython)
  Placement = pos=(-43.3,230.65,146.1) rot=(0,0.707107,0.707107;3.14159rad)
  a2p_Version = V0.1
  fixedPosition = false
  objectType = a2pPart
  sourceFile = ./FDM/x-motor-cable-guide.FCStd
  subassemblyImport = false
  timeLastImport = 1.66119e+09
  updateColors = true
FEATURE [Part::FeaturePython] b_front_right_leg_001_  label="front-right-leg"  # a2plus imported part (geometry in sourceFile) (typed FeaturePython)
  Placement = pos=(640,0,20) rot=(0.57735,-0.57735,-0.57735;2.0944rad)
  a2p_Version = 0.4.60i
  fixedPosition = false
  objectType = a2pPart
  sourceFile = ./FDM/front-right-leg.FCStd
  subassemblyImport = false
  timeLastImport = 1.6766e+09
  updateColors = true
FEATURE [App::DocumentObjectGroup] Group005  label="Front-Right-Leg"
  Group = -> [b_M5_tslot_nut1_001_014,b_Gates_2GT_20T_Toothed_Idler1_001_003,Nut046,Screw062,Nut047,Screw063,Nut049,Screw064,Screw070,Screw071,b_M5_tslot_nut1_001_013,b_FST_0017_M3_cap_nut1_001_,b_M5_tslot_nut1_001_015,Screw061,b_belt_tension_arm_001_001,b_front_right_leg_001_]
FEATURE [Part::FeaturePython] b_y_gantry_001_  label="y-gantry_001"  # a2plus imported part (geometry in sourceFile) (typed FeaturePython)
  Placement = pos=(612.22,209.11,134.02) rot=(0.57735,-0.57735,-0.57735;2.0944rad)
  a2p_Version = V0.1
  fixedPosition = false
  objectType = a2pPart
  sourceFile = ./FDM/y-gantry.FCStd
  subassemblyImport = false
  timeLastImport = 1.6657e+09
  updateColors = true
FEATURE [App::DocumentObjectGroup] Y_Gantry_Slider_Right  label="Y-Gantry-Slider-Right"
  Group = -> [Nut020,Screw057,Nut019,Nut039,b_FDM_0027_belt_clamp_001_004,b_FDM_0009_roller_spacer_001_003,Screw019,b_v_slot_roller1_001_006,b_v_slot_roller1_001_007,b_FDM_0009_roller_spacer_001_002,Nut018,Nut040,Nut041,Nut038,Screw055,Nut017,Screw056,b_FDM_0027_belt_clamp_001_005,Screw058,Screw018,Screw020,b_v_slot_roller1_001_008,Screw016,Screw017,b_FDM_0008_y_gantry_support_001_001,Nut016,Nut014,Nut015,+1 more]
FEATURE [App::DocumentObjectGroup] Y_Gantry_Right  label="Y-Gantry-Right"
  Group = -> [Extrusion001,Group007,Group005,Y_Gantry_Slider_Right]
FEATURE [Part::FeaturePython] b_y_gantry_001_001  label="y-gantry_002"  # a2plus imported part (geometry in sourceFile) (typed FeaturePython)
  Placement = pos=(-11.94,209.13,133.94) rot=(0.57735,0.57735,0.57735;2.0944rad)
  a2p_Version = V0.1
  fixedPosition = false
  objectType = a2pPart
  sourceFile = ./FDM/y-gantry.FCStd
  subassemblyImport = false
  timeLastImport = 1.6657e+09
  updateColors = true
FEATURE [App::DocumentObjectGroup] Y_Gantry_Slider_Left  label="Y-Gantry-Slider-Left"
  Group = -> [Screw003,b_FDM_0008_y_gantry_support_001_,Screw027,Nut036,Screw025,Nut037,Screw004,Screw007,Screw005,Nut035,b_FDM_0027_belt_clamp_001_001,b_FDM_0027_belt_clamp_001_,Nut034,b_FDM_0009_roller_spacer_001_,b_v_slot_roller1_001_002,Nut007,Screw026,b_FDM_0009_roller_spacer_001_001,Screw006,b_v_slot_roller1_001_001,Nut005,Nut004,Nut006,Screw028,Nut003,b_v_slot_roller1_001_,b_y_gantry_001_001,Nut110,+1 more]
FEATURE [App::DocumentObjectGroup] Y_Gantry_Left  label="Y-Gantry-Left"
  Group = -> [Extrusion,Group006,Group004,Y_Gantry_Slider_Left]
FEATURE [App::DocumentObjectGroup] Y_Gantry_Legs  label="Y-Gantry"
  Group = -> [Y_Gantry_Right,Y_Gantry_Left]
FEATURE [Part::FeaturePython] Screw253  label="M5x16-Screw002"  # Fasteners workbench fastener (typed FeaturePython)
  Placement = pos=(-35.79,235.65,156.1) rot=(0,0.707107,0.707107;3.14159rad)
  Visibility1 = true
  diameter = 6
  invert = false
  leftHanded = false
  length = 4
  lengthCustom = 16
  matchOuter = false
  offset = 0
  thread = false
  type = 33
FEATURE [Part::FeaturePython] Screw254  label="M5x16-Screw001"  # Fasteners workbench fastener (typed FeaturePython)
  Placement = pos=(-50.79,235.65,156.1) rot=(0,0.707107,0.707107;3.14159rad)
  Visibility1 = true
  diameter = 6
  invert = false
  leftHanded = false
  length = 4
  lengthCustom = 16
  matchOuter = false
  offset = 0
  thread = false
  type = 33
FEATURE [Part::FeaturePython] Nut124  label="M5-Nut685"  # Fasteners workbench fastener (typed FeaturePython)
  Placement = pos=(-35.79,223.15,156.1) rot=(0.186157,0.694747,0.694747;3.50969rad)
  Visibility1 = true
  diameter = 7
  invert = false
  leftHanded = false
  matchOuter = false
  offset = 0
  thread = false
  type = 7
FEATURE [Part::FeaturePython] Nut125  label="M5-Nut684"  # Fasteners workbench fastener (typed FeaturePython)
  Placement = pos=(-50.79,223.15,156.1) rot=(0.186157,0.694747,0.694747;3.50969rad)
  Visibility1 = true
  diameter = 7
  invert = false
  leftHanded = false
  matchOuter = false
  offset = 0
  thread = false
  type = 7
FEATURE [App::DocumentObjectGroup] X_Gantry_Removable_Subassembly  label="X-Gantry001"
  Group = -> [Screw227,Screw013,Screw221,Screw220,b_x_motor_mount_001_,b_x_idler_mount_001_,Screw226,b_M5_tslot_nut1_001_034,Screw012,b_M5_tslot_nut1_001_035,X_Motor,Screw059,Screw060,b_M5_tslot_nut1_001_001,Screw022,b_Gates_2GT_20T_Toothed_Idler1_001_002,Screw021,Nut042,Nut044,Nut043,b_OTS_0009_20x20_v_slot_600mm1_001_003,b_M5_tslot_nut1_001_,Screw023,b_FST_0017_M3_cap_nut1_001_001,b_belt_tension_arm_001_,+5 more]
FEATURE [Part::FeaturePython] Screw255  label="M3x30-Screw"  # Fasteners workbench fastener (typed FeaturePython)
  Placement = pos=(484.88,192.287,121.01) rot=(-0.707107,0.707107,0;3.14159rad)
  baseObject = -> b_FDM_0043_001_001 [Edge69]
  diameter = 4
  invert = false
  leftHanded = false
  length = 9
  lengthCustom = 30
  matchOuter = false
  offset = 0
  thread = false
  type = 33
FEATURE [App::DocumentObjectGroup] Group015  label="Toolhead-Base"
  Group = -> [Nut,b_FDM_0011_x_gantry_front_001_,b_v_slot_roller1_001_003,b_v_slot_roller1_001_004,b_Gates_2GT_20T_Toothed_Idler1_001_,b_v_slot_roller1_001_005,Screw044,b_FDM_0009_roller_spacer_001_005,b_FDM_0009_roller_spacer_001_004,b_FDM_0043_001_,b_FDM_0043_001_001,Screw165,Screw166,Screw167,Screw,Screw168,Screw169,Screw170,Nut068,Nut069,Nut070,Nut071,b_OTS_0011_v_slot_roller1_001_,Screw045,Screw046,+28 more]
FEATURE [App::DocumentObjectGroup] Drag_Chain_Mount_to_Front_Leg_Attachment_Hardware
  Group = -> [Screw251,Screw250]
FEATURE [App::DocumentObjectGroup] Drag_Chain  label="Drag-Chain-Assembly"
  Group = -> [Drag_Chain_Bolts,b_front_drag_chain_mount_v3_001_,Drag_Chain_Mount_to_Front_Leg_Attachment_Hardware]
FEATURE [Part::FeaturePython] b_aux_staging_plate_foot_001_  label="aux-staging-plate-foot_001"  # a2plus imported part (geometry in sourceFile) (typed FeaturePython)
  Placement = pos=(300.43,255.05,39.97) rot=(0.707107,0.707107,0;3.14159rad)
  a2p_Version = 0.4.60i
  fixedPosition = false
  objectType = a2pPart
  sourceFile = ./FDM/aux-staging-plate-foot.FCStd
  subassemblyImport = false
  timeLastImport = 1.67708e+09
  updateColors = true
FEATURE [Part::FeaturePython] Nut126  label="M3-Nut594"  # Fasteners workbench fastener (typed FeaturePython)
  Placement = pos=(300.387,255.101,33.97) rot=(0.707107,-0.707107,0;3.14159rad)
  Visibility1 = true
  diameter = 4
  invert = false
  leftHanded = false
  matchOuter = false
  offset = 0
  thread = false
  type = 4
FEATURE [Part::FeaturePython] Screw257  label="M3x14-Screw193"  # Fasteners workbench fastener (typed FeaturePython)
  Placement = pos=(300.41,255.1,42.9) rot=(0,0,-1;1.5708rad)
  Visibility1 = true
  diameter = 1
  invert = false
  leftHanded = false
  length = 9
  lengthCustom = 14
  matchOuter = false
  offset = 0
  thread = false
  type = 39
FEATURE [App::DocumentObjectGroup] Support_Foot  label="Support-Foot"
  Group = -> [Screw257,b_aux_staging_plate_foot_001_,Nut126]
FEATURE [App::DocumentObjectGroup] Build_Plate  label="Auxiliary-Staging-Plate"
  Group = -> [b_staging_plate1_001_,Screw235,Screw236,Screw237,Screw238,b_M5_tslot_nut1_001_036,b_M5_tslot_nut1_001_037,b_M5_tslot_nut1_001_038,b_M5_tslot_nut1_001_039,Support_Foot]
FEATURE [Part::FeaturePython] b_mobo_cover_plate_001_  label="mobo-top-cover001"  # a2plus imported part (geometry in sourceFile) (typed FeaturePython)
  Placement = pos=(0,31.05,0) rot=(0,0,1;0rad)
  a2p_Version = 0.4.60i
  fixedPosition = false
  objectType = a2pPart
  sourceFile = ./FDM/mobo-top-cover.FCStd
  subassemblyImport = false
  timeLastImport = 1.6766e+09
  updateColors = true
FEATURE [Part::FeaturePython] b_z_gantry_shorter_001_  label="z-gantry-right"  # a2plus imported part (geometry in sourceFile) (typed FeaturePython)
  Placement = pos=(453.15,174.98,125.54) rot=(1,0,0;1.5708rad)
  a2p_Version = V0.1
  fixedPosition = false
  objectType = a2pPart
  sourceFile = ./FDM/z-gantry.FCStd
  subassemblyImport = false
  timeLastImport = 1.66247e+09
  updateColors = true
FEATURE [Part::FeaturePython] b_z_gantry_shorter_001_001  label="z-gantry-left"  # a2plus imported part (geometry in sourceFile) (typed FeaturePython)
  Placement = pos=(405.49,174.9,125.57) rot=(1,0,0;1.5708rad)
  a2p_Version = V0.1
  fixedPosition = false
  objectType = a2pPart
  sourceFile = ./FDM/z-gantry.FCStd
  subassemblyImport = false
  timeLastImport = 1.66247e+09
  updateColors = true
FEATURE [App::DocumentObjectGroup] Group009  label="Left-Z-Gantry"
  Group = -> [b_FDM_0040_z_gantry_backplate_left_001_,Screw144,Screw146,b_OTS_0001_00_CP40_nozzle_holder_001_,b_MS4M_M51_001_,Screw201,Screw202,Screw216,Screw217,Screw218,Screw219,b_NEMA11_hollow_shaft_stepper1_001_,b_z_gantry_shorter_001_001]
FEATURE [Part::FeaturePython] b_y_coupler_bracket_001_  label="y-coupler-bracket"  # a2plus imported part (geometry in sourceFile) (typed FeaturePython)
  Placement = pos=(186.447,119.942,40.0011) rot=(0.57735,0.57735,-0.57735;4.18879rad)
  a2p_Version = V0.1
  fixedPosition = false
  objectType = a2pPart
  sourceFile = ./FDM/y-coupler-bracket.FCStd
  subassemblyImport = false
  timeLastImport = 1.66759e+09
  updateColors = true
FEATURE [Part::FeaturePython] Screw258  label="M3x10-Screw124"  # Fasteners workbench fastener (typed FeaturePython)
  Placement = pos=(180.31,135.09,43.1) rot=(0,0,-1;1.5708rad)
  Visibility1 = true
  diameter = 1
  invert = false
  leftHanded = false
  length = 2
  lengthCustom = 10
  matchOuter = false
  offset = 0
  thread = false
  type = 39
FEATURE [Part::FeaturePython] b_OTS_0009_pneumatic_splitter_URY6M_4M1_001_002  label="pneumatic-y-adapter002"  # a2plus imported part (geometry in sourceFile) (typed FeaturePython)
  Placement = pos=(202.73,112.644,24.3499) rot=(0.57735,-0.57735,0.57735;2.0944rad)
  a2p_Version = V0.1
  fixedPosition = false
  objectType = a2pPart
  sourceFile = ./MISC/pneumatic-y-adapter.STEP
  subassemblyImport = false
  timeLastImport = 1.65531e+09
  updateColors = true
FEATURE [Part::FeaturePython] Nut127  label="M3-Nut568"  # Fasteners workbench fastener (typed FeaturePython)
  Placement = pos=(180.56,103.69,24.35) rot=(0.57735,0.57735,0.57735;4.18879rad)
  Visibility1 = true
  diameter = 4
  invert = false
  leftHanded = false
  matchOuter = false
  offset = 0
  thread = false
  type = 7
FEATURE [App::DocumentObjectGroup] Staging_Plate  label="Primary-Staging-Plate"
  Group = -> [Screw174,Screw175,Screw176,Screw177,Nut052,Nut053,Nut054,Nut055,Screw139,Screw142,Nut057,Nut058,Screw178,Screw179,Screw180,Screw134,Screw152,Screw153,Screw154,Screw155,b_FDM_0024_nozzle_holder_001_,Nut064,Nut066,Screw156,Screw158,Screw159,Screw160,Screw161,Screw162,b_CSM_0001_staging_plate_001_,b_M5_tslot_nut1_001_030,b_M5_tslot_nut1_001_031,b_M5_tslot_nut1_001_032,b_M5_tslot_nut1_001_033,+55 more]
FEATURE [App::DocumentObjectGroup] Group003  label="Staging-Plates"
  Group = -> [Staging_Plate,Build_Plate]
FEATURE [Part::FeaturePython] Nut128  label="M3-Nut578"  # Fasteners workbench fastener (typed FeaturePython)
  Placement = pos=(494.62,192.32,196.26) rot=(0.935113,0.250563,-0.250563;1.63783rad)
  diameter = 4
  invert = false
  leftHanded = false
  matchOuter = false
  offset = 0
  thread = false
  type = 9
FEATURE [Part::FeaturePython] Nut129  label="M3-Nut579"  # Fasteners workbench fastener (typed FeaturePython)
  Placement = pos=(475.62,192.32,196.26) rot=(0.935113,0.250563,-0.250563;1.63783rad)
  diameter = 4
  invert = false
  leftHanded = false
  matchOuter = false
  offset = 0
  thread = false
  type = 9
FEATURE [App::DocumentObjectGroup] Group016  label="EndStop"
  Group = -> [b_MakerBot_LimitSwitchBoard1_001_002,Screw123,Screw124,Nut128,Nut129]
FEATURE [Part::FeaturePython] Screw259  label="M3x16-Screw106"  # Fasteners workbench fastener (typed FeaturePython)
  Placement = pos=(478.244,182.32,160.243) rot=(0,0,-1;1.5708rad)
  baseObject = -> b_FDM_0043_001_001 [Edge69]
  diameter = 3
  invert = false
  leftHanded = false
  length = 3
  lengthCustom = 16
  matchOuter = false
  offset = 0
  thread = false
  type = 17
FEATURE [App::DocumentObjectGroup] Group010  label="Right-Z-Gantry"
  Group = -> [Screw148,Screw149,b_FDM_0041_z_gantry_backplate_right_001_,Screw199,Screw200,b_NEMA11_hollow_shaft_stepper1_001_001,b_OTS_0001_00_CP40_nozzle_holder_001_001,b_MS4M_M51_001_001,Screw248,Screw246,Screw249,Screw247,b_z_gantry_shorter_001_,Screw259]
FEATURE [App::DocumentObjectGroup] Group002  label="Toolhead"
  Group = -> [Group015,Group009,Group010,Group012,Group014,Group016,Group013]
FEATURE [App::DocumentObjectGroup] SDfsdf  label="X-Gantry"
  Group = -> [Group002,X_Gantry_Removable_Subassembly]
